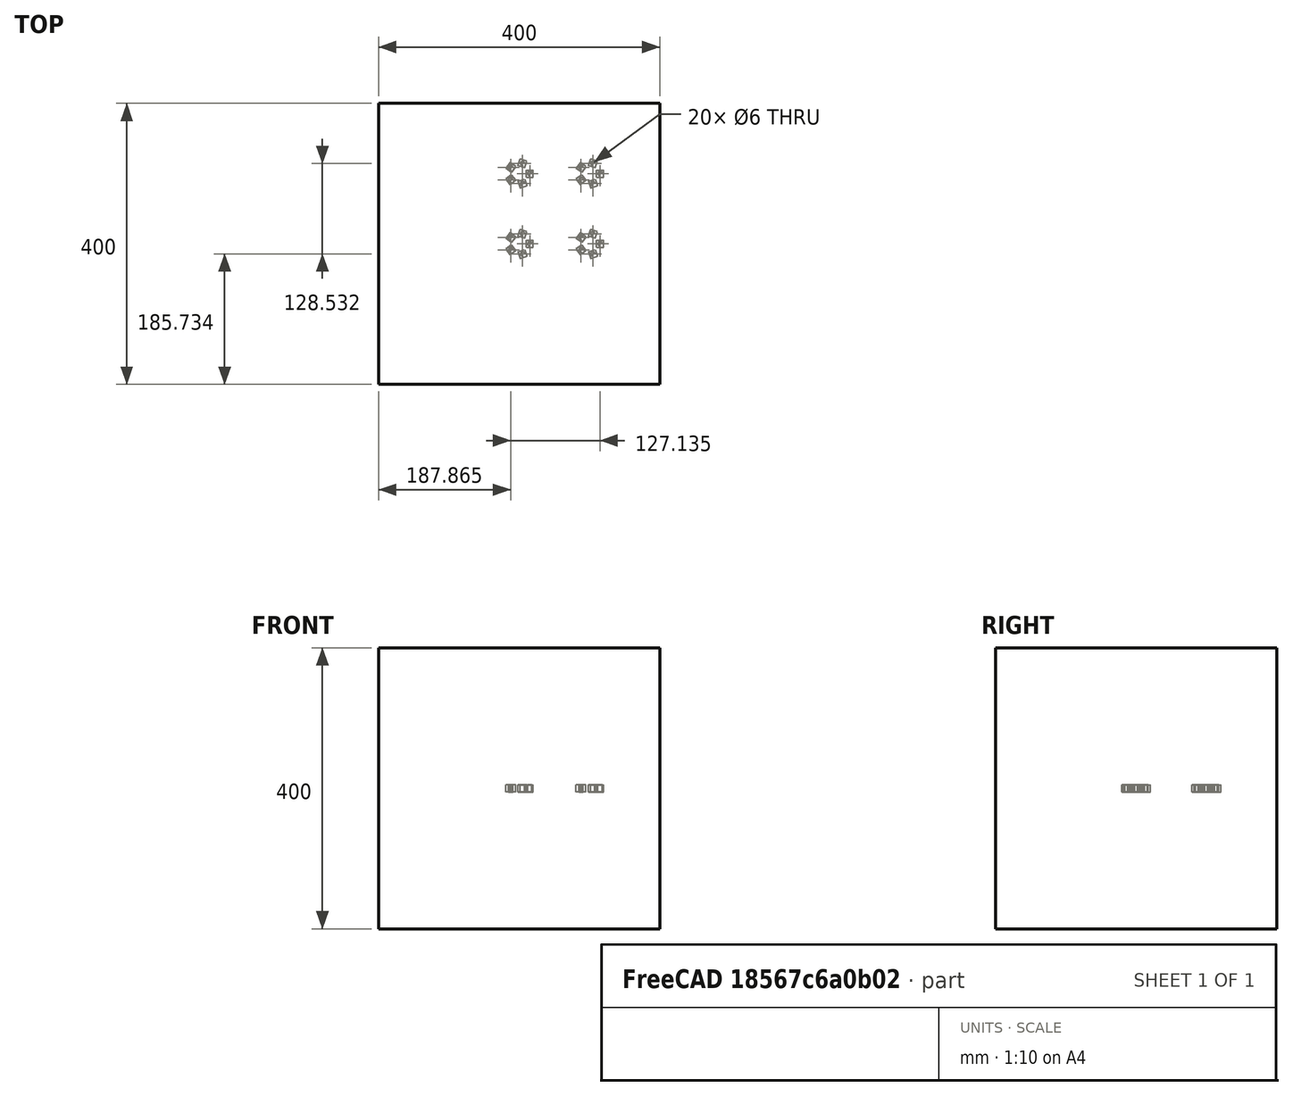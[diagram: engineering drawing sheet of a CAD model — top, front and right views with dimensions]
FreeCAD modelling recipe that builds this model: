
FCSTD DOCUMENT  (FreeCAD 0.19RUnknown)
Label: arrayTest-2
License: All rights reserved
LicenseURL: http://en.wikipedia.org/wiki/All_rights_reserved
objects: App::DocumentObjectGroupPython×1248, Part::FeaturePython×5, App::Part×2, Part::Cut×1
note: 6 computed .brp shape members not serialized (recipe doc carries the construction recipe); baked Part::Feature solids carry a one-line shape summary decoded from their .brp

FEATURE [App::DocumentObjectGroupPython] HALFPI  # scripted group (container) (typed FeaturePython)
  name = HALFPI
  value = pi/2.
FEATURE [App::DocumentObjectGroupPython] PI  # scripted group (container) (typed FeaturePython)
  name = PI
  value = 1.*pi
FEATURE [App::DocumentObjectGroupPython] TWOPI  # scripted group (container) (typed FeaturePython)
  name = TWOPI
  value = 2.*pi
FEATURE [App::DocumentObjectGroupPython] Constants  # scripted group (container) (typed FeaturePython)
  Group = -> [HALFPI,PI,TWOPI]
FEATURE [App::DocumentObjectGroupPython] Variables  # scripted group (container) (typed FeaturePython)
FEATURE [App::DocumentObjectGroupPython] Quantities  # scripted group (container) (typed FeaturePython)
FEATURE [App::DocumentObjectGroupPython] Isotopes  # scripted group (container) (typed FeaturePython)
FEATURE [App::DocumentObjectGroupPython] Elements  # scripted group (container) (typed FeaturePython)
FEATURE [App::DocumentObjectGroupPython] G4Isotopes  # scripted group (container) (typed FeaturePython)
FEATURE [App::DocumentObjectGroupPython] H_element  # scripted group (container) (typed FeaturePython)
  Z = 1
  atom_value = 1.008
  formula = H
  name = H_element
FEATURE [App::DocumentObjectGroupPython] He_element  # scripted group (container) (typed FeaturePython)
  Z = 2
  atom_value = 4.0026
  formula = He
  name = He_element
FEATURE [App::DocumentObjectGroupPython] Li_element  # scripted group (container) (typed FeaturePython)
  Z = 3
  atom_value = 6.94
  formula = Li
  name = Li_element
FEATURE [App::DocumentObjectGroupPython] Be_element  # scripted group (container) (typed FeaturePython)
  Z = 4
  atom_value = 9.01218
  formula = Be
  name = Be_element
FEATURE [App::DocumentObjectGroupPython] B_element  # scripted group (container) (typed FeaturePython)
  Z = 5
  atom_value = 10.81
  formula = B
  name = B_element
FEATURE [App::DocumentObjectGroupPython] C_element  # scripted group (container) (typed FeaturePython)
  Z = 6
  atom_value = 12.011
  formula = C
  name = C_element
FEATURE [App::DocumentObjectGroupPython] N_element  # scripted group (container) (typed FeaturePython)
  Z = 7
  atom_value = 14.007
  formula = N
  name = N_element
FEATURE [App::DocumentObjectGroupPython] O_element  # scripted group (container) (typed FeaturePython)
  Z = 8
  atom_value = 15.999
  formula = O
  name = O_element
FEATURE [App::DocumentObjectGroupPython] F_element  # scripted group (container) (typed FeaturePython)
  Z = 9
  atom_value = 18.9984
  formula = F
  name = F_element
FEATURE [App::DocumentObjectGroupPython] Ne_element  # scripted group (container) (typed FeaturePython)
  Z = 10
  atom_value = 20.1797
  formula = Ne
  name = Ne_element
FEATURE [App::DocumentObjectGroupPython] Na_element  # scripted group (container) (typed FeaturePython)
  Z = 11
  atom_value = 22.9898
  formula = Na
  name = Na_element
FEATURE [App::DocumentObjectGroupPython] Mg_element  # scripted group (container) (typed FeaturePython)
  Z = 12
  atom_value = 24.305
  formula = Mg
  name = Mg_element
FEATURE [App::DocumentObjectGroupPython] Al_element  # scripted group (container) (typed FeaturePython)
  Z = 13
  atom_value = 26.9815
  formula = Al
  name = Al_element
FEATURE [App::DocumentObjectGroupPython] Si_element  # scripted group (container) (typed FeaturePython)
  Z = 14
  atom_value = 28.085
  formula = Si
  name = Si_element
FEATURE [App::DocumentObjectGroupPython] P_element  # scripted group (container) (typed FeaturePython)
  Z = 15
  atom_value = 30.9738
  formula = P
  name = P_element
FEATURE [App::DocumentObjectGroupPython] S_element  # scripted group (container) (typed FeaturePython)
  Z = 16
  atom_value = 32.06
  formula = S
  name = S_element
FEATURE [App::DocumentObjectGroupPython] Cl_element  # scripted group (container) (typed FeaturePython)
  Z = 17
  atom_value = 35.45
  formula = Cl
  name = Cl_element
FEATURE [App::DocumentObjectGroupPython] Ar_element  # scripted group (container) (typed FeaturePython)
  Z = 18
  atom_value = 39.95
  formula = Ar
  name = Ar_element
FEATURE [App::DocumentObjectGroupPython] K_element  # scripted group (container) (typed FeaturePython)
  Z = 19
  atom_value = 39.0983
  formula = K
  name = K_element
FEATURE [App::DocumentObjectGroupPython] Ca_element  # scripted group (container) (typed FeaturePython)
  Z = 20
  atom_value = 40.078
  formula = Ca
  name = Ca_element
FEATURE [App::DocumentObjectGroupPython] Sc_element  # scripted group (container) (typed FeaturePython)
  Z = 21
  atom_value = 44.9559
  formula = Sc
  name = Sc_element
FEATURE [App::DocumentObjectGroupPython] Ti_element  # scripted group (container) (typed FeaturePython)
  Z = 22
  atom_value = 47.867
  formula = Ti
  name = Ti_element
FEATURE [App::DocumentObjectGroupPython] V_element  # scripted group (container) (typed FeaturePython)
  Z = 23
  atom_value = 50.9415
  formula = V
  name = V_element
FEATURE [App::DocumentObjectGroupPython] Cr_element  # scripted group (container) (typed FeaturePython)
  Z = 24
  atom_value = 51.9961
  formula = Cr
  name = Cr_element
FEATURE [App::DocumentObjectGroupPython] Mn_element  # scripted group (container) (typed FeaturePython)
  Z = 25
  atom_value = 54.938
  formula = Mn
  name = Mn_element
FEATURE [App::DocumentObjectGroupPython] Fe_element  # scripted group (container) (typed FeaturePython)
  Z = 26
  atom_value = 55.845
  formula = Fe
  name = Fe_element
FEATURE [App::DocumentObjectGroupPython] Co_element  # scripted group (container) (typed FeaturePython)
  Z = 27
  atom_value = 58.9332
  formula = Co
  name = Co_element
FEATURE [App::DocumentObjectGroupPython] Ni_element  # scripted group (container) (typed FeaturePython)
  Z = 28
  atom_value = 58.6934
  formula = Ni
  name = Ni_element
FEATURE [App::DocumentObjectGroupPython] Cu_element  # scripted group (container) (typed FeaturePython)
  Z = 29
  atom_value = 63.546
  formula = Cu
  name = Cu_element
FEATURE [App::DocumentObjectGroupPython] Zn_element  # scripted group (container) (typed FeaturePython)
  Z = 30
  atom_value = 65.38
  formula = Zn
  name = Zn_element
FEATURE [App::DocumentObjectGroupPython] Ga_element  # scripted group (container) (typed FeaturePython)
  Z = 31
  atom_value = 69.723
  formula = Ga
  name = Ga_element
FEATURE [App::DocumentObjectGroupPython] Ge_element  # scripted group (container) (typed FeaturePython)
  Z = 32
  atom_value = 72.63
  formula = Ge
  name = Ge_element
FEATURE [App::DocumentObjectGroupPython] As_element  # scripted group (container) (typed FeaturePython)
  Z = 33
  atom_value = 74.9216
  formula = As
  name = As_element
FEATURE [App::DocumentObjectGroupPython] Se_element  # scripted group (container) (typed FeaturePython)
  Z = 34
  atom_value = 78.971
  formula = Se
  name = Se_element
FEATURE [App::DocumentObjectGroupPython] Br_element  # scripted group (container) (typed FeaturePython)
  Z = 35
  atom_value = 79.904
  formula = Br
  name = Br_element
FEATURE [App::DocumentObjectGroupPython] Kr_element  # scripted group (container) (typed FeaturePython)
  Z = 36
  atom_value = 83.798
  formula = Kr
  name = Kr_element
FEATURE [App::DocumentObjectGroupPython] Rb_element  # scripted group (container) (typed FeaturePython)
  Z = 37
  atom_value = 85.4678
  formula = Rb
  name = Rb_element
FEATURE [App::DocumentObjectGroupPython] Sr_element  # scripted group (container) (typed FeaturePython)
  Z = 38
  atom_value = 87.62
  formula = Sr
  name = Sr_element
FEATURE [App::DocumentObjectGroupPython] Y_element  # scripted group (container) (typed FeaturePython)
  Z = 39
  atom_value = 88.9058
  formula = Y
  name = Y_element
FEATURE [App::DocumentObjectGroupPython] Zr_element  # scripted group (container) (typed FeaturePython)
  Z = 40
  atom_value = 91.224
  formula = Zr
  name = Zr_element
FEATURE [App::DocumentObjectGroupPython] Nb_element  # scripted group (container) (typed FeaturePython)
  Z = 41
  atom_value = 92.9064
  formula = Nb
  name = Nb_element
FEATURE [App::DocumentObjectGroupPython] Mo_element  # scripted group (container) (typed FeaturePython)
  Z = 42
  atom_value = 95.95
  formula = Mo
  name = Mo_element
FEATURE [App::DocumentObjectGroupPython] Tc_element  # scripted group (container) (typed FeaturePython)
  Z = 43
  atom_value = 97
  formula = Tc
  name = Tc_element
FEATURE [App::DocumentObjectGroupPython] Ru_element  # scripted group (container) (typed FeaturePython)
  Z = 44
  atom_value = 101.07
  formula = Ru
  name = Ru_element
FEATURE [App::DocumentObjectGroupPython] Rh_element  # scripted group (container) (typed FeaturePython)
  Z = 45
  atom_value = 102.905
  formula = Rh
  name = Rh_element
FEATURE [App::DocumentObjectGroupPython] Pd_element  # scripted group (container) (typed FeaturePython)
  Z = 46
  atom_value = 106.42
  formula = Pd
  name = Pd_element
FEATURE [App::DocumentObjectGroupPython] Ag_element  # scripted group (container) (typed FeaturePython)
  Z = 47
  atom_value = 107.868
  formula = Ag
  name = Ag_element
FEATURE [App::DocumentObjectGroupPython] Cd_element  # scripted group (container) (typed FeaturePython)
  Z = 48
  atom_value = 112.414
  formula = Cd
  name = Cd_element
FEATURE [App::DocumentObjectGroupPython] In_element  # scripted group (container) (typed FeaturePython)
  Z = 49
  atom_value = 114.818
  formula = In
  name = In_element
FEATURE [App::DocumentObjectGroupPython] Sn_element  # scripted group (container) (typed FeaturePython)
  Z = 50
  atom_value = 118.71
  formula = Sn
  name = Sn_element
FEATURE [App::DocumentObjectGroupPython] Sb_element  # scripted group (container) (typed FeaturePython)
  Z = 51
  atom_value = 121.76
  formula = Sb
  name = Sb_element
FEATURE [App::DocumentObjectGroupPython] Te_element  # scripted group (container) (typed FeaturePython)
  Z = 52
  atom_value = 127.6
  formula = Te
  name = Te_element
FEATURE [App::DocumentObjectGroupPython] I_element  # scripted group (container) (typed FeaturePython)
  Z = 53
  atom_value = 126.904
  formula = I
  name = I_element
FEATURE [App::DocumentObjectGroupPython] Xe_element  # scripted group (container) (typed FeaturePython)
  Z = 54
  atom_value = 131.293
  formula = Xe
  name = Xe_element
FEATURE [App::DocumentObjectGroupPython] Cs_element  # scripted group (container) (typed FeaturePython)
  Z = 55
  atom_value = 132.905
  formula = Cs
  name = Cs_element
FEATURE [App::DocumentObjectGroupPython] Ba_element  # scripted group (container) (typed FeaturePython)
  Z = 56
  atom_value = 137.327
  formula = Ba
  name = Ba_element
FEATURE [App::DocumentObjectGroupPython] La_element  # scripted group (container) (typed FeaturePython)
  Z = 57
  atom_value = 138.905
  formula = La
  name = La_element
FEATURE [App::DocumentObjectGroupPython] Ce_element  # scripted group (container) (typed FeaturePython)
  Z = 58
  atom_value = 140.116
  formula = Ce
  name = Ce_element
FEATURE [App::DocumentObjectGroupPython] Pr_element  # scripted group (container) (typed FeaturePython)
  Z = 59
  atom_value = 140.908
  formula = Pr
  name = Pr_element
FEATURE [App::DocumentObjectGroupPython] Nd_element  # scripted group (container) (typed FeaturePython)
  Z = 60
  atom_value = 144.242
  formula = Nd
  name = Nd_element
FEATURE [App::DocumentObjectGroupPython] Pm_element  # scripted group (container) (typed FeaturePython)
  Z = 61
  atom_value = 145
  formula = Pm
  name = Pm_element
FEATURE [App::DocumentObjectGroupPython] Sm_element  # scripted group (container) (typed FeaturePython)
  Z = 62
  atom_value = 150.36
  formula = Sm
  name = Sm_element
FEATURE [App::DocumentObjectGroupPython] Eu_element  # scripted group (container) (typed FeaturePython)
  Z = 63
  atom_value = 151.964
  formula = Eu
  name = Eu_element
FEATURE [App::DocumentObjectGroupPython] Gd_element  # scripted group (container) (typed FeaturePython)
  Z = 64
  atom_value = 157.25
  formula = Gd
  name = Gd_element
FEATURE [App::DocumentObjectGroupPython] Tb_element  # scripted group (container) (typed FeaturePython)
  Z = 65
  atom_value = 158.925
  formula = Tb
  name = Tb_element
FEATURE [App::DocumentObjectGroupPython] Dy_element  # scripted group (container) (typed FeaturePython)
  Z = 66
  atom_value = 162.5
  formula = Dy
  name = Dy_element
FEATURE [App::DocumentObjectGroupPython] Ho_element  # scripted group (container) (typed FeaturePython)
  Z = 67
  atom_value = 164.93
  formula = Ho
  name = Ho_element
FEATURE [App::DocumentObjectGroupPython] Er_element  # scripted group (container) (typed FeaturePython)
  Z = 68
  atom_value = 167.259
  formula = Er
  name = Er_element
FEATURE [App::DocumentObjectGroupPython] Tm_element  # scripted group (container) (typed FeaturePython)
  Z = 69
  atom_value = 168.934
  formula = Tm
  name = Tm_element
FEATURE [App::DocumentObjectGroupPython] Yb_element  # scripted group (container) (typed FeaturePython)
  Z = 70
  atom_value = 173.045
  formula = Yb
  name = Yb_element
FEATURE [App::DocumentObjectGroupPython] Lu_element  # scripted group (container) (typed FeaturePython)
  Z = 71
  atom_value = 174.967
  formula = Lu
  name = Lu_element
FEATURE [App::DocumentObjectGroupPython] Hf_element  # scripted group (container) (typed FeaturePython)
  Z = 72
  atom_value = 178.49
  formula = Hf
  name = Hf_element
FEATURE [App::DocumentObjectGroupPython] Ta_element  # scripted group (container) (typed FeaturePython)
  Z = 73
  atom_value = 180.948
  formula = Ta
  name = Ta_element
FEATURE [App::DocumentObjectGroupPython] W_element  # scripted group (container) (typed FeaturePython)
  Z = 74
  atom_value = 183.84
  formula = W
  name = W_element
FEATURE [App::DocumentObjectGroupPython] Re_element  # scripted group (container) (typed FeaturePython)
  Z = 75
  atom_value = 186.207
  formula = Re
  name = Re_element
FEATURE [App::DocumentObjectGroupPython] Os_element  # scripted group (container) (typed FeaturePython)
  Z = 76
  atom_value = 190.23
  formula = Os
  name = Os_element
FEATURE [App::DocumentObjectGroupPython] Ir_element  # scripted group (container) (typed FeaturePython)
  Z = 77
  atom_value = 192.217
  formula = Ir
  name = Ir_element
FEATURE [App::DocumentObjectGroupPython] Pt_element  # scripted group (container) (typed FeaturePython)
  Z = 78
  atom_value = 195.084
  formula = Pt
  name = Pt_element
FEATURE [App::DocumentObjectGroupPython] Au_element  # scripted group (container) (typed FeaturePython)
  Z = 79
  atom_value = 196.967
  formula = Au
  name = Au_element
FEATURE [App::DocumentObjectGroupPython] Hg_element  # scripted group (container) (typed FeaturePython)
  Z = 80
  atom_value = 200.592
  formula = Hg
  name = Hg_element
FEATURE [App::DocumentObjectGroupPython] Tl_element  # scripted group (container) (typed FeaturePython)
  Z = 81
  atom_value = 204.38
  formula = Tl
  name = Tl_element
FEATURE [App::DocumentObjectGroupPython] Pb_element  # scripted group (container) (typed FeaturePython)
  Z = 82
  atom_value = 207.2
  formula = Pb
  name = Pb_element
FEATURE [App::DocumentObjectGroupPython] Bi_element  # scripted group (container) (typed FeaturePython)
  Z = 83
  atom_value = 208.98
  formula = Bi
  name = Bi_element
FEATURE [App::DocumentObjectGroupPython] Po_element  # scripted group (container) (typed FeaturePython)
  Z = 84
  atom_value = 209
  formula = Po
  name = Po_element
FEATURE [App::DocumentObjectGroupPython] At_element  # scripted group (container) (typed FeaturePython)
  Z = 85
  atom_value = 210
  formula = At
  name = At_element
FEATURE [App::DocumentObjectGroupPython] Rn_element  # scripted group (container) (typed FeaturePython)
  Z = 86
  atom_value = 222
  formula = Rn
  name = Rn_element
FEATURE [App::DocumentObjectGroupPython] Fr_element  # scripted group (container) (typed FeaturePython)
  Z = 87
  atom_value = 223
  formula = Fr
  name = Fr_element
FEATURE [App::DocumentObjectGroupPython] Ra_element  # scripted group (container) (typed FeaturePython)
  Z = 88
  atom_value = 226
  formula = Ra
  name = Ra_element
FEATURE [App::DocumentObjectGroupPython] Ac_element  # scripted group (container) (typed FeaturePython)
  Z = 89
  atom_value = 227
  formula = Ac
  name = Ac_element
FEATURE [App::DocumentObjectGroupPython] Th_element  # scripted group (container) (typed FeaturePython)
  Z = 90
  atom_value = 232.038
  formula = Th
  name = Th_element
FEATURE [App::DocumentObjectGroupPython] Pa_element  # scripted group (container) (typed FeaturePython)
  Z = 91
  atom_value = 231.036
  formula = Pa
  name = Pa_element
FEATURE [App::DocumentObjectGroupPython] U_element  # scripted group (container) (typed FeaturePython)
  Z = 92
  atom_value = 238.029
  formula = U
  name = U_element
FEATURE [App::DocumentObjectGroupPython] Np_element  # scripted group (container) (typed FeaturePython)
  Z = 93
  atom_value = 237
  formula = Np
  name = Np_element
FEATURE [App::DocumentObjectGroupPython] Pu_element  # scripted group (container) (typed FeaturePython)
  Z = 94
  atom_value = 244
  formula = Pu
  name = Pu_element
FEATURE [App::DocumentObjectGroupPython] Am_element  # scripted group (container) (typed FeaturePython)
  Z = 95
  atom_value = 243
  formula = Am
  name = Am_element
FEATURE [App::DocumentObjectGroupPython] Cm_element  # scripted group (container) (typed FeaturePython)
  Z = 96
  atom_value = 247
  formula = Cm
  name = Cm_element
FEATURE [App::DocumentObjectGroupPython] Bk_element  # scripted group (container) (typed FeaturePython)
  Z = 97
  atom_value = 247
  formula = Bk
  name = Bk_element
FEATURE [App::DocumentObjectGroupPython] Cf_element  # scripted group (container) (typed FeaturePython)
  Z = 98
  atom_value = 251
  formula = Cf
  name = Cf_element
FEATURE [App::DocumentObjectGroupPython] G4Elements  # scripted group (container) (typed FeaturePython)
  Group = -> [H_element,He_element,Li_element,Be_element,B_element,C_element,N_element,O_element,F_element,Ne_element,Na_element,Mg_element,Al_element,Si_element,P_element,S_element,Cl_element,Ar_element,K_element,Ca_element,Sc_element,Ti_element,V_element,Cr_element,Mn_element,Fe_element,Co_element,Ni_element,Cu_element,Zn_element,Ga_element,Ge_element,As_element,Se_element,Br_element,Kr_element,Rb_element,+61 more]
FEATURE [App::DocumentObjectGroupPython] H_element001  label="H_element : 0.101"  # scripted group (container) (typed FeaturePython)
  n = 0.101327
FEATURE [App::DocumentObjectGroupPython] C_element001  label="C_element : 0.775"  # scripted group (container) (typed FeaturePython)
  n = 0.7755
FEATURE [App::DocumentObjectGroupPython] N_element001  label="N_element : 0.035"  # scripted group (container) (typed FeaturePython)
  n = 0.035057
FEATURE [App::DocumentObjectGroupPython] O_element001  label="O_element : 0.052"  # scripted group (container) (typed FeaturePython)
  n = 0.0523159
FEATURE [App::DocumentObjectGroupPython] F_element001  label="F_element : 0.017"  # scripted group (container) (typed FeaturePython)
  n = 0.017422
FEATURE [App::DocumentObjectGroupPython] Ca_element001  label="Ca_element : 0.018"  # scripted group (container) (typed FeaturePython)
  n = 0.018378
FEATURE [App::DocumentObjectGroupPython] G4_A_150_TISSUE  label="G4_A-150_TISSUE"  # scripted group (container) (typed FeaturePython)
  Dunit = g/cm3
  Dvalue = 1.127
  Group = -> [H_element001,C_element001,N_element001,O_element001,F_element001,Ca_element001]
  conduct = 2
  density = 1
  expand = 3
  formula = G4_A-150_TISSUE
  name = G4_A-150_TISSUE
  specific = 4
FEATURE [App::DocumentObjectGroupPython] C_element002  label="C_element : 3"  # scripted group (container) (typed FeaturePython)
  n = 3
  ref = C_element
FEATURE [App::DocumentObjectGroupPython] H_element002  label="H_element : 6"  # scripted group (container) (typed FeaturePython)
  n = 6
  ref = H_element
FEATURE [App::DocumentObjectGroupPython] O_element002  label="O_element : 1"  # scripted group (container) (typed FeaturePython)
  n = 1
  ref = O_element
FEATURE [App::DocumentObjectGroupPython] G4_ACETONE  # scripted group (container) (typed FeaturePython)
  Dunit = g/cm3
  Dvalue = 0.7899
  Group = -> [C_element002,H_element002,O_element002]
  conduct = 2
  density = 1
  expand = 3
  formula = G4_ACETONE
  name = G4_ACETONE
  specific = 4
FEATURE [App::DocumentObjectGroupPython] C_element003  label="C_element : 2"  # scripted group (container) (typed FeaturePython)
  n = 2
  ref = C_element
FEATURE [App::DocumentObjectGroupPython] H_element003  label="H_element : 2"  # scripted group (container) (typed FeaturePython)
  n = 2
  ref = H_element
FEATURE [App::DocumentObjectGroupPython] G4_ACETYLENE  # scripted group (container) (typed FeaturePython)
  Dunit = g/cm3
  Dvalue = 0.0010967
  Group = -> [C_element003,H_element003]
  conduct = 2
  density = 1
  expand = 3
  formula = G4_ACETYLENE
  name = G4_ACETYLENE
  specific = 4
FEATURE [App::DocumentObjectGroupPython] C_element004  label="C_element : 5"  # scripted group (container) (typed FeaturePython)
  n = 5
  ref = C_element
FEATURE [App::DocumentObjectGroupPython] H_element004  label="H_element : 5"  # scripted group (container) (typed FeaturePython)
  n = 5
  ref = H_element
FEATURE [App::DocumentObjectGroupPython] N_element002  label="N_element : 5"  # scripted group (container) (typed FeaturePython)
  n = 5
  ref = N_element
FEATURE [App::DocumentObjectGroupPython] G4_ADENINE  # scripted group (container) (typed FeaturePython)
  Dunit = g/cm3
  Dvalue = 1.6
  Group = -> [C_element004,H_element004,N_element002]
  conduct = 2
  density = 1
  expand = 3
  formula = G4_ADENINE
  name = G4_ADENINE
  specific = 4
FEATURE [App::DocumentObjectGroupPython] H_element005  label="H_element : 0.114"  # scripted group (container) (typed FeaturePython)
  n = 0.114
FEATURE [App::DocumentObjectGroupPython] C_element005  label="C_element : 0.598"  # scripted group (container) (typed FeaturePython)
  n = 0.598
FEATURE [App::DocumentObjectGroupPython] N_element003  label="N_element : 0.007"  # scripted group (container) (typed FeaturePython)
  n = 0.007
FEATURE [App::DocumentObjectGroupPython] O_element003  label="O_element : 0.278"  # scripted group (container) (typed FeaturePython)
  n = 0.278
FEATURE [App::DocumentObjectGroupPython] Na_element001  label="Na_element : 0.001"  # scripted group (container) (typed FeaturePython)
  n = 0.001
FEATURE [App::DocumentObjectGroupPython] S_element001  label="S_element : 0.001"  # scripted group (container) (typed FeaturePython)
  n = 0.001
FEATURE [App::DocumentObjectGroupPython] Cl_element001  label="Cl_element : 0.001"  # scripted group (container) (typed FeaturePython)
  n = 0.001
FEATURE [App::DocumentObjectGroupPython] G4_ADIPOSE_TISSUE_ICRP  # scripted group (container) (typed FeaturePython)
  Dunit = g/cm3
  Dvalue = 0.95
  Group = -> [H_element005,C_element005,N_element003,O_element003,Na_element001,S_element001,Cl_element001]
  conduct = 2
  density = 1
  expand = 3
  formula = G4_ADIPOSE_TISSUE_ICRP
  name = G4_ADIPOSE_TISSUE_ICRP
  specific = 4
FEATURE [App::DocumentObjectGroupPython] C_element006  label="C_element : 0.000"  # scripted group (container) (typed FeaturePython)
  n = 0.000124
FEATURE [App::DocumentObjectGroupPython] N_element004  label="N_element : 0.755"  # scripted group (container) (typed FeaturePython)
  n = 0.755268
FEATURE [App::DocumentObjectGroupPython] O_element004  label="O_element : 0.232"  # scripted group (container) (typed FeaturePython)
  n = 0.231781
FEATURE [App::DocumentObjectGroupPython] Ar_element001  label="Ar_element : 0.013"  # scripted group (container) (typed FeaturePython)
  n = 0.012827
FEATURE [App::DocumentObjectGroupPython] G4_AIR  # scripted group (container) (typed FeaturePython)
  Dunit = g/cm3
  Dvalue = 0.00120479
  Group = -> [C_element006,N_element004,O_element004,Ar_element001]
  conduct = 2
  density = 1
  expand = 3
  formula = G4_AIR
  name = G4_AIR
  specific = 4
FEATURE [App::DocumentObjectGroupPython] C_element007  label="C_element : 006"  # scripted group (container) (typed FeaturePython)
  n = 3
  ref = C_element
FEATURE [App::DocumentObjectGroupPython] H_element006  label="H_element : 7"  # scripted group (container) (typed FeaturePython)
  n = 7
  ref = H_element
FEATURE [App::DocumentObjectGroupPython] N_element005  label="N_element : 1"  # scripted group (container) (typed FeaturePython)
  n = 1
  ref = N_element
FEATURE [App::DocumentObjectGroupPython] O_element005  label="O_element : 2"  # scripted group (container) (typed FeaturePython)
  n = 2
  ref = O_element
FEATURE [App::DocumentObjectGroupPython] G4_ALANINE  # scripted group (container) (typed FeaturePython)
  Dunit = g/cm3
  Dvalue = 1.42
  Group = -> [C_element007,H_element006,N_element005,O_element005]
  conduct = 2
  density = 1
  expand = 3
  formula = G4_ALANINE
  name = G4_ALANINE
  specific = 4
FEATURE [App::DocumentObjectGroupPython] Al_element001  label="Al_element : 2"  # scripted group (container) (typed FeaturePython)
  n = 2
  ref = Al_element
FEATURE [App::DocumentObjectGroupPython] O_element006  label="O_element : 3"  # scripted group (container) (typed FeaturePython)
  n = 3
  ref = O_element
FEATURE [App::DocumentObjectGroupPython] G4_ALUMINUM_OXIDE  # scripted group (container) (typed FeaturePython)
  Dunit = g/cm3
  Dvalue = 3.97
  Group = -> [Al_element001,O_element006]
  conduct = 2
  density = 1
  expand = 3
  formula = G4_ALUMINUM_OXIDE
  name = G4_ALUMINUM_OXIDE
  specific = 4
FEATURE [App::DocumentObjectGroupPython] H_element007  label="H_element : 0.106"  # scripted group (container) (typed FeaturePython)
  n = 0.10593
FEATURE [App::DocumentObjectGroupPython] C_element008  label="C_element : 0.789"  # scripted group (container) (typed FeaturePython)
  n = 0.788974
FEATURE [App::DocumentObjectGroupPython] O_element007  label="O_element : 0.105"  # scripted group (container) (typed FeaturePython)
  n = 0.105096
FEATURE [App::DocumentObjectGroupPython] G4_AMBER  # scripted group (container) (typed FeaturePython)
  Dunit = g/cm3
  Dvalue = 1.1
  Group = -> [H_element007,C_element008,O_element007]
  conduct = 2
  density = 1
  expand = 3
  formula = G4_AMBER
  name = G4_AMBER
  specific = 4
FEATURE [App::DocumentObjectGroupPython] N_element006  label="N_element : 006"  # scripted group (container) (typed FeaturePython)
  n = 1
  ref = N_element
FEATURE [App::DocumentObjectGroupPython] H_element008  label="H_element : 3"  # scripted group (container) (typed FeaturePython)
  n = 3
  ref = H_element
FEATURE [App::DocumentObjectGroupPython] G4_AMMONIA  # scripted group (container) (typed FeaturePython)
  Dunit = g/cm3
  Dvalue = 0.000826019
  Group = -> [N_element006,H_element008]
  conduct = 2
  density = 1
  expand = 3
  formula = G4_AMMONIA
  name = G4_AMMONIA
  specific = 4
FEATURE [App::DocumentObjectGroupPython] C_element009  label="C_element : 6"  # scripted group (container) (typed FeaturePython)
  n = 6
  ref = C_element
FEATURE [App::DocumentObjectGroupPython] H_element009  label="H_element : 008"  # scripted group (container) (typed FeaturePython)
  n = 7
  ref = H_element
FEATURE [App::DocumentObjectGroupPython] N_element007  label="N_element : 007"  # scripted group (container) (typed FeaturePython)
  n = 1
  ref = N_element
FEATURE [App::DocumentObjectGroupPython] G4_ANILINE  # scripted group (container) (typed FeaturePython)
  Dunit = g/cm3
  Dvalue = 1.0235
  Group = -> [C_element009,H_element009,N_element007]
  conduct = 2
  density = 1
  expand = 3
  formula = G4_ANILINE
  name = G4_ANILINE
  specific = 4
FEATURE [App::DocumentObjectGroupPython] C_element010  label="C_element : 14"  # scripted group (container) (typed FeaturePython)
  n = 14
  ref = C_element
FEATURE [App::DocumentObjectGroupPython] H_element010  label="H_element : 10"  # scripted group (container) (typed FeaturePython)
  n = 10
  ref = H_element
FEATURE [App::DocumentObjectGroupPython] G4_ANTHRACENE  # scripted group (container) (typed FeaturePython)
  Dunit = g/cm3
  Dvalue = 1.283
  Group = -> [C_element010,H_element010]
  conduct = 2
  density = 1
  expand = 3
  formula = G4_ANTHRACENE
  name = G4_ANTHRACENE
  specific = 4
FEATURE [App::DocumentObjectGroupPython] H_element011  label="H_element : 0.065"  # scripted group (container) (typed FeaturePython)
  n = 0.0654709
FEATURE [App::DocumentObjectGroupPython] C_element011  label="C_element : 0.537"  # scripted group (container) (typed FeaturePython)
  n = 0.536944
FEATURE [App::DocumentObjectGroupPython] N_element008  label="N_element : 0.021"  # scripted group (container) (typed FeaturePython)
  n = 0.0215
FEATURE [App::DocumentObjectGroupPython] O_element008  label="O_element : 0.032"  # scripted group (container) (typed FeaturePython)
  n = 0.032085
FEATURE [App::DocumentObjectGroupPython] F_element002  label="F_element : 0.167"  # scripted group (container) (typed FeaturePython)
  n = 0.167411
FEATURE [App::DocumentObjectGroupPython] Ca_element002  label="Ca_element : 0.177"  # scripted group (container) (typed FeaturePython)
  n = 0.176589
FEATURE [App::DocumentObjectGroupPython] G4_B_100_BONE  label="G4_B-100_BONE"  # scripted group (container) (typed FeaturePython)
  Dunit = g/cm3
  Dvalue = 1.45
  Group = -> [H_element011,C_element011,N_element008,O_element008,F_element002,Ca_element002]
  conduct = 2
  density = 1
  expand = 3
  formula = G4_B-100_BONE
  name = G4_B-100_BONE
  specific = 4
FEATURE [App::DocumentObjectGroupPython] H_element012  label="H_element : 0.057"  # scripted group (container) (typed FeaturePython)
  n = 0.057441
FEATURE [App::DocumentObjectGroupPython] C_element012  label="C_element : 0.790"  # scripted group (container) (typed FeaturePython)
  n = 0.774591
FEATURE [App::DocumentObjectGroupPython] O_element009  label="O_element : 0.168"  # scripted group (container) (typed FeaturePython)
  n = 0.167968
FEATURE [App::DocumentObjectGroupPython] G4_BAKELITE  # scripted group (container) (typed FeaturePython)
  Dunit = g/cm3
  Dvalue = 1.25
  Group = -> [H_element012,C_element012,O_element009]
  conduct = 2
  density = 1
  expand = 3
  formula = G4_BAKELITE
  name = G4_BAKELITE
  specific = 4
FEATURE [App::DocumentObjectGroupPython] Ba_element001  label="Ba_element : 1"  # scripted group (container) (typed FeaturePython)
  n = 1
  ref = Ba_element
FEATURE [App::DocumentObjectGroupPython] F_element003  label="F_element : 2"  # scripted group (container) (typed FeaturePython)
  n = 2
  ref = F_element
FEATURE [App::DocumentObjectGroupPython] G4_BARIUM_FLUORIDE  # scripted group (container) (typed FeaturePython)
  Dunit = g/cm3
  Dvalue = 4.89
  Group = -> [Ba_element001,F_element003]
  conduct = 2
  density = 1
  expand = 3
  formula = G4_BARIUM_FLUORIDE
  name = G4_BARIUM_FLUORIDE
  specific = 4
FEATURE [App::DocumentObjectGroupPython] Ba_element002  label="Ba_element : 002"  # scripted group (container) (typed FeaturePython)
  n = 1
  ref = Ba_element
FEATURE [App::DocumentObjectGroupPython] S_element002  label="S_element : 1"  # scripted group (container) (typed FeaturePython)
  n = 1
  ref = S_element
FEATURE [App::DocumentObjectGroupPython] O_element010  label="O_element : 4"  # scripted group (container) (typed FeaturePython)
  n = 4
  ref = O_element
FEATURE [App::DocumentObjectGroupPython] G4_BARIUM_SULFATE  # scripted group (container) (typed FeaturePython)
  Dunit = g/cm3
  Dvalue = 4.5
  Group = -> [Ba_element002,S_element002,O_element010]
  conduct = 2
  density = 1
  expand = 3
  formula = G4_BARIUM_SULFATE
  name = G4_BARIUM_SULFATE
  specific = 4
FEATURE [App::DocumentObjectGroupPython] C_element013  label="C_element : 007"  # scripted group (container) (typed FeaturePython)
  n = 6
  ref = C_element
FEATURE [App::DocumentObjectGroupPython] H_element013  label="H_element : 009"  # scripted group (container) (typed FeaturePython)
  n = 6
  ref = H_element
FEATURE [App::DocumentObjectGroupPython] G4_BENZENE  # scripted group (container) (typed FeaturePython)
  Dunit = g/cm3
  Dvalue = 0.87865
  Group = -> [C_element013,H_element013]
  conduct = 2
  density = 1
  expand = 3
  formula = G4_BENZENE
  name = G4_BENZENE
  specific = 4
FEATURE [App::DocumentObjectGroupPython] Be_element001  label="Be_element : 1"  # scripted group (container) (typed FeaturePython)
  n = 1
  ref = Be_element
FEATURE [App::DocumentObjectGroupPython] O_element011  label="O_element : 005"  # scripted group (container) (typed FeaturePython)
  n = 1
  ref = O_element
FEATURE [App::DocumentObjectGroupPython] G4_BERYLLIUM_OXIDE  # scripted group (container) (typed FeaturePython)
  Dunit = g/cm3
  Dvalue = 3.01
  Group = -> [Be_element001,O_element011]
  conduct = 2
  density = 1
  expand = 3
  formula = G4_BERYLLIUM_OXIDE
  name = G4_BERYLLIUM_OXIDE
  specific = 4
FEATURE [App::DocumentObjectGroupPython] Bi_element001  label="Bi_element : 4"  # scripted group (container) (typed FeaturePython)
  n = 4
  ref = Bi_element
FEATURE [App::DocumentObjectGroupPython] Ge_element001  label="Ge_element : 3"  # scripted group (container) (typed FeaturePython)
  n = 3
  ref = Ge_element
FEATURE [App::DocumentObjectGroupPython] O_element012  label="O_element : 12"  # scripted group (container) (typed FeaturePython)
  n = 12
  ref = O_element
FEATURE [App::DocumentObjectGroupPython] G4_BGO  # scripted group (container) (typed FeaturePython)
  Dunit = g/cm3
  Dvalue = 7.13
  Group = -> [Bi_element001,Ge_element001,O_element012]
  conduct = 2
  density = 1
  expand = 3
  formula = G4_BGO
  name = G4_BGO
  specific = 4
FEATURE [App::DocumentObjectGroupPython] H_element014  label="H_element : 0.102"  # scripted group (container) (typed FeaturePython)
  n = 0.102
FEATURE [App::DocumentObjectGroupPython] C_element014  label="C_element : 0.110"  # scripted group (container) (typed FeaturePython)
  n = 0.11
FEATURE [App::DocumentObjectGroupPython] N_element009  label="N_element : 0.033"  # scripted group (container) (typed FeaturePython)
  n = 0.033
FEATURE [App::DocumentObjectGroupPython] O_element013  label="O_element : 0.745"  # scripted group (container) (typed FeaturePython)
  n = 0.745
FEATURE [App::DocumentObjectGroupPython] Na_element002  label="Na_element : 0.002"  # scripted group (container) (typed FeaturePython)
  n = 0.001
FEATURE [App::DocumentObjectGroupPython] P_element001  label="P_element : 0.001"  # scripted group (container) (typed FeaturePython)
  n = 0.001
FEATURE [App::DocumentObjectGroupPython] S_element003  label="S_element : 0.002"  # scripted group (container) (typed FeaturePython)
  n = 0.002
FEATURE [App::DocumentObjectGroupPython] Cl_element002  label="Cl_element : 0.003"  # scripted group (container) (typed FeaturePython)
  n = 0.003
FEATURE [App::DocumentObjectGroupPython] K_element001  label="K_element : 0.002"  # scripted group (container) (typed FeaturePython)
  n = 0.002
FEATURE [App::DocumentObjectGroupPython] Fe_element001  label="Fe_element : 0.001"  # scripted group (container) (typed FeaturePython)
  n = 0.001
FEATURE [App::DocumentObjectGroupPython] G4_BLOOD_ICRP  # scripted group (container) (typed FeaturePython)
  Dunit = g/cm3
  Dvalue = 1.06
  Group = -> [H_element014,C_element014,N_element009,O_element013,Na_element002,P_element001,S_element003,Cl_element002,K_element001,Fe_element001]
  conduct = 2
  density = 1
  expand = 3
  formula = G4_BLOOD_ICRP
  name = G4_BLOOD_ICRP
  specific = 4
FEATURE [App::DocumentObjectGroupPython] H_element015  label="H_element : 0.064"  # scripted group (container) (typed FeaturePython)
  n = 0.064
FEATURE [App::DocumentObjectGroupPython] C_element015  label="C_element : 0.278"  # scripted group (container) (typed FeaturePython)
  n = 0.278
FEATURE [App::DocumentObjectGroupPython] N_element010  label="N_element : 0.027"  # scripted group (container) (typed FeaturePython)
  n = 0.027
FEATURE [App::DocumentObjectGroupPython] O_element014  label="O_element : 0.410"  # scripted group (container) (typed FeaturePython)
  n = 0.41
FEATURE [App::DocumentObjectGroupPython] Mg_element001  label="Mg_element : 0.002"  # scripted group (container) (typed FeaturePython)
  n = 0.002
FEATURE [App::DocumentObjectGroupPython] P_element002  label="P_element : 0.070"  # scripted group (container) (typed FeaturePython)
  n = 0.07
FEATURE [App::DocumentObjectGroupPython] S_element004  label="S_element : 0.003"  # scripted group (container) (typed FeaturePython)
  n = 0.002
FEATURE [App::DocumentObjectGroupPython] Ca_element003  label="Ca_element : 0.147"  # scripted group (container) (typed FeaturePython)
  n = 0.147
FEATURE [App::DocumentObjectGroupPython] G4_BONE_COMPACT_ICRU  # scripted group (container) (typed FeaturePython)
  Dunit = g/cm3
  Dvalue = 1.85
  Group = -> [H_element015,C_element015,N_element010,O_element014,Mg_element001,P_element002,S_element004,Ca_element003]
  conduct = 2
  density = 1
  expand = 3
  formula = G4_BONE_COMPACT_ICRU
  name = G4_BONE_COMPACT_ICRU
  specific = 4
FEATURE [App::DocumentObjectGroupPython] H_element016  label="H_element : 0.034"  # scripted group (container) (typed FeaturePython)
  n = 0.034
FEATURE [App::DocumentObjectGroupPython] C_element016  label="C_element : 0.155"  # scripted group (container) (typed FeaturePython)
  n = 0.155
FEATURE [App::DocumentObjectGroupPython] N_element011  label="N_element : 0.042"  # scripted group (container) (typed FeaturePython)
  n = 0.042
FEATURE [App::DocumentObjectGroupPython] O_element015  label="O_element : 0.435"  # scripted group (container) (typed FeaturePython)
  n = 0.435
FEATURE [App::DocumentObjectGroupPython] Na_element003  label="Na_element : 0.003"  # scripted group (container) (typed FeaturePython)
  n = 0.001
FEATURE [App::DocumentObjectGroupPython] Mg_element002  label="Mg_element : 0.003"  # scripted group (container) (typed FeaturePython)
  n = 0.002
FEATURE [App::DocumentObjectGroupPython] P_element003  label="P_element : 0.103"  # scripted group (container) (typed FeaturePython)
  n = 0.103
FEATURE [App::DocumentObjectGroupPython] S_element005  label="S_element : 0.004"  # scripted group (container) (typed FeaturePython)
  n = 0.003
FEATURE [App::DocumentObjectGroupPython] Ca_element004  label="Ca_element : 0.225"  # scripted group (container) (typed FeaturePython)
  n = 0.225
FEATURE [App::DocumentObjectGroupPython] G4_BONE_CORTICAL_ICRP  # scripted group (container) (typed FeaturePython)
  Dunit = g/cm3
  Dvalue = 1.92
  Group = -> [H_element016,C_element016,N_element011,O_element015,Na_element003,Mg_element002,P_element003,S_element005,Ca_element004]
  conduct = 2
  density = 1
  expand = 3
  formula = G4_BONE_CORTICAL_ICRP
  name = G4_BONE_CORTICAL_ICRP
  specific = 4
FEATURE [App::DocumentObjectGroupPython] B_element001  label="B_element : 4"  # scripted group (container) (typed FeaturePython)
  n = 4
  ref = B_element
FEATURE [App::DocumentObjectGroupPython] C_element017  label="C_element : 1"  # scripted group (container) (typed FeaturePython)
  n = 1
  ref = C_element
FEATURE [App::DocumentObjectGroupPython] G4_BORON_CARBIDE  # scripted group (container) (typed FeaturePython)
  Dunit = g/cm3
  Dvalue = 2.52
  Group = -> [B_element001,C_element017]
  conduct = 2
  density = 1
  expand = 3
  formula = G4_BORON_CARBIDE
  name = G4_BORON_CARBIDE
  specific = 4
FEATURE [App::DocumentObjectGroupPython] B_element002  label="B_element : 2"  # scripted group (container) (typed FeaturePython)
  n = 2
  ref = B_element
FEATURE [App::DocumentObjectGroupPython] O_element016  label="O_element : 006"  # scripted group (container) (typed FeaturePython)
  n = 3
  ref = O_element
FEATURE [App::DocumentObjectGroupPython] G4_BORON_OXIDE  # scripted group (container) (typed FeaturePython)
  Dunit = g/cm3
  Dvalue = 1.812
  Group = -> [B_element002,O_element016]
  conduct = 2
  density = 1
  expand = 3
  formula = G4_BORON_OXIDE
  name = G4_BORON_OXIDE
  specific = 4
FEATURE [App::DocumentObjectGroupPython] H_element017  label="H_element : 0.107"  # scripted group (container) (typed FeaturePython)
  n = 0.107
FEATURE [App::DocumentObjectGroupPython] C_element018  label="C_element : 0.145"  # scripted group (container) (typed FeaturePython)
  n = 0.145
FEATURE [App::DocumentObjectGroupPython] N_element012  label="N_element : 0.022"  # scripted group (container) (typed FeaturePython)
  n = 0.022
FEATURE [App::DocumentObjectGroupPython] O_element017  label="O_element : 0.712"  # scripted group (container) (typed FeaturePython)
  n = 0.712
FEATURE [App::DocumentObjectGroupPython] Na_element004  label="Na_element : 0.004"  # scripted group (container) (typed FeaturePython)
  n = 0.002
FEATURE [App::DocumentObjectGroupPython] P_element004  label="P_element : 0.004"  # scripted group (container) (typed FeaturePython)
  n = 0.004
FEATURE [App::DocumentObjectGroupPython] S_element006  label="S_element : 0.005"  # scripted group (container) (typed FeaturePython)
  n = 0.002
FEATURE [App::DocumentObjectGroupPython] Cl_element003  label="Cl_element : 0.004"  # scripted group (container) (typed FeaturePython)
  n = 0.003
FEATURE [App::DocumentObjectGroupPython] K_element002  label="K_element : 0.003"  # scripted group (container) (typed FeaturePython)
  n = 0.003
FEATURE [App::DocumentObjectGroupPython] G4_BRAIN_ICRP  # scripted group (container) (typed FeaturePython)
  Dunit = g/cm3
  Dvalue = 1.04
  Group = -> [H_element017,C_element018,N_element012,O_element017,Na_element004,P_element004,S_element006,Cl_element003,K_element002]
  conduct = 2
  density = 1
  expand = 3
  formula = G4_BRAIN_ICRP
  name = G4_BRAIN_ICRP
  specific = 4
FEATURE [App::DocumentObjectGroupPython] C_element019  label="C_element : 4"  # scripted group (container) (typed FeaturePython)
  n = 4
  ref = C_element
FEATURE [App::DocumentObjectGroupPython] H_element018  label="H_element : 010"  # scripted group (container) (typed FeaturePython)
  n = 10
  ref = H_element
FEATURE [App::DocumentObjectGroupPython] G4_BUTANE  # scripted group (container) (typed FeaturePython)
  Dunit = g/cm3
  Dvalue = 0.00249343
  Group = -> [C_element019,H_element018]
  conduct = 2
  density = 1
  expand = 3
  formula = G4_BUTANE
  name = G4_BUTANE
  specific = 4
FEATURE [App::DocumentObjectGroupPython] C_element020  label="C_element : 008"  # scripted group (container) (typed FeaturePython)
  n = 4
  ref = C_element
FEATURE [App::DocumentObjectGroupPython] H_element019  label="H_element : 011"  # scripted group (container) (typed FeaturePython)
  n = 10
  ref = H_element
FEATURE [App::DocumentObjectGroupPython] O_element018  label="O_element : 007"  # scripted group (container) (typed FeaturePython)
  n = 1
  ref = O_element
FEATURE [App::DocumentObjectGroupPython] G4_N_BUTYL_ALCOHOL  label="G4_N-BUTYL_ALCOHOL"  # scripted group (container) (typed FeaturePython)
  Dunit = g/cm3
  Dvalue = 0.8098
  Group = -> [C_element020,H_element019,O_element018]
  conduct = 2
  density = 1
  expand = 3
  formula = G4_N-BUTYL_ALCOHOL
  name = G4_N-BUTYL_ALCOHOL
  specific = 4
FEATURE [App::DocumentObjectGroupPython] H_element020  label="H_element : 0.025"  # scripted group (container) (typed FeaturePython)
  n = 0.02468
FEATURE [App::DocumentObjectGroupPython] C_element021  label="C_element : 0.502"  # scripted group (container) (typed FeaturePython)
  n = 0.501611
FEATURE [App::DocumentObjectGroupPython] O_element019  label="O_element : 0.005"  # scripted group (container) (typed FeaturePython)
  n = 0.004527
FEATURE [App::DocumentObjectGroupPython] F_element004  label="F_element : 0.465"  # scripted group (container) (typed FeaturePython)
  n = 0.465209
FEATURE [App::DocumentObjectGroupPython] Si_element001  label="Si_element : 0.004"  # scripted group (container) (typed FeaturePython)
  n = 0.003973
FEATURE [App::DocumentObjectGroupPython] G4_C_552  label="G4_C-552"  # scripted group (container) (typed FeaturePython)
  Dunit = g/cm3
  Dvalue = 1.76
  Group = -> [H_element020,C_element021,O_element019,F_element004,Si_element001]
  conduct = 2
  density = 1
  expand = 3
  formula = G4_C-552
  name = G4_C-552
  specific = 4
FEATURE [App::DocumentObjectGroupPython] Cd_element001  label="Cd_element : 1"  # scripted group (container) (typed FeaturePython)
  n = 1
  ref = Cd_element
FEATURE [App::DocumentObjectGroupPython] Te_element001  label="Te_element : 1"  # scripted group (container) (typed FeaturePython)
  n = 1
  ref = Te_element
FEATURE [App::DocumentObjectGroupPython] G4_CADMIUM_TELLURIDE  # scripted group (container) (typed FeaturePython)
  Dunit = g/cm3
  Dvalue = 6.2
  Group = -> [Cd_element001,Te_element001]
  conduct = 2
  density = 1
  expand = 3
  formula = G4_CADMIUM_TELLURIDE
  name = G4_CADMIUM_TELLURIDE
  specific = 4
FEATURE [App::DocumentObjectGroupPython] Cd_element002  label="Cd_element : 002"  # scripted group (container) (typed FeaturePython)
  n = 1
  ref = Cd_element
FEATURE [App::DocumentObjectGroupPython] W_element001  label="W_element : 1"  # scripted group (container) (typed FeaturePython)
  n = 1
  ref = W_element
FEATURE [App::DocumentObjectGroupPython] O_element020  label="O_element : 008"  # scripted group (container) (typed FeaturePython)
  n = 4
  ref = O_element
FEATURE [App::DocumentObjectGroupPython] G4_CADMIUM_TUNGSTATE  # scripted group (container) (typed FeaturePython)
  Dunit = g/cm3
  Dvalue = 7.9
  Group = -> [Cd_element002,W_element001,O_element020]
  conduct = 2
  density = 1
  expand = 3
  formula = G4_CADMIUM_TUNGSTATE
  name = G4_CADMIUM_TUNGSTATE
  specific = 4
FEATURE [App::DocumentObjectGroupPython] Ca_element005  label="Ca_element : 1"  # scripted group (container) (typed FeaturePython)
  n = 1
  ref = Ca_element
FEATURE [App::DocumentObjectGroupPython] C_element022  label="C_element : 009"  # scripted group (container) (typed FeaturePython)
  n = 1
  ref = C_element
FEATURE [App::DocumentObjectGroupPython] O_element021  label="O_element : 009"  # scripted group (container) (typed FeaturePython)
  n = 3
  ref = O_element
FEATURE [App::DocumentObjectGroupPython] G4_CALCIUM_CARBONATE  # scripted group (container) (typed FeaturePython)
  Dunit = g/cm3
  Dvalue = 2.8
  Group = -> [Ca_element005,C_element022,O_element021]
  conduct = 2
  density = 1
  expand = 3
  formula = G4_CALCIUM_CARBONATE
  name = G4_CALCIUM_CARBONATE
  specific = 4
FEATURE [App::DocumentObjectGroupPython] Ca_element006  label="Ca_element : 002"  # scripted group (container) (typed FeaturePython)
  n = 1
  ref = Ca_element
FEATURE [App::DocumentObjectGroupPython] F_element005  label="F_element : 003"  # scripted group (container) (typed FeaturePython)
  n = 2
  ref = F_element
FEATURE [App::DocumentObjectGroupPython] G4_CALCIUM_FLUORIDE  # scripted group (container) (typed FeaturePython)
  Dunit = g/cm3
  Dvalue = 3.18
  Group = -> [Ca_element006,F_element005]
  conduct = 2
  density = 1
  expand = 3
  formula = G4_CALCIUM_FLUORIDE
  name = G4_CALCIUM_FLUORIDE
  specific = 4
FEATURE [App::DocumentObjectGroupPython] Ca_element007  label="Ca_element : 003"  # scripted group (container) (typed FeaturePython)
  n = 1
  ref = Ca_element
FEATURE [App::DocumentObjectGroupPython] O_element022  label="O_element : 010"  # scripted group (container) (typed FeaturePython)
  n = 1
  ref = O_element
FEATURE [App::DocumentObjectGroupPython] G4_CALCIUM_OXIDE  # scripted group (container) (typed FeaturePython)
  Dunit = g/cm3
  Dvalue = 3.3
  Group = -> [Ca_element007,O_element022]
  conduct = 2
  density = 1
  expand = 3
  formula = G4_CALCIUM_OXIDE
  name = G4_CALCIUM_OXIDE
  specific = 4
FEATURE [App::DocumentObjectGroupPython] Ca_element008  label="Ca_element : 004"  # scripted group (container) (typed FeaturePython)
  n = 1
  ref = Ca_element
FEATURE [App::DocumentObjectGroupPython] S_element007  label="S_element : 002"  # scripted group (container) (typed FeaturePython)
  n = 1
  ref = S_element
FEATURE [App::DocumentObjectGroupPython] O_element023  label="O_element : 011"  # scripted group (container) (typed FeaturePython)
  n = 4
  ref = O_element
FEATURE [App::DocumentObjectGroupPython] G4_CALCIUM_SULFATE  # scripted group (container) (typed FeaturePython)
  Dunit = g/cm3
  Dvalue = 2.96
  Group = -> [Ca_element008,S_element007,O_element023]
  conduct = 2
  density = 1
  expand = 3
  formula = G4_CALCIUM_SULFATE
  name = G4_CALCIUM_SULFATE
  specific = 4
FEATURE [App::DocumentObjectGroupPython] Ca_element009  label="Ca_element : 005"  # scripted group (container) (typed FeaturePython)
  n = 1
  ref = Ca_element
FEATURE [App::DocumentObjectGroupPython] W_element002  label="W_element : 002"  # scripted group (container) (typed FeaturePython)
  n = 1
  ref = W_element
FEATURE [App::DocumentObjectGroupPython] O_element024  label="O_element : 012"  # scripted group (container) (typed FeaturePython)
  n = 4
  ref = O_element
FEATURE [App::DocumentObjectGroupPython] G4_CALCIUM_TUNGSTATE  # scripted group (container) (typed FeaturePython)
  Dunit = g/cm3
  Dvalue = 6.062
  Group = -> [Ca_element009,W_element002,O_element024]
  conduct = 2
  density = 1
  expand = 3
  formula = G4_CALCIUM_TUNGSTATE
  name = G4_CALCIUM_TUNGSTATE
  specific = 4
FEATURE [App::DocumentObjectGroupPython] C_element023  label="C_element : 010"  # scripted group (container) (typed FeaturePython)
  n = 1
  ref = C_element
FEATURE [App::DocumentObjectGroupPython] O_element025  label="O_element : 013"  # scripted group (container) (typed FeaturePython)
  n = 2
  ref = O_element
FEATURE [App::DocumentObjectGroupPython] G4_CARBON_DIOXIDE  # scripted group (container) (typed FeaturePython)
  Dunit = g/cm3
  Dvalue = 0.00184212
  Group = -> [C_element023,O_element025]
  conduct = 2
  density = 1
  expand = 3
  formula = G4_CARBON_DIOXIDE
  name = G4_CARBON_DIOXIDE
  specific = 4
FEATURE [App::DocumentObjectGroupPython] C_element024  label="C_element : 011"  # scripted group (container) (typed FeaturePython)
  n = 1
  ref = C_element
FEATURE [App::DocumentObjectGroupPython] Cl_element004  label="Cl_element : 4"  # scripted group (container) (typed FeaturePython)
  n = 4
  ref = Cl_element
FEATURE [App::DocumentObjectGroupPython] G4_CARBON_TETRACHLORIDE  # scripted group (container) (typed FeaturePython)
  Dunit = g/cm3
  Dvalue = 1.594
  Group = -> [C_element024,Cl_element004]
  conduct = 2
  density = 1
  expand = 3
  formula = G4_CARBON_TETRACHLORIDE
  name = G4_CARBON_TETRACHLORIDE
  specific = 4
FEATURE [App::DocumentObjectGroupPython] C_element025  label="C_element : 012"  # scripted group (container) (typed FeaturePython)
  n = 6
  ref = C_element
FEATURE [App::DocumentObjectGroupPython] H_element021  label="H_element : 012"  # scripted group (container) (typed FeaturePython)
  n = 10
  ref = H_element
FEATURE [App::DocumentObjectGroupPython] O_element026  label="O_element : 5"  # scripted group (container) (typed FeaturePython)
  n = 5
  ref = O_element
FEATURE [App::DocumentObjectGroupPython] G4_CELLULOSE_CELLOPHANE  # scripted group (container) (typed FeaturePython)
  Dunit = g/cm3
  Dvalue = 1.42
  Group = -> [C_element025,H_element021,O_element026]
  conduct = 2
  density = 1
  expand = 3
  formula = G4_CELLULOSE_CELLOPHANE
  name = G4_CELLULOSE_CELLOPHANE
  specific = 4
FEATURE [App::DocumentObjectGroupPython] H_element022  label="H_element : 0.067"  # scripted group (container) (typed FeaturePython)
  n = 0.067125
FEATURE [App::DocumentObjectGroupPython] C_element026  label="C_element : 0.545"  # scripted group (container) (typed FeaturePython)
  n = 0.545403
FEATURE [App::DocumentObjectGroupPython] O_element027  label="O_element : 0.387"  # scripted group (container) (typed FeaturePython)
  n = 0.387472
FEATURE [App::DocumentObjectGroupPython] G4_CELLULOSE_BUTYRATE  # scripted group (container) (typed FeaturePython)
  Dunit = g/cm3
  Dvalue = 1.2
  Group = -> [H_element022,C_element026,O_element027]
  conduct = 2
  density = 1
  expand = 3
  formula = G4_CELLULOSE_BUTYRATE
  name = G4_CELLULOSE_BUTYRATE
  specific = 4
FEATURE [App::DocumentObjectGroupPython] H_element023  label="H_element : 0.029"  # scripted group (container) (typed FeaturePython)
  n = 0.029216
FEATURE [App::DocumentObjectGroupPython] C_element027  label="C_element : 0.271"  # scripted group (container) (typed FeaturePython)
  n = 0.271296
FEATURE [App::DocumentObjectGroupPython] N_element013  label="N_element : 0.121"  # scripted group (container) (typed FeaturePython)
  n = 0.121276
FEATURE [App::DocumentObjectGroupPython] O_element028  label="O_element : 0.578"  # scripted group (container) (typed FeaturePython)
  n = 0.578212
FEATURE [App::DocumentObjectGroupPython] G4_CELLULOSE_NITRATE  # scripted group (container) (typed FeaturePython)
  Dunit = g/cm3
  Dvalue = 1.49
  Group = -> [H_element023,C_element027,N_element013,O_element028]
  conduct = 2
  density = 1
  expand = 3
  formula = G4_CELLULOSE_NITRATE
  name = G4_CELLULOSE_NITRATE
  specific = 4
FEATURE [App::DocumentObjectGroupPython] H_element024  label="H_element : 0.108"  # scripted group (container) (typed FeaturePython)
  n = 0.107596
FEATURE [App::DocumentObjectGroupPython] N_element014  label="N_element : 0.001"  # scripted group (container) (typed FeaturePython)
  n = 0.0008
FEATURE [App::DocumentObjectGroupPython] O_element029  label="O_element : 0.875"  # scripted group (container) (typed FeaturePython)
  n = 0.874976
FEATURE [App::DocumentObjectGroupPython] S_element008  label="S_element : 0.015"  # scripted group (container) (typed FeaturePython)
  n = 0.014627
FEATURE [App::DocumentObjectGroupPython] Ce_element001  label="Ce_element : 0.002"  # scripted group (container) (typed FeaturePython)
  n = 0.002001
FEATURE [App::DocumentObjectGroupPython] G4_CERIC_SULFATE  # scripted group (container) (typed FeaturePython)
  Dunit = g/cm3
  Dvalue = 1.03
  Group = -> [H_element024,N_element014,O_element029,S_element008,Ce_element001]
  conduct = 2
  density = 1
  expand = 3
  formula = G4_CERIC_SULFATE
  name = G4_CERIC_SULFATE
  specific = 4
FEATURE [App::DocumentObjectGroupPython] Cs_element001  label="Cs_element : 1"  # scripted group (container) (typed FeaturePython)
  n = 1
  ref = Cs_element
FEATURE [App::DocumentObjectGroupPython] F_element006  label="F_element : 1"  # scripted group (container) (typed FeaturePython)
  n = 1
  ref = F_element
FEATURE [App::DocumentObjectGroupPython] G4_CESIUM_FLUORIDE  # scripted group (container) (typed FeaturePython)
  Dunit = g/cm3
  Dvalue = 4.115
  Group = -> [Cs_element001,F_element006]
  conduct = 2
  density = 1
  expand = 3
  formula = G4_CESIUM_FLUORIDE
  name = G4_CESIUM_FLUORIDE
  specific = 4
FEATURE [App::DocumentObjectGroupPython] Cs_element002  label="Cs_element : 002"  # scripted group (container) (typed FeaturePython)
  n = 1
  ref = Cs_element
FEATURE [App::DocumentObjectGroupPython] I_element001  label="I_element : 1"  # scripted group (container) (typed FeaturePython)
  n = 1
  ref = I_element
FEATURE [App::DocumentObjectGroupPython] G4_CESIUM_IODIDE  # scripted group (container) (typed FeaturePython)
  Dunit = g/cm3
  Dvalue = 4.51
  Group = -> [Cs_element002,I_element001]
  conduct = 2
  density = 1
  expand = 3
  formula = G4_CESIUM_IODIDE
  name = G4_CESIUM_IODIDE
  specific = 4
FEATURE [App::DocumentObjectGroupPython] C_element028  label="C_element : 013"  # scripted group (container) (typed FeaturePython)
  n = 6
  ref = C_element
FEATURE [App::DocumentObjectGroupPython] H_element025  label="H_element : 013"  # scripted group (container) (typed FeaturePython)
  n = 5
  ref = H_element
FEATURE [App::DocumentObjectGroupPython] Cl_element005  label="Cl_element : 1"  # scripted group (container) (typed FeaturePython)
  n = 1
  ref = Cl_element
FEATURE [App::DocumentObjectGroupPython] G4_CHLOROBENZENE  # scripted group (container) (typed FeaturePython)
  Dunit = g/cm3
  Dvalue = 1.1058
  Group = -> [C_element028,H_element025,Cl_element005]
  conduct = 2
  density = 1
  expand = 3
  formula = G4_CHLOROBENZENE
  name = G4_CHLOROBENZENE
  specific = 4
FEATURE [App::DocumentObjectGroupPython] C_element029  label="C_element : 014"  # scripted group (container) (typed FeaturePython)
  n = 1
  ref = C_element
FEATURE [App::DocumentObjectGroupPython] H_element026  label="H_element : 1"  # scripted group (container) (typed FeaturePython)
  n = 1
  ref = H_element
FEATURE [App::DocumentObjectGroupPython] Cl_element006  label="Cl_element : 3"  # scripted group (container) (typed FeaturePython)
  n = 3
  ref = Cl_element
FEATURE [App::DocumentObjectGroupPython] G4_CHLOROFORM  # scripted group (container) (typed FeaturePython)
  Dunit = g/cm3
  Dvalue = 1.4832
  Group = -> [C_element029,H_element026,Cl_element006]
  conduct = 2
  density = 1
  expand = 3
  formula = G4_CHLOROFORM
  name = G4_CHLOROFORM
  specific = 4
FEATURE [App::DocumentObjectGroupPython] H_element027  label="H_element : 0.010"  # scripted group (container) (typed FeaturePython)
  n = 0.01
FEATURE [App::DocumentObjectGroupPython] C_element030  label="C_element : 0.001"  # scripted group (container) (typed FeaturePython)
  n = 0.001
FEATURE [App::DocumentObjectGroupPython] O_element030  label="O_element : 0.529"  # scripted group (container) (typed FeaturePython)
  n = 0.529107
FEATURE [App::DocumentObjectGroupPython] Na_element005  label="Na_element : 0.016"  # scripted group (container) (typed FeaturePython)
  n = 0.016
FEATURE [App::DocumentObjectGroupPython] Mg_element003  label="Mg_element : 0.004"  # scripted group (container) (typed FeaturePython)
  n = 0.002
FEATURE [App::DocumentObjectGroupPython] Al_element002  label="Al_element : 0.034"  # scripted group (container) (typed FeaturePython)
  n = 0.033872
FEATURE [App::DocumentObjectGroupPython] Si_element002  label="Si_element : 0.337"  # scripted group (container) (typed FeaturePython)
  n = 0.337021
FEATURE [App::DocumentObjectGroupPython] K_element003  label="K_element : 0.013"  # scripted group (container) (typed FeaturePython)
  n = 0.013
FEATURE [App::DocumentObjectGroupPython] Ca_element010  label="Ca_element : 0.044"  # scripted group (container) (typed FeaturePython)
  n = 0.044
FEATURE [App::DocumentObjectGroupPython] Fe_element002  label="Fe_element : 0.014"  # scripted group (container) (typed FeaturePython)
  n = 0.014
FEATURE [App::DocumentObjectGroupPython] G4_CONCRETE  # scripted group (container) (typed FeaturePython)
  Dunit = g/cm3
  Dvalue = 2.3
  Group = -> [H_element027,C_element030,O_element030,Na_element005,Mg_element003,Al_element002,Si_element002,K_element003,Ca_element010,Fe_element002]
  conduct = 2
  density = 1
  expand = 3
  formula = G4_CONCRETE
  name = G4_CONCRETE
  specific = 4
FEATURE [App::DocumentObjectGroupPython] C_element031  label="C_element : 015"  # scripted group (container) (typed FeaturePython)
  n = 6
  ref = C_element
FEATURE [App::DocumentObjectGroupPython] H_element028  label="H_element : 12"  # scripted group (container) (typed FeaturePython)
  n = 12
  ref = H_element
FEATURE [App::DocumentObjectGroupPython] G4_CYCLOHEXANE  # scripted group (container) (typed FeaturePython)
  Dunit = g/cm3
  Dvalue = 0.779
  Group = -> [C_element031,H_element028]
  conduct = 2
  density = 1
  expand = 3
  formula = G4_CYCLOHEXANE
  name = G4_CYCLOHEXANE
  specific = 4
FEATURE [App::DocumentObjectGroupPython] C_element032  label="C_element : 016"  # scripted group (container) (typed FeaturePython)
  n = 6
  ref = C_element
FEATURE [App::DocumentObjectGroupPython] H_element029  label="H_element : 4"  # scripted group (container) (typed FeaturePython)
  n = 4
  ref = H_element
FEATURE [App::DocumentObjectGroupPython] Cl_element007  label="Cl_element : 2"  # scripted group (container) (typed FeaturePython)
  n = 2
  ref = Cl_element
FEATURE [App::DocumentObjectGroupPython] G4_1_2_DICHLOROBENZENE  label="G4_1.2-DICHLOROBENZENE"  # scripted group (container) (typed FeaturePython)
  Dunit = g/cm3
  Dvalue = 1.3048
  Group = -> [C_element032,H_element029,Cl_element007]
  conduct = 2
  density = 1
  expand = 3
  formula = G4_1.2-DICHLOROBENZENE
  name = G4_1.2-DICHLOROBENZENE
  specific = 4
FEATURE [App::DocumentObjectGroupPython] C_element033  label="C_element : 017"  # scripted group (container) (typed FeaturePython)
  n = 4
  ref = C_element
FEATURE [App::DocumentObjectGroupPython] H_element030  label="H_element : 8"  # scripted group (container) (typed FeaturePython)
  n = 8
  ref = H_element
FEATURE [App::DocumentObjectGroupPython] O_element031  label="O_element : 014"  # scripted group (container) (typed FeaturePython)
  n = 1
  ref = O_element
FEATURE [App::DocumentObjectGroupPython] Cl_element008  label="Cl_element : 005"  # scripted group (container) (typed FeaturePython)
  n = 2
  ref = Cl_element
FEATURE [App::DocumentObjectGroupPython] G4_DICHLORODIETHYL_ETHER  # scripted group (container) (typed FeaturePython)
  Dunit = g/cm3
  Dvalue = 1.2199
  Group = -> [C_element033,H_element030,O_element031,Cl_element008]
  conduct = 2
  density = 1
  expand = 3
  formula = G4_DICHLORODIETHYL_ETHER
  name = G4_DICHLORODIETHYL_ETHER
  specific = 4
FEATURE [App::DocumentObjectGroupPython] C_element034  label="C_element : 018"  # scripted group (container) (typed FeaturePython)
  n = 2
  ref = C_element
FEATURE [App::DocumentObjectGroupPython] H_element031  label="H_element : 014"  # scripted group (container) (typed FeaturePython)
  n = 4
  ref = H_element
FEATURE [App::DocumentObjectGroupPython] Cl_element009  label="Cl_element : 006"  # scripted group (container) (typed FeaturePython)
  n = 2
  ref = Cl_element
FEATURE [App::DocumentObjectGroupPython] G4_1_2_DICHLOROETHANE  label="G4_1.2-DICHLOROETHANE"  # scripted group (container) (typed FeaturePython)
  Dunit = g/cm3
  Dvalue = 1.2351
  Group = -> [C_element034,H_element031,Cl_element009]
  conduct = 2
  density = 1
  expand = 3
  formula = G4_1.2-DICHLOROETHANE
  name = G4_1.2-DICHLOROETHANE
  specific = 4
FEATURE [App::DocumentObjectGroupPython] C_element035  label="C_element : 019"  # scripted group (container) (typed FeaturePython)
  n = 4
  ref = C_element
FEATURE [App::DocumentObjectGroupPython] H_element032  label="H_element : 015"  # scripted group (container) (typed FeaturePython)
  n = 10
  ref = H_element
FEATURE [App::DocumentObjectGroupPython] O_element032  label="O_element : 015"  # scripted group (container) (typed FeaturePython)
  n = 1
  ref = O_element
FEATURE [App::DocumentObjectGroupPython] G4_DIETHYL_ETHER  # scripted group (container) (typed FeaturePython)
  Dunit = g/cm3
  Dvalue = 0.71378
  Group = -> [C_element035,H_element032,O_element032]
  conduct = 2
  density = 1
  expand = 3
  formula = G4_DIETHYL_ETHER
  name = G4_DIETHYL_ETHER
  specific = 4
FEATURE [App::DocumentObjectGroupPython] C_element036  label="C_element : 020"  # scripted group (container) (typed FeaturePython)
  n = 3
  ref = C_element
FEATURE [App::DocumentObjectGroupPython] H_element033  label="H_element : 016"  # scripted group (container) (typed FeaturePython)
  n = 7
  ref = H_element
FEATURE [App::DocumentObjectGroupPython] N_element015  label="N_element : 008"  # scripted group (container) (typed FeaturePython)
  n = 1
  ref = N_element
FEATURE [App::DocumentObjectGroupPython] O_element033  label="O_element : 016"  # scripted group (container) (typed FeaturePython)
  n = 1
  ref = O_element
FEATURE [App::DocumentObjectGroupPython] G4_N_N_DIMETHYL_FORMAMIDE  label="G4_N.N-DIMETHYL_FORMAMIDE"  # scripted group (container) (typed FeaturePython)
  Dunit = g/cm3
  Dvalue = 0.9487
  Group = -> [C_element036,H_element033,N_element015,O_element033]
  conduct = 2
  density = 1
  expand = 3
  formula = G4_N.N-DIMETHYL_FORMAMIDE
  name = G4_N.N-DIMETHYL_FORMAMIDE
  specific = 4
FEATURE [App::DocumentObjectGroupPython] C_element037  label="C_element : 021"  # scripted group (container) (typed FeaturePython)
  n = 2
  ref = C_element
FEATURE [App::DocumentObjectGroupPython] H_element034  label="H_element : 017"  # scripted group (container) (typed FeaturePython)
  n = 6
  ref = H_element
FEATURE [App::DocumentObjectGroupPython] O_element034  label="O_element : 017"  # scripted group (container) (typed FeaturePython)
  n = 1
  ref = O_element
FEATURE [App::DocumentObjectGroupPython] S_element009  label="S_element : 003"  # scripted group (container) (typed FeaturePython)
  n = 1
  ref = S_element
FEATURE [App::DocumentObjectGroupPython] G4_DIMETHYL_SULFOXIDE  # scripted group (container) (typed FeaturePython)
  Dunit = g/cm3
  Dvalue = 1.1014
  Group = -> [C_element037,H_element034,O_element034,S_element009]
  conduct = 2
  density = 1
  expand = 3
  formula = G4_DIMETHYL_SULFOXIDE
  name = G4_DIMETHYL_SULFOXIDE
  specific = 4
FEATURE [App::DocumentObjectGroupPython] C_element038  label="C_element : 022"  # scripted group (container) (typed FeaturePython)
  n = 2
  ref = C_element
FEATURE [App::DocumentObjectGroupPython] H_element035  label="H_element : 018"  # scripted group (container) (typed FeaturePython)
  n = 6
  ref = H_element
FEATURE [App::DocumentObjectGroupPython] G4_ETHANE  # scripted group (container) (typed FeaturePython)
  Dunit = g/cm3
  Dvalue = 0.00125324
  Group = -> [C_element038,H_element035]
  conduct = 2
  density = 1
  expand = 3
  formula = G4_ETHANE
  name = G4_ETHANE
  specific = 4
FEATURE [App::DocumentObjectGroupPython] C_element039  label="C_element : 023"  # scripted group (container) (typed FeaturePython)
  n = 2
  ref = C_element
FEATURE [App::DocumentObjectGroupPython] H_element036  label="H_element : 019"  # scripted group (container) (typed FeaturePython)
  n = 6
  ref = H_element
FEATURE [App::DocumentObjectGroupPython] O_element035  label="O_element : 018"  # scripted group (container) (typed FeaturePython)
  n = 1
  ref = O_element
FEATURE [App::DocumentObjectGroupPython] G4_ETHYL_ALCOHOL  # scripted group (container) (typed FeaturePython)
  Dunit = g/cm3
  Dvalue = 0.7893
  Group = -> [C_element039,H_element036,O_element035]
  conduct = 2
  density = 1
  expand = 3
  formula = G4_ETHYL_ALCOHOL
  name = G4_ETHYL_ALCOHOL
  specific = 4
FEATURE [App::DocumentObjectGroupPython] H_element037  label="H_element : 0.090"  # scripted group (container) (typed FeaturePython)
  n = 0.090027
FEATURE [App::DocumentObjectGroupPython] C_element040  label="C_element : 0.585"  # scripted group (container) (typed FeaturePython)
  n = 0.585182
FEATURE [App::DocumentObjectGroupPython] O_element036  label="O_element : 0.325"  # scripted group (container) (typed FeaturePython)
  n = 0.324791
FEATURE [App::DocumentObjectGroupPython] G4_ETHYL_CELLULOSE  # scripted group (container) (typed FeaturePython)
  Dunit = g/cm3
  Dvalue = 1.13
  Group = -> [H_element037,C_element040,O_element036]
  conduct = 2
  density = 1
  expand = 3
  formula = G4_ETHYL_CELLULOSE
  name = G4_ETHYL_CELLULOSE
  specific = 4
FEATURE [App::DocumentObjectGroupPython] C_element041  label="C_element : 024"  # scripted group (container) (typed FeaturePython)
  n = 2
  ref = C_element
FEATURE [App::DocumentObjectGroupPython] H_element038  label="H_element : 020"  # scripted group (container) (typed FeaturePython)
  n = 4
  ref = H_element
FEATURE [App::DocumentObjectGroupPython] G4_ETHYLENE  # scripted group (container) (typed FeaturePython)
  Dunit = g/cm3
  Dvalue = 0.00117497
  Group = -> [C_element041,H_element038]
  conduct = 2
  density = 1
  expand = 3
  formula = G4_ETHYLENE
  name = G4_ETHYLENE
  specific = 4
FEATURE [App::DocumentObjectGroupPython] H_element039  label="H_element : 0.096"  # scripted group (container) (typed FeaturePython)
  n = 0.096
FEATURE [App::DocumentObjectGroupPython] C_element042  label="C_element : 0.195"  # scripted group (container) (typed FeaturePython)
  n = 0.195
FEATURE [App::DocumentObjectGroupPython] N_element016  label="N_element : 0.057"  # scripted group (container) (typed FeaturePython)
  n = 0.057
FEATURE [App::DocumentObjectGroupPython] O_element037  label="O_element : 0.646"  # scripted group (container) (typed FeaturePython)
  n = 0.646
FEATURE [App::DocumentObjectGroupPython] Na_element006  label="Na_element : 0.017"  # scripted group (container) (typed FeaturePython)
  n = 0.001
FEATURE [App::DocumentObjectGroupPython] P_element005  label="P_element : 0.104"  # scripted group (container) (typed FeaturePython)
  n = 0.001
FEATURE [App::DocumentObjectGroupPython] S_element010  label="S_element : 0.016"  # scripted group (container) (typed FeaturePython)
  n = 0.003
FEATURE [App::DocumentObjectGroupPython] Cl_element010  label="Cl_element : 0.005"  # scripted group (container) (typed FeaturePython)
  n = 0.001
FEATURE [App::DocumentObjectGroupPython] G4_EYE_LENS_ICRP  # scripted group (container) (typed FeaturePython)
  Dunit = g/cm3
  Dvalue = 1.07
  Group = -> [H_element039,C_element042,N_element016,O_element037,Na_element006,P_element005,S_element010,Cl_element010]
  conduct = 2
  density = 1
  expand = 3
  formula = G4_EYE_LENS_ICRP
  name = G4_EYE_LENS_ICRP
  specific = 4
FEATURE [App::DocumentObjectGroupPython] Fe_element003  label="Fe_element : 2"  # scripted group (container) (typed FeaturePython)
  n = 2
  ref = Fe_element
FEATURE [App::DocumentObjectGroupPython] O_element038  label="O_element : 019"  # scripted group (container) (typed FeaturePython)
  n = 3
  ref = O_element
FEATURE [App::DocumentObjectGroupPython] G4_FERRIC_OXIDE  # scripted group (container) (typed FeaturePython)
  Dunit = g/cm3
  Dvalue = 5.2
  Group = -> [Fe_element003,O_element038]
  conduct = 2
  density = 1
  expand = 3
  formula = G4_FERRIC_OXIDE
  name = G4_FERRIC_OXIDE
  specific = 4
FEATURE [App::DocumentObjectGroupPython] Fe_element004  label="Fe_element : 1"  # scripted group (container) (typed FeaturePython)
  n = 1
  ref = Fe_element
FEATURE [App::DocumentObjectGroupPython] B_element003  label="B_element : 1"  # scripted group (container) (typed FeaturePython)
  n = 1
  ref = B_element
FEATURE [App::DocumentObjectGroupPython] G4_FERROBORIDE  # scripted group (container) (typed FeaturePython)
  Dunit = g/cm3
  Dvalue = 7.15
  Group = -> [Fe_element004,B_element003]
  conduct = 2
  density = 1
  expand = 3
  formula = G4_FERROBORIDE
  name = G4_FERROBORIDE
  specific = 4
FEATURE [App::DocumentObjectGroupPython] Fe_element005  label="Fe_element : 003"  # scripted group (container) (typed FeaturePython)
  n = 1
  ref = Fe_element
FEATURE [App::DocumentObjectGroupPython] O_element039  label="O_element : 020"  # scripted group (container) (typed FeaturePython)
  n = 1
  ref = O_element
FEATURE [App::DocumentObjectGroupPython] G4_FERROUS_OXIDE  # scripted group (container) (typed FeaturePython)
  Dunit = g/cm3
  Dvalue = 5.7
  Group = -> [Fe_element005,O_element039]
  conduct = 2
  density = 1
  expand = 3
  formula = G4_FERROUS_OXIDE
  name = G4_FERROUS_OXIDE
  specific = 4
FEATURE [App::DocumentObjectGroupPython] H_element040  label="H_element : 0.115"  # scripted group (container) (typed FeaturePython)
  n = 0.108259
FEATURE [App::DocumentObjectGroupPython] N_element017  label="N_element : 0.000"  # scripted group (container) (typed FeaturePython)
  n = 2.7e-05
FEATURE [App::DocumentObjectGroupPython] O_element040  label="O_element : 0.879"  # scripted group (container) (typed FeaturePython)
  n = 0.878636
FEATURE [App::DocumentObjectGroupPython] Na_element007  label="Na_element : 0.000"  # scripted group (container) (typed FeaturePython)
  n = 2.2e-05
FEATURE [App::DocumentObjectGroupPython] S_element011  label="S_element : 0.013"  # scripted group (container) (typed FeaturePython)
  n = 0.012968
FEATURE [App::DocumentObjectGroupPython] Cl_element011  label="Cl_element : 0.000"  # scripted group (container) (typed FeaturePython)
  n = 3.4e-05
FEATURE [App::DocumentObjectGroupPython] Fe_element006  label="Fe_element : 0.000"  # scripted group (container) (typed FeaturePython)
  n = 5.4e-05
FEATURE [App::DocumentObjectGroupPython] G4_FERROUS_SULFATE  # scripted group (container) (typed FeaturePython)
  Dunit = g/cm3
  Dvalue = 1.024
  Group = -> [H_element040,N_element017,O_element040,Na_element007,S_element011,Cl_element011,Fe_element006]
  conduct = 2
  density = 1
  expand = 3
  formula = G4_FERROUS_SULFATE
  name = G4_FERROUS_SULFATE
  specific = 4
FEATURE [App::DocumentObjectGroupPython] C_element043  label="C_element : 0.099"  # scripted group (container) (typed FeaturePython)
  n = 0.099335
FEATURE [App::DocumentObjectGroupPython] F_element007  label="F_element : 0.314"  # scripted group (container) (typed FeaturePython)
  n = 0.314247
FEATURE [App::DocumentObjectGroupPython] Cl_element012  label="Cl_element : 0.586"  # scripted group (container) (typed FeaturePython)
  n = 0.586418
FEATURE [App::DocumentObjectGroupPython] G4_FREON_12  label="G4_FREON-12"  # scripted group (container) (typed FeaturePython)
  Dunit = g/cm3
  Dvalue = 1.12
  Group = -> [C_element043,F_element007,Cl_element012]
  conduct = 2
  density = 1
  expand = 3
  formula = G4_FREON-12
  name = G4_FREON-12
  specific = 4
FEATURE [App::DocumentObjectGroupPython] C_element044  label="C_element : 0.057"  # scripted group (container) (typed FeaturePython)
  n = 0.057245
FEATURE [App::DocumentObjectGroupPython] F_element008  label="F_element : 0.181"  # scripted group (container) (typed FeaturePython)
  n = 0.181096
FEATURE [App::DocumentObjectGroupPython] Br_element001  label="Br_element : 0.762"  # scripted group (container) (typed FeaturePython)
  n = 0.761659
FEATURE [App::DocumentObjectGroupPython] G4_FREON_12B2  label="G4_FREON-12B2"  # scripted group (container) (typed FeaturePython)
  Dunit = g/cm3
  Dvalue = 1.8
  Group = -> [C_element044,F_element008,Br_element001]
  conduct = 2
  density = 1
  expand = 3
  formula = G4_FREON-12B2
  name = G4_FREON-12B2
  specific = 4
FEATURE [App::DocumentObjectGroupPython] C_element045  label="C_element : 0.115"  # scripted group (container) (typed FeaturePython)
  n = 0.114983
FEATURE [App::DocumentObjectGroupPython] F_element009  label="F_element : 0.546"  # scripted group (container) (typed FeaturePython)
  n = 0.545621
FEATURE [App::DocumentObjectGroupPython] Cl_element013  label="Cl_element : 0.339"  # scripted group (container) (typed FeaturePython)
  n = 0.339396
FEATURE [App::DocumentObjectGroupPython] G4_FREON_13  label="G4_FREON-13"  # scripted group (container) (typed FeaturePython)
  Dunit = g/cm3
  Dvalue = 0.95
  Group = -> [C_element045,F_element009,Cl_element013]
  conduct = 2
  density = 1
  expand = 3
  formula = G4_FREON-13
  name = G4_FREON-13
  specific = 4
FEATURE [App::DocumentObjectGroupPython] C_element046  label="C_element : 025"  # scripted group (container) (typed FeaturePython)
  n = 1
  ref = C_element
FEATURE [App::DocumentObjectGroupPython] F_element010  label="F_element : 3"  # scripted group (container) (typed FeaturePython)
  n = 3
  ref = F_element
FEATURE [App::DocumentObjectGroupPython] Br_element002  label="Br_element : 1"  # scripted group (container) (typed FeaturePython)
  n = 1
  ref = Br_element
FEATURE [App::DocumentObjectGroupPython] G4_FREON_13B1  label="G4_FREON-13B1"  # scripted group (container) (typed FeaturePython)
  Dunit = g/cm3
  Dvalue = 1.5
  Group = -> [C_element046,F_element010,Br_element002]
  conduct = 2
  density = 1
  expand = 3
  formula = G4_FREON-13B1
  name = G4_FREON-13B1
  specific = 4
FEATURE [App::DocumentObjectGroupPython] C_element047  label="C_element : 0.061"  # scripted group (container) (typed FeaturePython)
  n = 0.061309
FEATURE [App::DocumentObjectGroupPython] F_element011  label="F_element : 0.291"  # scripted group (container) (typed FeaturePython)
  n = 0.290924
FEATURE [App::DocumentObjectGroupPython] I_element002  label="I_element : 0.648"  # scripted group (container) (typed FeaturePython)
  n = 0.647767
FEATURE [App::DocumentObjectGroupPython] G4_FREON_13I1  label="G4_FREON-13I1"  # scripted group (container) (typed FeaturePython)
  Dunit = g/cm3
  Dvalue = 1.8
  Group = -> [C_element047,F_element011,I_element002]
  conduct = 2
  density = 1
  expand = 3
  formula = G4_FREON-13I1
  name = G4_FREON-13I1
  specific = 4
FEATURE [App::DocumentObjectGroupPython] Gd_element001  label="Gd_element : 2"  # scripted group (container) (typed FeaturePython)
  n = 2
  ref = Gd_element
FEATURE [App::DocumentObjectGroupPython] O_element041  label="O_element : 021"  # scripted group (container) (typed FeaturePython)
  n = 2
  ref = O_element
FEATURE [App::DocumentObjectGroupPython] S_element012  label="S_element : 004"  # scripted group (container) (typed FeaturePython)
  n = 1
  ref = S_element
FEATURE [App::DocumentObjectGroupPython] G4_GADOLINIUM_OXYSULFIDE  # scripted group (container) (typed FeaturePython)
  Dunit = g/cm3
  Dvalue = 7.44
  Group = -> [Gd_element001,O_element041,S_element012]
  conduct = 2
  density = 1
  expand = 3
  formula = G4_GADOLINIUM_OXYSULFIDE
  name = G4_GADOLINIUM_OXYSULFIDE
  specific = 4
FEATURE [App::DocumentObjectGroupPython] Ga_element001  label="Ga_element : 1"  # scripted group (container) (typed FeaturePython)
  n = 1
  ref = Ga_element
FEATURE [App::DocumentObjectGroupPython] As_element001  label="As_element : 1"  # scripted group (container) (typed FeaturePython)
  n = 1
  ref = As_element
FEATURE [App::DocumentObjectGroupPython] G4_GALLIUM_ARSENIDE  # scripted group (container) (typed FeaturePython)
  Dunit = g/cm3
  Dvalue = 5.31
  Group = -> [Ga_element001,As_element001]
  conduct = 2
  density = 1
  expand = 3
  formula = G4_GALLIUM_ARSENIDE
  name = G4_GALLIUM_ARSENIDE
  specific = 4
FEATURE [App::DocumentObjectGroupPython] H_element041  label="H_element : 0.081"  # scripted group (container) (typed FeaturePython)
  n = 0.08118
FEATURE [App::DocumentObjectGroupPython] C_element048  label="C_element : 0.416"  # scripted group (container) (typed FeaturePython)
  n = 0.41606
FEATURE [App::DocumentObjectGroupPython] N_element018  label="N_element : 0.111"  # scripted group (container) (typed FeaturePython)
  n = 0.11124
FEATURE [App::DocumentObjectGroupPython] O_element042  label="O_element : 0.381"  # scripted group (container) (typed FeaturePython)
  n = 0.38064
FEATURE [App::DocumentObjectGroupPython] S_element013  label="S_element : 0.011"  # scripted group (container) (typed FeaturePython)
  n = 0.01088
FEATURE [App::DocumentObjectGroupPython] G4_GEL_PHOTO_EMULSION  # scripted group (container) (typed FeaturePython)
  Dunit = g/cm3
  Dvalue = 1.2914
  Group = -> [H_element041,C_element048,N_element018,O_element042,S_element013]
  conduct = 2
  density = 1
  expand = 3
  formula = G4_GEL_PHOTO_EMULSION
  name = G4_GEL_PHOTO_EMULSION
  specific = 4
FEATURE [App::DocumentObjectGroupPython] B_element004  label="B_element : 0.040"  # scripted group (container) (typed FeaturePython)
  n = 0.0400639
FEATURE [App::DocumentObjectGroupPython] O_element043  label="O_element : 0.540"  # scripted group (container) (typed FeaturePython)
  n = 0.539561
FEATURE [App::DocumentObjectGroupPython] Na_element008  label="Na_element : 0.028"  # scripted group (container) (typed FeaturePython)
  n = 0.0281909
FEATURE [App::DocumentObjectGroupPython] Al_element003  label="Al_element : 0.012"  # scripted group (container) (typed FeaturePython)
  n = 0.011644
FEATURE [App::DocumentObjectGroupPython] Si_element003  label="Si_element : 0.377"  # scripted group (container) (typed FeaturePython)
  n = 0.377219
FEATURE [App::DocumentObjectGroupPython] K_element004  label="K_element : 0.014"  # scripted group (container) (typed FeaturePython)
  n = 0.00332099
FEATURE [App::DocumentObjectGroupPython] G4_Pyrex_Glass  # scripted group (container) (typed FeaturePython)
  Dunit = g/cm3
  Dvalue = 2.23
  Group = -> [B_element004,O_element043,Na_element008,Al_element003,Si_element003,K_element004]
  conduct = 2
  density = 1
  expand = 3
  formula = G4_Pyrex_Glass
  name = G4_Pyrex_Glass
  specific = 4
FEATURE [App::DocumentObjectGroupPython] O_element044  label="O_element : 0.156"  # scripted group (container) (typed FeaturePython)
  n = 0.156453
FEATURE [App::DocumentObjectGroupPython] Si_element004  label="Si_element : 0.081"  # scripted group (container) (typed FeaturePython)
  n = 0.080866
FEATURE [App::DocumentObjectGroupPython] Ti_element001  label="Ti_element : 0.008"  # scripted group (container) (typed FeaturePython)
  n = 0.008092
FEATURE [App::DocumentObjectGroupPython] As_element002  label="As_element : 0.003"  # scripted group (container) (typed FeaturePython)
  n = 0.002651
FEATURE [App::DocumentObjectGroupPython] Pb_element001  label="Pb_element : 0.752"  # scripted group (container) (typed FeaturePython)
  n = 0.751938
FEATURE [App::DocumentObjectGroupPython] G4_GLASS_LEAD  # scripted group (container) (typed FeaturePython)
  Dunit = g/cm3
  Dvalue = 6.22
  Group = -> [O_element044,Si_element004,Ti_element001,As_element002,Pb_element001]
  conduct = 2
  density = 1
  expand = 3
  formula = G4_GLASS_LEAD
  name = G4_GLASS_LEAD
  specific = 4
FEATURE [App::DocumentObjectGroupPython] O_element045  label="O_element : 0.460"  # scripted group (container) (typed FeaturePython)
  n = 0.4598
FEATURE [App::DocumentObjectGroupPython] Na_element009  label="Na_element : 0.096"  # scripted group (container) (typed FeaturePython)
  n = 0.0964411
FEATURE [App::DocumentObjectGroupPython] Si_element005  label="Si_element : 0.378"  # scripted group (container) (typed FeaturePython)
  n = 0.336553
FEATURE [App::DocumentObjectGroupPython] Ca_element011  label="Ca_element : 0.107"  # scripted group (container) (typed FeaturePython)
  n = 0.107205
FEATURE [App::DocumentObjectGroupPython] G4_GLASS_PLATE  # scripted group (container) (typed FeaturePython)
  Dunit = g/cm3
  Dvalue = 2.4
  Group = -> [O_element045,Na_element009,Si_element005,Ca_element011]
  conduct = 2
  density = 1
  expand = 3
  formula = G4_GLASS_PLATE
  name = G4_GLASS_PLATE
  specific = 4
FEATURE [App::DocumentObjectGroupPython] C_element049  label="C_element : 026"  # scripted group (container) (typed FeaturePython)
  n = 5
  ref = C_element
FEATURE [App::DocumentObjectGroupPython] H_element042  label="H_element : 021"  # scripted group (container) (typed FeaturePython)
  n = 10
  ref = H_element
FEATURE [App::DocumentObjectGroupPython] N_element019  label="N_element : 2"  # scripted group (container) (typed FeaturePython)
  n = 2
  ref = N_element
FEATURE [App::DocumentObjectGroupPython] O_element046  label="O_element : 022"  # scripted group (container) (typed FeaturePython)
  n = 3
  ref = O_element
FEATURE [App::DocumentObjectGroupPython] G4_GLUTAMINE  # scripted group (container) (typed FeaturePython)
  Dunit = g/cm3
  Dvalue = 1.46
  Group = -> [C_element049,H_element042,N_element019,O_element046]
  conduct = 2
  density = 1
  expand = 3
  formula = G4_GLUTAMINE
  name = G4_GLUTAMINE
  specific = 4
FEATURE [App::DocumentObjectGroupPython] C_element050  label="C_element : 027"  # scripted group (container) (typed FeaturePython)
  n = 3
  ref = C_element
FEATURE [App::DocumentObjectGroupPython] H_element043  label="H_element : 022"  # scripted group (container) (typed FeaturePython)
  n = 8
  ref = H_element
FEATURE [App::DocumentObjectGroupPython] O_element047  label="O_element : 023"  # scripted group (container) (typed FeaturePython)
  n = 3
  ref = O_element
FEATURE [App::DocumentObjectGroupPython] G4_GLYCEROL  # scripted group (container) (typed FeaturePython)
  Dunit = g/cm3
  Dvalue = 1.2613
  Group = -> [C_element050,H_element043,O_element047]
  conduct = 2
  density = 1
  expand = 3
  formula = G4_GLYCEROL
  name = G4_GLYCEROL
  specific = 4
FEATURE [App::DocumentObjectGroupPython] C_element051  label="C_element : 028"  # scripted group (container) (typed FeaturePython)
  n = 5
  ref = C_element
FEATURE [App::DocumentObjectGroupPython] H_element044  label="H_element : 023"  # scripted group (container) (typed FeaturePython)
  n = 5
  ref = H_element
FEATURE [App::DocumentObjectGroupPython] N_element020  label="N_element : 009"  # scripted group (container) (typed FeaturePython)
  n = 5
  ref = N_element
FEATURE [App::DocumentObjectGroupPython] O_element048  label="O_element : 024"  # scripted group (container) (typed FeaturePython)
  n = 1
  ref = O_element
FEATURE [App::DocumentObjectGroupPython] G4_GUANINE  # scripted group (container) (typed FeaturePython)
  Dunit = g/cm3
  Dvalue = 2.2
  Group = -> [C_element051,H_element044,N_element020,O_element048]
  conduct = 2
  density = 1
  expand = 3
  formula = G4_GUANINE
  name = G4_GUANINE
  specific = 4
FEATURE [App::DocumentObjectGroupPython] Ca_element012  label="Ca_element : 006"  # scripted group (container) (typed FeaturePython)
  n = 1
  ref = Ca_element
FEATURE [App::DocumentObjectGroupPython] S_element014  label="S_element : 005"  # scripted group (container) (typed FeaturePython)
  n = 1
  ref = S_element
FEATURE [App::DocumentObjectGroupPython] O_element049  label="O_element : 6"  # scripted group (container) (typed FeaturePython)
  n = 6
  ref = O_element
FEATURE [App::DocumentObjectGroupPython] H_element045  label="H_element : 024"  # scripted group (container) (typed FeaturePython)
  n = 4
  ref = H_element
FEATURE [App::DocumentObjectGroupPython] G4_GYPSUM  # scripted group (container) (typed FeaturePython)
  Dunit = g/cm3
  Dvalue = 2.32
  Group = -> [Ca_element012,S_element014,O_element049,H_element045]
  conduct = 2
  density = 1
  expand = 3
  formula = G4_GYPSUM
  name = G4_GYPSUM
  specific = 4
FEATURE [App::DocumentObjectGroupPython] C_element052  label="C_element : 7"  # scripted group (container) (typed FeaturePython)
  n = 7
  ref = C_element
FEATURE [App::DocumentObjectGroupPython] H_element046  label="H_element : 16"  # scripted group (container) (typed FeaturePython)
  n = 16
  ref = H_element
FEATURE [App::DocumentObjectGroupPython] G4_N_HEPTANE  label="G4_N-HEPTANE"  # scripted group (container) (typed FeaturePython)
  Dunit = g/cm3
  Dvalue = 0.68376
  Group = -> [C_element052,H_element046]
  conduct = 2
  density = 1
  expand = 3
  formula = G4_N-HEPTANE
  name = G4_N-HEPTANE
  specific = 4
FEATURE [App::DocumentObjectGroupPython] C_element053  label="C_element : 029"  # scripted group (container) (typed FeaturePython)
  n = 6
  ref = C_element
FEATURE [App::DocumentObjectGroupPython] H_element047  label="H_element : 14"  # scripted group (container) (typed FeaturePython)
  n = 14
  ref = H_element
FEATURE [App::DocumentObjectGroupPython] G4_N_HEXANE  label="G4_N-HEXANE"  # scripted group (container) (typed FeaturePython)
  Dunit = g/cm3
  Dvalue = 0.6603
  Group = -> [C_element053,H_element047]
  conduct = 2
  density = 1
  expand = 3
  formula = G4_N-HEXANE
  name = G4_N-HEXANE
  specific = 4
FEATURE [App::DocumentObjectGroupPython] C_element054  label="C_element : 22"  # scripted group (container) (typed FeaturePython)
  n = 22
  ref = C_element
FEATURE [App::DocumentObjectGroupPython] H_element048  label="H_element : 025"  # scripted group (container) (typed FeaturePython)
  n = 10
  ref = H_element
FEATURE [App::DocumentObjectGroupPython] N_element021  label="N_element : 010"  # scripted group (container) (typed FeaturePython)
  n = 2
  ref = N_element
FEATURE [App::DocumentObjectGroupPython] O_element050  label="O_element : 025"  # scripted group (container) (typed FeaturePython)
  n = 5
  ref = O_element
FEATURE [App::DocumentObjectGroupPython] G4_KAPTON  # scripted group (container) (typed FeaturePython)
  Dunit = g/cm3
  Dvalue = 1.42
  Group = -> [C_element054,H_element048,N_element021,O_element050]
  conduct = 2
  density = 1
  expand = 3
  formula = G4_KAPTON
  name = G4_KAPTON
  specific = 4
FEATURE [App::DocumentObjectGroupPython] La_element001  label="La_element : 1"  # scripted group (container) (typed FeaturePython)
  n = 1
  ref = La_element
FEATURE [App::DocumentObjectGroupPython] Br_element003  label="Br_element : 002"  # scripted group (container) (typed FeaturePython)
  n = 1
  ref = Br_element
FEATURE [App::DocumentObjectGroupPython] O_element051  label="O_element : 026"  # scripted group (container) (typed FeaturePython)
  n = 1
  ref = O_element
FEATURE [App::DocumentObjectGroupPython] G4_LANTHANUM_OXYBROMIDE  # scripted group (container) (typed FeaturePython)
  Dunit = g/cm3
  Dvalue = 6.28
  Group = -> [La_element001,Br_element003,O_element051]
  conduct = 2
  density = 1
  expand = 3
  formula = G4_LANTHANUM_OXYBROMIDE
  name = G4_LANTHANUM_OXYBROMIDE
  specific = 4
FEATURE [App::DocumentObjectGroupPython] La_element002  label="La_element : 2"  # scripted group (container) (typed FeaturePython)
  n = 2
  ref = La_element
FEATURE [App::DocumentObjectGroupPython] O_element052  label="O_element : 027"  # scripted group (container) (typed FeaturePython)
  n = 2
  ref = O_element
FEATURE [App::DocumentObjectGroupPython] S_element015  label="S_element : 006"  # scripted group (container) (typed FeaturePython)
  n = 1
  ref = S_element
FEATURE [App::DocumentObjectGroupPython] G4_LANTHANUM_OXYSULFIDE  # scripted group (container) (typed FeaturePython)
  Dunit = g/cm3
  Dvalue = 5.86
  Group = -> [La_element002,O_element052,S_element015]
  conduct = 2
  density = 1
  expand = 3
  formula = G4_LANTHANUM_OXYSULFIDE
  name = G4_LANTHANUM_OXYSULFIDE
  specific = 4
FEATURE [App::DocumentObjectGroupPython] O_element053  label="O_element : 0.072"  # scripted group (container) (typed FeaturePython)
  n = 0.071682
FEATURE [App::DocumentObjectGroupPython] Pb_element002  label="Pb_element : 0.928"  # scripted group (container) (typed FeaturePython)
  n = 0.928318
FEATURE [App::DocumentObjectGroupPython] G4_LEAD_OXIDE  # scripted group (container) (typed FeaturePython)
  Dunit = g/cm3
  Dvalue = 9.53
  Group = -> [O_element053,Pb_element002]
  conduct = 2
  density = 1
  expand = 3
  formula = G4_LEAD_OXIDE
  name = G4_LEAD_OXIDE
  specific = 4
FEATURE [App::DocumentObjectGroupPython] Li_element001  label="Li_element : 1"  # scripted group (container) (typed FeaturePython)
  n = 1
  ref = Li_element
FEATURE [App::DocumentObjectGroupPython] N_element022  label="N_element : 011"  # scripted group (container) (typed FeaturePython)
  n = 1
  ref = N_element
FEATURE [App::DocumentObjectGroupPython] H_element049  label="H_element : 026"  # scripted group (container) (typed FeaturePython)
  n = 2
  ref = H_element
FEATURE [App::DocumentObjectGroupPython] G4_LITHIUM_AMIDE  # scripted group (container) (typed FeaturePython)
  Dunit = g/cm3
  Dvalue = 1.178
  Group = -> [Li_element001,N_element022,H_element049]
  conduct = 2
  density = 1
  expand = 3
  formula = G4_LITHIUM_AMIDE
  name = G4_LITHIUM_AMIDE
  specific = 4
FEATURE [App::DocumentObjectGroupPython] Li_element002  label="Li_element : 2"  # scripted group (container) (typed FeaturePython)
  n = 2
  ref = Li_element
FEATURE [App::DocumentObjectGroupPython] C_element055  label="C_element : 030"  # scripted group (container) (typed FeaturePython)
  n = 1
  ref = C_element
FEATURE [App::DocumentObjectGroupPython] O_element054  label="O_element : 028"  # scripted group (container) (typed FeaturePython)
  n = 3
  ref = O_element
FEATURE [App::DocumentObjectGroupPython] G4_LITHIUM_CARBONATE  # scripted group (container) (typed FeaturePython)
  Dunit = g/cm3
  Dvalue = 2.11
  Group = -> [Li_element002,C_element055,O_element054]
  conduct = 2
  density = 1
  expand = 3
  formula = G4_LITHIUM_CARBONATE
  name = G4_LITHIUM_CARBONATE
  specific = 4
FEATURE [App::DocumentObjectGroupPython] Li_element003  label="Li_element : 003"  # scripted group (container) (typed FeaturePython)
  n = 1
  ref = Li_element
FEATURE [App::DocumentObjectGroupPython] F_element012  label="F_element : 004"  # scripted group (container) (typed FeaturePython)
  n = 1
  ref = F_element
FEATURE [App::DocumentObjectGroupPython] G4_LITHIUM_FLUORIDE  # scripted group (container) (typed FeaturePython)
  Dunit = g/cm3
  Dvalue = 2.635
  Group = -> [Li_element003,F_element012]
  conduct = 2
  density = 1
  expand = 3
  formula = G4_LITHIUM_FLUORIDE
  name = G4_LITHIUM_FLUORIDE
  specific = 4
FEATURE [App::DocumentObjectGroupPython] Li_element004  label="Li_element : 004"  # scripted group (container) (typed FeaturePython)
  n = 1
  ref = Li_element
FEATURE [App::DocumentObjectGroupPython] H_element050  label="H_element : 027"  # scripted group (container) (typed FeaturePython)
  n = 1
  ref = H_element
FEATURE [App::DocumentObjectGroupPython] G4_LITHIUM_HYDRIDE  # scripted group (container) (typed FeaturePython)
  Dunit = g/cm3
  Dvalue = 0.82
  Group = -> [Li_element004,H_element050]
  conduct = 2
  density = 1
  expand = 3
  formula = G4_LITHIUM_HYDRIDE
  name = G4_LITHIUM_HYDRIDE
  specific = 4
FEATURE [App::DocumentObjectGroupPython] Li_element005  label="Li_element : 005"  # scripted group (container) (typed FeaturePython)
  n = 1
  ref = Li_element
FEATURE [App::DocumentObjectGroupPython] I_element003  label="I_element : 002"  # scripted group (container) (typed FeaturePython)
  n = 1
  ref = I_element
FEATURE [App::DocumentObjectGroupPython] G4_LITHIUM_IODIDE  # scripted group (container) (typed FeaturePython)
  Dunit = g/cm3
  Dvalue = 3.494
  Group = -> [Li_element005,I_element003]
  conduct = 2
  density = 1
  expand = 3
  formula = G4_LITHIUM_IODIDE
  name = G4_LITHIUM_IODIDE
  specific = 4
FEATURE [App::DocumentObjectGroupPython] Li_element006  label="Li_element : 006"  # scripted group (container) (typed FeaturePython)
  n = 2
  ref = Li_element
FEATURE [App::DocumentObjectGroupPython] O_element055  label="O_element : 029"  # scripted group (container) (typed FeaturePython)
  n = 1
  ref = O_element
FEATURE [App::DocumentObjectGroupPython] G4_LITHIUM_OXIDE  # scripted group (container) (typed FeaturePython)
  Dunit = g/cm3
  Dvalue = 2.013
  Group = -> [Li_element006,O_element055]
  conduct = 2
  density = 1
  expand = 3
  formula = G4_LITHIUM_OXIDE
  name = G4_LITHIUM_OXIDE
  specific = 4
FEATURE [App::DocumentObjectGroupPython] Li_element007  label="Li_element : 007"  # scripted group (container) (typed FeaturePython)
  n = 2
  ref = Li_element
FEATURE [App::DocumentObjectGroupPython] B_element005  label="B_element : 005"  # scripted group (container) (typed FeaturePython)
  n = 4
  ref = B_element
FEATURE [App::DocumentObjectGroupPython] O_element056  label="O_element : 7"  # scripted group (container) (typed FeaturePython)
  n = 7
  ref = O_element
FEATURE [App::DocumentObjectGroupPython] G4_LITHIUM_TETRABORATE  # scripted group (container) (typed FeaturePython)
  Dunit = g/cm3
  Dvalue = 2.44
  Group = -> [Li_element007,B_element005,O_element056]
  conduct = 2
  density = 1
  expand = 3
  formula = G4_LITHIUM_TETRABORATE
  name = G4_LITHIUM_TETRABORATE
  specific = 4
FEATURE [App::DocumentObjectGroupPython] H_element051  label="H_element : 0.105"  # scripted group (container) (typed FeaturePython)
  n = 0.105
FEATURE [App::DocumentObjectGroupPython] C_element056  label="C_element : 0.083"  # scripted group (container) (typed FeaturePython)
  n = 0.083
FEATURE [App::DocumentObjectGroupPython] N_element023  label="N_element : 0.023"  # scripted group (container) (typed FeaturePython)
  n = 0.023
FEATURE [App::DocumentObjectGroupPython] O_element057  label="O_element : 0.779"  # scripted group (container) (typed FeaturePython)
  n = 0.779
FEATURE [App::DocumentObjectGroupPython] Na_element010  label="Na_element : 0.097"  # scripted group (container) (typed FeaturePython)
  n = 0.002
FEATURE [App::DocumentObjectGroupPython] P_element006  label="P_element : 0.105"  # scripted group (container) (typed FeaturePython)
  n = 0.001
FEATURE [App::DocumentObjectGroupPython] S_element016  label="S_element : 0.017"  # scripted group (container) (typed FeaturePython)
  n = 0.002
FEATURE [App::DocumentObjectGroupPython] Cl_element014  label="Cl_element : 0.587"  # scripted group (container) (typed FeaturePython)
  n = 0.003
FEATURE [App::DocumentObjectGroupPython] K_element005  label="K_element : 0.015"  # scripted group (container) (typed FeaturePython)
  n = 0.002
FEATURE [App::DocumentObjectGroupPython] G4_LUNG_ICRP  # scripted group (container) (typed FeaturePython)
  Dunit = g/cm3
  Dvalue = 1.04
  Group = -> [H_element051,C_element056,N_element023,O_element057,Na_element010,P_element006,S_element016,Cl_element014,K_element005]
  conduct = 2
  density = 1
  expand = 3
  formula = G4_LUNG_ICRP
  name = G4_LUNG_ICRP
  specific = 4
FEATURE [App::DocumentObjectGroupPython] H_element052  label="H_element : 0.116"  # scripted group (container) (typed FeaturePython)
  n = 0.114318
FEATURE [App::DocumentObjectGroupPython] C_element057  label="C_element : 0.656"  # scripted group (container) (typed FeaturePython)
  n = 0.655824
FEATURE [App::DocumentObjectGroupPython] O_element058  label="O_element : 0.092"  # scripted group (container) (typed FeaturePython)
  n = 0.0921831
FEATURE [App::DocumentObjectGroupPython] Mg_element004  label="Mg_element : 0.135"  # scripted group (container) (typed FeaturePython)
  n = 0.134792
FEATURE [App::DocumentObjectGroupPython] Ca_element013  label="Ca_element : 0.003"  # scripted group (container) (typed FeaturePython)
  n = 0.002883
FEATURE [App::DocumentObjectGroupPython] G4_M3_WAX  # scripted group (container) (typed FeaturePython)
  Dunit = g/cm3
  Dvalue = 1.05
  Group = -> [H_element052,C_element057,O_element058,Mg_element004,Ca_element013]
  conduct = 2
  density = 1
  expand = 3
  formula = G4_M3_WAX
  name = G4_M3_WAX
  specific = 4
FEATURE [App::DocumentObjectGroupPython] Mg_element005  label="Mg_element : 1"  # scripted group (container) (typed FeaturePython)
  n = 1
  ref = Mg_element
FEATURE [App::DocumentObjectGroupPython] C_element058  label="C_element : 031"  # scripted group (container) (typed FeaturePython)
  n = 1
  ref = C_element
FEATURE [App::DocumentObjectGroupPython] O_element059  label="O_element : 030"  # scripted group (container) (typed FeaturePython)
  n = 3
  ref = O_element
FEATURE [App::DocumentObjectGroupPython] G4_MAGNESIUM_CARBONATE  # scripted group (container) (typed FeaturePython)
  Dunit = g/cm3
  Dvalue = 2.958
  Group = -> [Mg_element005,C_element058,O_element059]
  conduct = 2
  density = 1
  expand = 3
  formula = G4_MAGNESIUM_CARBONATE
  name = G4_MAGNESIUM_CARBONATE
  specific = 4
FEATURE [App::DocumentObjectGroupPython] Mg_element006  label="Mg_element : 002"  # scripted group (container) (typed FeaturePython)
  n = 1
  ref = Mg_element
FEATURE [App::DocumentObjectGroupPython] F_element013  label="F_element : 005"  # scripted group (container) (typed FeaturePython)
  n = 2
  ref = F_element
FEATURE [App::DocumentObjectGroupPython] G4_MAGNESIUM_FLUORIDE  # scripted group (container) (typed FeaturePython)
  Dunit = g/cm3
  Dvalue = 3
  Group = -> [Mg_element006,F_element013]
  conduct = 2
  density = 1
  expand = 3
  formula = G4_MAGNESIUM_FLUORIDE
  name = G4_MAGNESIUM_FLUORIDE
  specific = 4
FEATURE [App::DocumentObjectGroupPython] Mg_element007  label="Mg_element : 003"  # scripted group (container) (typed FeaturePython)
  n = 1
  ref = Mg_element
FEATURE [App::DocumentObjectGroupPython] O_element060  label="O_element : 031"  # scripted group (container) (typed FeaturePython)
  n = 1
  ref = O_element
FEATURE [App::DocumentObjectGroupPython] G4_MAGNESIUM_OXIDE  # scripted group (container) (typed FeaturePython)
  Dunit = g/cm3
  Dvalue = 3.58
  Group = -> [Mg_element007,O_element060]
  conduct = 2
  density = 1
  expand = 3
  formula = G4_MAGNESIUM_OXIDE
  name = G4_MAGNESIUM_OXIDE
  specific = 4
FEATURE [App::DocumentObjectGroupPython] Mg_element008  label="Mg_element : 004"  # scripted group (container) (typed FeaturePython)
  n = 1
  ref = Mg_element
FEATURE [App::DocumentObjectGroupPython] B_element006  label="B_element : 006"  # scripted group (container) (typed FeaturePython)
  n = 4
  ref = B_element
FEATURE [App::DocumentObjectGroupPython] O_element061  label="O_element : 032"  # scripted group (container) (typed FeaturePython)
  n = 7
  ref = O_element
FEATURE [App::DocumentObjectGroupPython] G4_MAGNESIUM_TETRABORATE  # scripted group (container) (typed FeaturePython)
  Dunit = g/cm3
  Dvalue = 2.53
  Group = -> [Mg_element008,B_element006,O_element061]
  conduct = 2
  density = 1
  expand = 3
  formula = G4_MAGNESIUM_TETRABORATE
  name = G4_MAGNESIUM_TETRABORATE
  specific = 4
FEATURE [App::DocumentObjectGroupPython] Hg_element001  label="Hg_element : 1"  # scripted group (container) (typed FeaturePython)
  n = 1
  ref = Hg_element
FEATURE [App::DocumentObjectGroupPython] I_element004  label="I_element : 2"  # scripted group (container) (typed FeaturePython)
  n = 2
  ref = I_element
FEATURE [App::DocumentObjectGroupPython] G4_MERCURIC_IODIDE  # scripted group (container) (typed FeaturePython)
  Dunit = g/cm3
  Dvalue = 6.36
  Group = -> [Hg_element001,I_element004]
  conduct = 2
  density = 1
  expand = 3
  formula = G4_MERCURIC_IODIDE
  name = G4_MERCURIC_IODIDE
  specific = 4
FEATURE [App::DocumentObjectGroupPython] C_element059  label="C_element : 032"  # scripted group (container) (typed FeaturePython)
  n = 1
  ref = C_element
FEATURE [App::DocumentObjectGroupPython] H_element053  label="H_element : 028"  # scripted group (container) (typed FeaturePython)
  n = 4
  ref = H_element
FEATURE [App::DocumentObjectGroupPython] G4_METHANE  # scripted group (container) (typed FeaturePython)
  Dunit = g/cm3
  Dvalue = 0.000667151
  Group = -> [C_element059,H_element053]
  conduct = 2
  density = 1
  expand = 3
  formula = G4_METHANE
  name = G4_METHANE
  specific = 4
FEATURE [App::DocumentObjectGroupPython] C_element060  label="C_element : 033"  # scripted group (container) (typed FeaturePython)
  n = 1
  ref = C_element
FEATURE [App::DocumentObjectGroupPython] H_element054  label="H_element : 029"  # scripted group (container) (typed FeaturePython)
  n = 4
  ref = H_element
FEATURE [App::DocumentObjectGroupPython] O_element062  label="O_element : 033"  # scripted group (container) (typed FeaturePython)
  n = 1
  ref = O_element
FEATURE [App::DocumentObjectGroupPython] G4_METHANOL  # scripted group (container) (typed FeaturePython)
  Dunit = g/cm3
  Dvalue = 0.7914
  Group = -> [C_element060,H_element054,O_element062]
  conduct = 2
  density = 1
  expand = 3
  formula = G4_METHANOL
  name = G4_METHANOL
  specific = 4
FEATURE [App::DocumentObjectGroupPython] H_element055  label="H_element : 0.134"  # scripted group (container) (typed FeaturePython)
  n = 0.13404
FEATURE [App::DocumentObjectGroupPython] C_element061  label="C_element : 0.778"  # scripted group (container) (typed FeaturePython)
  n = 0.77796
FEATURE [App::DocumentObjectGroupPython] O_element063  label="O_element : 0.035"  # scripted group (container) (typed FeaturePython)
  n = 0.03502
FEATURE [App::DocumentObjectGroupPython] Mg_element009  label="Mg_element : 0.039"  # scripted group (container) (typed FeaturePython)
  n = 0.038594
FEATURE [App::DocumentObjectGroupPython] Ti_element002  label="Ti_element : 0.014"  # scripted group (container) (typed FeaturePython)
  n = 0.014386
FEATURE [App::DocumentObjectGroupPython] G4_MIX_D_WAX  # scripted group (container) (typed FeaturePython)
  Dunit = g/cm3
  Dvalue = 0.99
  Group = -> [H_element055,C_element061,O_element063,Mg_element009,Ti_element002]
  conduct = 2
  density = 1
  expand = 3
  formula = G4_MIX_D_WAX
  name = G4_MIX_D_WAX
  specific = 4
FEATURE [App::DocumentObjectGroupPython] H_element056  label="H_element : 0.135"  # scripted group (container) (typed FeaturePython)
  n = 0.081192
FEATURE [App::DocumentObjectGroupPython] C_element062  label="C_element : 0.583"  # scripted group (container) (typed FeaturePython)
  n = 0.583442
FEATURE [App::DocumentObjectGroupPython] N_element024  label="N_element : 0.018"  # scripted group (container) (typed FeaturePython)
  n = 0.017798
FEATURE [App::DocumentObjectGroupPython] O_element064  label="O_element : 0.186"  # scripted group (container) (typed FeaturePython)
  n = 0.186381
FEATURE [App::DocumentObjectGroupPython] Mg_element010  label="Mg_element : 0.130"  # scripted group (container) (typed FeaturePython)
  n = 0.130287
FEATURE [App::DocumentObjectGroupPython] Cl_element015  label="Cl_element : 0.588"  # scripted group (container) (typed FeaturePython)
  n = 0.0009
FEATURE [App::DocumentObjectGroupPython] G4_MS20_TISSUE  # scripted group (container) (typed FeaturePython)
  Dunit = g/cm3
  Dvalue = 1
  Group = -> [H_element056,C_element062,N_element024,O_element064,Mg_element010,Cl_element015]
  conduct = 2
  density = 1
  expand = 3
  formula = G4_MS20_TISSUE
  name = G4_MS20_TISSUE
  specific = 4
FEATURE [App::DocumentObjectGroupPython] H_element057  label="H_element : 0.136"  # scripted group (container) (typed FeaturePython)
  n = 0.102
FEATURE [App::DocumentObjectGroupPython] C_element063  label="C_element : 0.143"  # scripted group (container) (typed FeaturePython)
  n = 0.143
FEATURE [App::DocumentObjectGroupPython] N_element025  label="N_element : 0.034"  # scripted group (container) (typed FeaturePython)
  n = 0.034
FEATURE [App::DocumentObjectGroupPython] O_element065  label="O_element : 0.710"  # scripted group (container) (typed FeaturePython)
  n = 0.71
FEATURE [App::DocumentObjectGroupPython] Na_element011  label="Na_element : 0.098"  # scripted group (container) (typed FeaturePython)
  n = 0.001
FEATURE [App::DocumentObjectGroupPython] P_element007  label="P_element : 0.002"  # scripted group (container) (typed FeaturePython)
  n = 0.002
FEATURE [App::DocumentObjectGroupPython] S_element017  label="S_element : 0.018"  # scripted group (container) (typed FeaturePython)
  n = 0.003
FEATURE [App::DocumentObjectGroupPython] Cl_element016  label="Cl_element : 0.589"  # scripted group (container) (typed FeaturePython)
  n = 0.001
FEATURE [App::DocumentObjectGroupPython] K_element006  label="K_element : 0.004"  # scripted group (container) (typed FeaturePython)
  n = 0.004
FEATURE [App::DocumentObjectGroupPython] G4_MUSCLE_SKELETAL_ICRP  # scripted group (container) (typed FeaturePython)
  Dunit = g/cm3
  Dvalue = 1.05
  Group = -> [H_element057,C_element063,N_element025,O_element065,Na_element011,P_element007,S_element017,Cl_element016,K_element006]
  conduct = 2
  density = 1
  expand = 3
  formula = G4_MUSCLE_SKELETAL_ICRP
  name = G4_MUSCLE_SKELETAL_ICRP
  specific = 4
FEATURE [App::DocumentObjectGroupPython] H_element058  label="H_element : 0.137"  # scripted group (container) (typed FeaturePython)
  n = 0.102102
FEATURE [App::DocumentObjectGroupPython] C_element064  label="C_element : 0.123"  # scripted group (container) (typed FeaturePython)
  n = 0.123123
FEATURE [App::DocumentObjectGroupPython] N_element026  label="N_element : 0.756"  # scripted group (container) (typed FeaturePython)
  n = 0.035035
FEATURE [App::DocumentObjectGroupPython] O_element066  label="O_element : 0.730"  # scripted group (container) (typed FeaturePython)
  n = 0.72973
FEATURE [App::DocumentObjectGroupPython] Na_element012  label="Na_element : 0.099"  # scripted group (container) (typed FeaturePython)
  n = 0.001001
FEATURE [App::DocumentObjectGroupPython] P_element008  label="P_element : 0.106"  # scripted group (container) (typed FeaturePython)
  n = 0.002002
FEATURE [App::DocumentObjectGroupPython] S_element018  label="S_element : 0.019"  # scripted group (container) (typed FeaturePython)
  n = 0.004004
FEATURE [App::DocumentObjectGroupPython] K_element007  label="K_element : 0.016"  # scripted group (container) (typed FeaturePython)
  n = 0.003003
FEATURE [App::DocumentObjectGroupPython] G4_MUSCLE_STRIATED_ICRU  # scripted group (container) (typed FeaturePython)
  Dunit = g/cm3
  Dvalue = 1.04
  Group = -> [H_element058,C_element064,N_element026,O_element066,Na_element012,P_element008,S_element018,K_element007]
  conduct = 2
  density = 1
  expand = 3
  formula = G4_MUSCLE_STRIATED_ICRU
  name = G4_MUSCLE_STRIATED_ICRU
  specific = 4
FEATURE [App::DocumentObjectGroupPython] H_element059  label="H_element : 0.098"  # scripted group (container) (typed FeaturePython)
  n = 0.0982341
FEATURE [App::DocumentObjectGroupPython] C_element065  label="C_element : 0.156"  # scripted group (container) (typed FeaturePython)
  n = 0.156214
FEATURE [App::DocumentObjectGroupPython] N_element027  label="N_element : 0.757"  # scripted group (container) (typed FeaturePython)
  n = 0.035451
FEATURE [App::DocumentObjectGroupPython] O_element067  label="O_element : 0.880"  # scripted group (container) (typed FeaturePython)
  n = 0.710101
FEATURE [App::DocumentObjectGroupPython] G4_MUSCLE_WITH_SUCROSE  # scripted group (container) (typed FeaturePython)
  Dunit = g/cm3
  Dvalue = 1.11
  Group = -> [H_element059,C_element065,N_element027,O_element067]
  conduct = 2
  density = 1
  expand = 3
  formula = G4_MUSCLE_WITH_SUCROSE
  name = G4_MUSCLE_WITH_SUCROSE
  specific = 4
FEATURE [App::DocumentObjectGroupPython] H_element060  label="H_element : 0.138"  # scripted group (container) (typed FeaturePython)
  n = 0.101969
FEATURE [App::DocumentObjectGroupPython] C_element066  label="C_element : 0.120"  # scripted group (container) (typed FeaturePython)
  n = 0.120058
FEATURE [App::DocumentObjectGroupPython] N_element028  label="N_element : 0.758"  # scripted group (container) (typed FeaturePython)
  n = 0.035451
FEATURE [App::DocumentObjectGroupPython] O_element068  label="O_element : 0.743"  # scripted group (container) (typed FeaturePython)
  n = 0.742522
FEATURE [App::DocumentObjectGroupPython] G4_MUSCLE_WITHOUT_SUCROSE  # scripted group (container) (typed FeaturePython)
  Dunit = g/cm3
  Dvalue = 1.07
  Group = -> [H_element060,C_element066,N_element028,O_element068]
  conduct = 2
  density = 1
  expand = 3
  formula = G4_MUSCLE_WITHOUT_SUCROSE
  name = G4_MUSCLE_WITHOUT_SUCROSE
  specific = 4
FEATURE [App::DocumentObjectGroupPython] C_element067  label="C_element : 10"  # scripted group (container) (typed FeaturePython)
  n = 10
  ref = C_element
FEATURE [App::DocumentObjectGroupPython] H_element061  label="H_element : 030"  # scripted group (container) (typed FeaturePython)
  n = 8
  ref = H_element
FEATURE [App::DocumentObjectGroupPython] G4_NAPHTHALENE  # scripted group (container) (typed FeaturePython)
  Dunit = g/cm3
  Dvalue = 1.145
  Group = -> [C_element067,H_element061]
  conduct = 2
  density = 1
  expand = 3
  formula = G4_NAPHTHALENE
  name = G4_NAPHTHALENE
  specific = 4
FEATURE [App::DocumentObjectGroupPython] C_element068  label="C_element : 034"  # scripted group (container) (typed FeaturePython)
  n = 6
  ref = C_element
FEATURE [App::DocumentObjectGroupPython] H_element062  label="H_element : 031"  # scripted group (container) (typed FeaturePython)
  n = 5
  ref = H_element
FEATURE [App::DocumentObjectGroupPython] N_element029  label="N_element : 012"  # scripted group (container) (typed FeaturePython)
  n = 1
  ref = N_element
FEATURE [App::DocumentObjectGroupPython] O_element069  label="O_element : 034"  # scripted group (container) (typed FeaturePython)
  n = 2
  ref = O_element
FEATURE [App::DocumentObjectGroupPython] G4_NITROBENZENE  # scripted group (container) (typed FeaturePython)
  Dunit = g/cm3
  Dvalue = 1.19867
  Group = -> [C_element068,H_element062,N_element029,O_element069]
  conduct = 2
  density = 1
  expand = 3
  formula = G4_NITROBENZENE
  name = G4_NITROBENZENE
  specific = 4
FEATURE [App::DocumentObjectGroupPython] N_element030  label="N_element : 013"  # scripted group (container) (typed FeaturePython)
  n = 2
  ref = N_element
FEATURE [App::DocumentObjectGroupPython] O_element070  label="O_element : 035"  # scripted group (container) (typed FeaturePython)
  n = 1
  ref = O_element
FEATURE [App::DocumentObjectGroupPython] G4_NITROUS_OXIDE  # scripted group (container) (typed FeaturePython)
  Dunit = g/cm3
  Dvalue = 0.00183094
  Group = -> [N_element030,O_element070]
  conduct = 2
  density = 1
  expand = 3
  formula = G4_NITROUS_OXIDE
  name = G4_NITROUS_OXIDE
  specific = 4
FEATURE [App::DocumentObjectGroupPython] H_element063  label="H_element : 0.104"  # scripted group (container) (typed FeaturePython)
  n = 0.103509
FEATURE [App::DocumentObjectGroupPython] C_element069  label="C_element : 0.648"  # scripted group (container) (typed FeaturePython)
  n = 0.648416
FEATURE [App::DocumentObjectGroupPython] N_element031  label="N_element : 0.100"  # scripted group (container) (typed FeaturePython)
  n = 0.0995361
FEATURE [App::DocumentObjectGroupPython] O_element071  label="O_element : 0.149"  # scripted group (container) (typed FeaturePython)
  n = 0.148539
FEATURE [App::DocumentObjectGroupPython] G4_NYLON_8062  label="G4_NYLON-8062"  # scripted group (container) (typed FeaturePython)
  Dunit = g/cm3
  Dvalue = 1.08
  Group = -> [H_element063,C_element069,N_element031,O_element071]
  conduct = 2
  density = 1
  expand = 3
  formula = G4_NYLON-8062
  name = G4_NYLON-8062
  specific = 4
FEATURE [App::DocumentObjectGroupPython] C_element070  label="C_element : 035"  # scripted group (container) (typed FeaturePython)
  n = 6
  ref = C_element
FEATURE [App::DocumentObjectGroupPython] H_element064  label="H_element : 11"  # scripted group (container) (typed FeaturePython)
  n = 11
  ref = H_element
FEATURE [App::DocumentObjectGroupPython] N_element032  label="N_element : 014"  # scripted group (container) (typed FeaturePython)
  n = 1
  ref = N_element
FEATURE [App::DocumentObjectGroupPython] O_element072  label="O_element : 036"  # scripted group (container) (typed FeaturePython)
  n = 1
  ref = O_element
FEATURE [App::DocumentObjectGroupPython] G4_NYLON_6_6  label="G4_NYLON-6-6"  # scripted group (container) (typed FeaturePython)
  Dunit = g/cm3
  Dvalue = 1.14
  Group = -> [C_element070,H_element064,N_element032,O_element072]
  conduct = 2
  density = 1
  expand = 3
  formula = G4_NYLON-6-6
  name = G4_NYLON-6-6
  specific = 4
FEATURE [App::DocumentObjectGroupPython] H_element065  label="H_element : 0.139"  # scripted group (container) (typed FeaturePython)
  n = 0.107062
FEATURE [App::DocumentObjectGroupPython] C_element071  label="C_element : 0.680"  # scripted group (container) (typed FeaturePython)
  n = 0.680449
FEATURE [App::DocumentObjectGroupPython] N_element033  label="N_element : 0.099"  # scripted group (container) (typed FeaturePython)
  n = 0.099189
FEATURE [App::DocumentObjectGroupPython] O_element073  label="O_element : 0.113"  # scripted group (container) (typed FeaturePython)
  n = 0.1133
FEATURE [App::DocumentObjectGroupPython] G4_NYLON_6_10  label="G4_NYLON-6-10"  # scripted group (container) (typed FeaturePython)
  Dunit = g/cm3
  Dvalue = 1.14
  Group = -> [H_element065,C_element071,N_element033,O_element073]
  conduct = 2
  density = 1
  expand = 3
  formula = G4_NYLON-6-10
  name = G4_NYLON-6-10
  specific = 4
FEATURE [App::DocumentObjectGroupPython] H_element066  label="H_element : 0.140"  # scripted group (container) (typed FeaturePython)
  n = 0.115476
FEATURE [App::DocumentObjectGroupPython] C_element072  label="C_element : 0.721"  # scripted group (container) (typed FeaturePython)
  n = 0.720818
FEATURE [App::DocumentObjectGroupPython] N_element034  label="N_element : 0.076"  # scripted group (container) (typed FeaturePython)
  n = 0.0764169
FEATURE [App::DocumentObjectGroupPython] O_element074  label="O_element : 0.087"  # scripted group (container) (typed FeaturePython)
  n = 0.0872889
FEATURE [App::DocumentObjectGroupPython] G4_NYLON_11_RILSAN  label="G4_NYLON-11_RILSAN"  # scripted group (container) (typed FeaturePython)
  Dunit = g/cm3
  Dvalue = 1.425
  Group = -> [H_element066,C_element072,N_element034,O_element074]
  conduct = 2
  density = 1
  expand = 3
  formula = G4_NYLON-11_RILSAN
  name = G4_NYLON-11_RILSAN
  specific = 4
FEATURE [App::DocumentObjectGroupPython] C_element073  label="C_element : 8"  # scripted group (container) (typed FeaturePython)
  n = 8
  ref = C_element
FEATURE [App::DocumentObjectGroupPython] H_element067  label="H_element : 18"  # scripted group (container) (typed FeaturePython)
  n = 18
  ref = H_element
FEATURE [App::DocumentObjectGroupPython] G4_OCTANE  # scripted group (container) (typed FeaturePython)
  Dunit = g/cm3
  Dvalue = 0.7026
  Group = -> [C_element073,H_element067]
  conduct = 2
  density = 1
  expand = 3
  formula = G4_OCTANE
  name = G4_OCTANE
  specific = 4
FEATURE [App::DocumentObjectGroupPython] C_element074  label="C_element : 25"  # scripted group (container) (typed FeaturePython)
  n = 25
  ref = C_element
FEATURE [App::DocumentObjectGroupPython] H_element068  label="H_element : 52"  # scripted group (container) (typed FeaturePython)
  n = 52
  ref = H_element
FEATURE [App::DocumentObjectGroupPython] G4_PARAFFIN  # scripted group (container) (typed FeaturePython)
  Dunit = g/cm3
  Dvalue = 0.93
  Group = -> [C_element074,H_element068]
  conduct = 2
  density = 1
  expand = 3
  formula = G4_PARAFFIN
  name = G4_PARAFFIN
  specific = 4
FEATURE [App::DocumentObjectGroupPython] C_element075  label="C_element : 036"  # scripted group (container) (typed FeaturePython)
  n = 5
  ref = C_element
FEATURE [App::DocumentObjectGroupPython] H_element069  label="H_element : 032"  # scripted group (container) (typed FeaturePython)
  n = 12
  ref = H_element
FEATURE [App::DocumentObjectGroupPython] G4_N_PENTANE  label="G4_N-PENTANE"  # scripted group (container) (typed FeaturePython)
  Dunit = g/cm3
  Dvalue = 0.6262
  Group = -> [C_element075,H_element069]
  conduct = 2
  density = 1
  expand = 3
  formula = G4_N-PENTANE
  name = G4_N-PENTANE
  specific = 4
FEATURE [App::DocumentObjectGroupPython] H_element070  label="H_element : 0.014"  # scripted group (container) (typed FeaturePython)
  n = 0.0141
FEATURE [App::DocumentObjectGroupPython] C_element076  label="C_element : 0.072"  # scripted group (container) (typed FeaturePython)
  n = 0.072261
FEATURE [App::DocumentObjectGroupPython] N_element035  label="N_element : 0.019"  # scripted group (container) (typed FeaturePython)
  n = 0.01932
FEATURE [App::DocumentObjectGroupPython] O_element075  label="O_element : 0.066"  # scripted group (container) (typed FeaturePython)
  n = 0.066101
FEATURE [App::DocumentObjectGroupPython] S_element019  label="S_element : 0.020"  # scripted group (container) (typed FeaturePython)
  n = 0.00189
FEATURE [App::DocumentObjectGroupPython] Br_element004  label="Br_element : 0.349"  # scripted group (container) (typed FeaturePython)
  n = 0.349103
FEATURE [App::DocumentObjectGroupPython] Ag_element001  label="Ag_element : 0.474"  # scripted group (container) (typed FeaturePython)
  n = 0.474105
FEATURE [App::DocumentObjectGroupPython] I_element005  label="I_element : 0.003"  # scripted group (container) (typed FeaturePython)
  n = 0.00312
FEATURE [App::DocumentObjectGroupPython] G4_PHOTO_EMULSION  # scripted group (container) (typed FeaturePython)
  Dunit = g/cm3
  Dvalue = 3.815
  Group = -> [H_element070,C_element076,N_element035,O_element075,S_element019,Br_element004,Ag_element001,I_element005]
  conduct = 2
  density = 1
  expand = 3
  formula = G4_PHOTO_EMULSION
  name = G4_PHOTO_EMULSION
  specific = 4
FEATURE [App::DocumentObjectGroupPython] C_element077  label="C_element : 9"  # scripted group (container) (typed FeaturePython)
  n = 9
  ref = C_element
FEATURE [App::DocumentObjectGroupPython] H_element071  label="H_element : 033"  # scripted group (container) (typed FeaturePython)
  n = 10
  ref = H_element
FEATURE [App::DocumentObjectGroupPython] G4_PLASTIC_SC_VINYLTOLUENE  # scripted group (container) (typed FeaturePython)
  Dunit = g/cm3
  Dvalue = 1.032
  Group = -> [C_element077,H_element071]
  conduct = 2
  density = 1
  expand = 3
  formula = G4_PLASTIC_SC_VINYLTOLUENE
  name = G4_PLASTIC_SC_VINYLTOLUENE
  specific = 4
FEATURE [App::DocumentObjectGroupPython] Pu_element001  label="Pu_element : 1"  # scripted group (container) (typed FeaturePython)
  n = 1
  ref = Pu_element
FEATURE [App::DocumentObjectGroupPython] O_element076  label="O_element : 037"  # scripted group (container) (typed FeaturePython)
  n = 2
  ref = O_element
FEATURE [App::DocumentObjectGroupPython] G4_PLUTONIUM_DIOXIDE  # scripted group (container) (typed FeaturePython)
  Dunit = g/cm3
  Dvalue = 11.46
  Group = -> [Pu_element001,O_element076]
  conduct = 2
  density = 1
  expand = 3
  formula = G4_PLUTONIUM_DIOXIDE
  name = G4_PLUTONIUM_DIOXIDE
  specific = 4
FEATURE [App::DocumentObjectGroupPython] C_element078  label="C_element : 037"  # scripted group (container) (typed FeaturePython)
  n = 3
  ref = C_element
FEATURE [App::DocumentObjectGroupPython] H_element072  label="H_element : 034"  # scripted group (container) (typed FeaturePython)
  n = 3
  ref = H_element
FEATURE [App::DocumentObjectGroupPython] N_element036  label="N_element : 015"  # scripted group (container) (typed FeaturePython)
  n = 1
  ref = N_element
FEATURE [App::DocumentObjectGroupPython] G4_POLYACRYLONITRILE  # scripted group (container) (typed FeaturePython)
  Dunit = g/cm3
  Dvalue = 1.17
  Group = -> [C_element078,H_element072,N_element036]
  conduct = 2
  density = 1
  expand = 3
  formula = G4_POLYACRYLONITRILE
  name = G4_POLYACRYLONITRILE
  specific = 4
FEATURE [App::DocumentObjectGroupPython] C_element079  label="C_element : 16"  # scripted group (container) (typed FeaturePython)
  n = 16
  ref = C_element
FEATURE [App::DocumentObjectGroupPython] H_element073  label="H_element : 035"  # scripted group (container) (typed FeaturePython)
  n = 14
  ref = H_element
FEATURE [App::DocumentObjectGroupPython] O_element077  label="O_element : 038"  # scripted group (container) (typed FeaturePython)
  n = 3
  ref = O_element
FEATURE [App::DocumentObjectGroupPython] G4_POLYCARBONATE  # scripted group (container) (typed FeaturePython)
  Dunit = g/cm3
  Dvalue = 1.2
  Group = -> [C_element079,H_element073,O_element077]
  conduct = 2
  density = 1
  expand = 3
  formula = G4_POLYCARBONATE
  name = G4_POLYCARBONATE
  specific = 4
FEATURE [App::DocumentObjectGroupPython] C_element080  label="C_element : 038"  # scripted group (container) (typed FeaturePython)
  n = 8
  ref = C_element
FEATURE [App::DocumentObjectGroupPython] H_element074  label="H_element : 036"  # scripted group (container) (typed FeaturePython)
  n = 7
  ref = H_element
FEATURE [App::DocumentObjectGroupPython] Cl_element017  label="Cl_element : 007"  # scripted group (container) (typed FeaturePython)
  n = 1
  ref = Cl_element
FEATURE [App::DocumentObjectGroupPython] G4_POLYCHLOROSTYRENE  # scripted group (container) (typed FeaturePython)
  Dunit = g/cm3
  Dvalue = 1.3
  Group = -> [C_element080,H_element074,Cl_element017]
  conduct = 2
  density = 1
  expand = 3
  formula = G4_POLYCHLOROSTYRENE
  name = G4_POLYCHLOROSTYRENE
  specific = 4
FEATURE [App::DocumentObjectGroupPython] C_element081  label="C_element : 039"  # scripted group (container) (typed FeaturePython)
  n = 1
  ref = C_element
FEATURE [App::DocumentObjectGroupPython] H_element075  label="H_element : 037"  # scripted group (container) (typed FeaturePython)
  n = 2
  ref = H_element
FEATURE [App::DocumentObjectGroupPython] G4_POLYETHYLENE  # scripted group (container) (typed FeaturePython)
  Dunit = g/cm3
  Dvalue = 0.94
  Group = -> [C_element081,H_element075]
  conduct = 2
  density = 1
  expand = 3
  formula = G4_POLYETHYLENE
  name = G4_POLYETHYLENE
  specific = 4
FEATURE [App::DocumentObjectGroupPython] C_element082  label="C_element : 040"  # scripted group (container) (typed FeaturePython)
  n = 10
  ref = C_element
FEATURE [App::DocumentObjectGroupPython] H_element076  label="H_element : 038"  # scripted group (container) (typed FeaturePython)
  n = 8
  ref = H_element
FEATURE [App::DocumentObjectGroupPython] O_element078  label="O_element : 039"  # scripted group (container) (typed FeaturePython)
  n = 4
  ref = O_element
FEATURE [App::DocumentObjectGroupPython] G4_MYLAR  # scripted group (container) (typed FeaturePython)
  Dunit = g/cm3
  Dvalue = 1.4
  Group = -> [C_element082,H_element076,O_element078]
  conduct = 2
  density = 1
  expand = 3
  formula = G4_MYLAR
  name = G4_MYLAR
  specific = 4
FEATURE [App::DocumentObjectGroupPython] C_element083  label="C_element : 041"  # scripted group (container) (typed FeaturePython)
  n = 5
  ref = C_element
FEATURE [App::DocumentObjectGroupPython] H_element077  label="H_element : 039"  # scripted group (container) (typed FeaturePython)
  n = 8
  ref = H_element
FEATURE [App::DocumentObjectGroupPython] O_element079  label="O_element : 040"  # scripted group (container) (typed FeaturePython)
  n = 2
  ref = O_element
FEATURE [App::DocumentObjectGroupPython] G4_PLEXIGLASS  # scripted group (container) (typed FeaturePython)
  Dunit = g/cm3
  Dvalue = 1.19
  Group = -> [C_element083,H_element077,O_element079]
  conduct = 2
  density = 1
  expand = 3
  formula = G4_PLEXIGLASS
  name = G4_PLEXIGLASS
  specific = 4
FEATURE [App::DocumentObjectGroupPython] C_element084  label="C_element : 042"  # scripted group (container) (typed FeaturePython)
  n = 1
  ref = C_element
FEATURE [App::DocumentObjectGroupPython] H_element078  label="H_element : 040"  # scripted group (container) (typed FeaturePython)
  n = 2
  ref = H_element
FEATURE [App::DocumentObjectGroupPython] O_element080  label="O_element : 041"  # scripted group (container) (typed FeaturePython)
  n = 1
  ref = O_element
FEATURE [App::DocumentObjectGroupPython] G4_POLYOXYMETHYLENE  # scripted group (container) (typed FeaturePython)
  Dunit = g/cm3
  Dvalue = 1.425
  Group = -> [C_element084,H_element078,O_element080]
  conduct = 2
  density = 1
  expand = 3
  formula = G4_POLYOXYMETHYLENE
  name = G4_POLYOXYMETHYLENE
  specific = 4
FEATURE [App::DocumentObjectGroupPython] C_element085  label="C_element : 043"  # scripted group (container) (typed FeaturePython)
  n = 2
  ref = C_element
FEATURE [App::DocumentObjectGroupPython] H_element079  label="H_element : 041"  # scripted group (container) (typed FeaturePython)
  n = 4
  ref = H_element
FEATURE [App::DocumentObjectGroupPython] G4_POLYPROPYLENE  # scripted group (container) (typed FeaturePython)
  Dunit = g/cm3
  Dvalue = 0.9
  Group = -> [C_element085,H_element079]
  conduct = 2
  density = 1
  expand = 3
  formula = G4_POLYPROPYLENE
  name = G4_POLYPROPYLENE
  specific = 4
FEATURE [App::DocumentObjectGroupPython] C_element086  label="C_element : 044"  # scripted group (container) (typed FeaturePython)
  n = 8
  ref = C_element
FEATURE [App::DocumentObjectGroupPython] H_element080  label="H_element : 042"  # scripted group (container) (typed FeaturePython)
  n = 8
  ref = H_element
FEATURE [App::DocumentObjectGroupPython] G4_POLYSTYRENE  # scripted group (container) (typed FeaturePython)
  Dunit = g/cm3
  Dvalue = 1.06
  Group = -> [C_element086,H_element080]
  conduct = 2
  density = 1
  expand = 3
  formula = G4_POLYSTYRENE
  name = G4_POLYSTYRENE
  specific = 4
FEATURE [App::DocumentObjectGroupPython] C_element087  label="C_element : 045"  # scripted group (container) (typed FeaturePython)
  n = 2
  ref = C_element
FEATURE [App::DocumentObjectGroupPython] F_element014  label="F_element : 4"  # scripted group (container) (typed FeaturePython)
  n = 4
  ref = F_element
FEATURE [App::DocumentObjectGroupPython] G4_TEFLON  # scripted group (container) (typed FeaturePython)
  Dunit = g/cm3
  Dvalue = 2.2
  Group = -> [C_element087,F_element014]
  conduct = 2
  density = 1
  expand = 3
  formula = G4_TEFLON
  name = G4_TEFLON
  specific = 4
FEATURE [App::DocumentObjectGroupPython] C_element088  label="C_element : 046"  # scripted group (container) (typed FeaturePython)
  n = 2
  ref = C_element
FEATURE [App::DocumentObjectGroupPython] F_element015  label="F_element : 006"  # scripted group (container) (typed FeaturePython)
  n = 3
  ref = F_element
FEATURE [App::DocumentObjectGroupPython] Cl_element018  label="Cl_element : 008"  # scripted group (container) (typed FeaturePython)
  n = 1
  ref = Cl_element
FEATURE [App::DocumentObjectGroupPython] G4_POLYTRIFLUOROCHLOROETHYLENE  # scripted group (container) (typed FeaturePython)
  Dunit = g/cm3
  Dvalue = 2.1
  Group = -> [C_element088,F_element015,Cl_element018]
  conduct = 2
  density = 1
  expand = 3
  formula = G4_POLYTRIFLUOROCHLOROETHYLENE
  name = G4_POLYTRIFLUOROCHLOROETHYLENE
  specific = 4
FEATURE [App::DocumentObjectGroupPython] C_element089  label="C_element : 047"  # scripted group (container) (typed FeaturePython)
  n = 4
  ref = C_element
FEATURE [App::DocumentObjectGroupPython] H_element081  label="H_element : 043"  # scripted group (container) (typed FeaturePython)
  n = 6
  ref = H_element
FEATURE [App::DocumentObjectGroupPython] O_element081  label="O_element : 042"  # scripted group (container) (typed FeaturePython)
  n = 2
  ref = O_element
FEATURE [App::DocumentObjectGroupPython] G4_POLYVINYL_ACETATE  # scripted group (container) (typed FeaturePython)
  Dunit = g/cm3
  Dvalue = 1.19
  Group = -> [C_element089,H_element081,O_element081]
  conduct = 2
  density = 1
  expand = 3
  formula = G4_POLYVINYL_ACETATE
  name = G4_POLYVINYL_ACETATE
  specific = 4
FEATURE [App::DocumentObjectGroupPython] C_element090  label="C_element : 048"  # scripted group (container) (typed FeaturePython)
  n = 2
  ref = C_element
FEATURE [App::DocumentObjectGroupPython] H_element082  label="H_element : 044"  # scripted group (container) (typed FeaturePython)
  n = 4
  ref = H_element
FEATURE [App::DocumentObjectGroupPython] O_element082  label="O_element : 043"  # scripted group (container) (typed FeaturePython)
  n = 1
  ref = O_element
FEATURE [App::DocumentObjectGroupPython] G4_POLYVINYL_ALCOHOL  # scripted group (container) (typed FeaturePython)
  Dunit = g/cm3
  Dvalue = 1.3
  Group = -> [C_element090,H_element082,O_element082]
  conduct = 2
  density = 1
  expand = 3
  formula = G4_POLYVINYL_ALCOHOL
  name = G4_POLYVINYL_ALCOHOL
  specific = 4
FEATURE [App::DocumentObjectGroupPython] C_element091  label="C_element : 049"  # scripted group (container) (typed FeaturePython)
  n = 8
  ref = C_element
FEATURE [App::DocumentObjectGroupPython] H_element083  label="H_element : 045"  # scripted group (container) (typed FeaturePython)
  n = 14
  ref = H_element
FEATURE [App::DocumentObjectGroupPython] O_element083  label="O_element : 044"  # scripted group (container) (typed FeaturePython)
  n = 2
  ref = O_element
FEATURE [App::DocumentObjectGroupPython] G4_POLYVINYL_BUTYRAL  # scripted group (container) (typed FeaturePython)
  Dunit = g/cm3
  Dvalue = 1.12
  Group = -> [C_element091,H_element083,O_element083]
  conduct = 2
  density = 1
  expand = 3
  formula = G4_POLYVINYL_BUTYRAL
  name = G4_POLYVINYL_BUTYRAL
  specific = 4
FEATURE [App::DocumentObjectGroupPython] C_element092  label="C_element : 050"  # scripted group (container) (typed FeaturePython)
  n = 2
  ref = C_element
FEATURE [App::DocumentObjectGroupPython] H_element084  label="H_element : 046"  # scripted group (container) (typed FeaturePython)
  n = 3
  ref = H_element
FEATURE [App::DocumentObjectGroupPython] Cl_element019  label="Cl_element : 009"  # scripted group (container) (typed FeaturePython)
  n = 1
  ref = Cl_element
FEATURE [App::DocumentObjectGroupPython] G4_POLYVINYL_CHLORIDE  # scripted group (container) (typed FeaturePython)
  Dunit = g/cm3
  Dvalue = 1.3
  Group = -> [C_element092,H_element084,Cl_element019]
  conduct = 2
  density = 1
  expand = 3
  formula = G4_POLYVINYL_CHLORIDE
  name = G4_POLYVINYL_CHLORIDE
  specific = 4
FEATURE [App::DocumentObjectGroupPython] C_element093  label="C_element : 051"  # scripted group (container) (typed FeaturePython)
  n = 2
  ref = C_element
FEATURE [App::DocumentObjectGroupPython] H_element085  label="H_element : 047"  # scripted group (container) (typed FeaturePython)
  n = 2
  ref = H_element
FEATURE [App::DocumentObjectGroupPython] Cl_element020  label="Cl_element : 010"  # scripted group (container) (typed FeaturePython)
  n = 2
  ref = Cl_element
FEATURE [App::DocumentObjectGroupPython] G4_POLYVINYLIDENE_CHLORIDE  # scripted group (container) (typed FeaturePython)
  Dunit = g/cm3
  Dvalue = 1.7
  Group = -> [C_element093,H_element085,Cl_element020]
  conduct = 2
  density = 1
  expand = 3
  formula = G4_POLYVINYLIDENE_CHLORIDE
  name = G4_POLYVINYLIDENE_CHLORIDE
  specific = 4
FEATURE [App::DocumentObjectGroupPython] C_element094  label="C_element : 052"  # scripted group (container) (typed FeaturePython)
  n = 2
  ref = C_element
FEATURE [App::DocumentObjectGroupPython] H_element086  label="H_element : 048"  # scripted group (container) (typed FeaturePython)
  n = 2
  ref = H_element
FEATURE [App::DocumentObjectGroupPython] F_element016  label="F_element : 007"  # scripted group (container) (typed FeaturePython)
  n = 2
  ref = F_element
FEATURE [App::DocumentObjectGroupPython] G4_POLYVINYLIDENE_FLUORIDE  # scripted group (container) (typed FeaturePython)
  Dunit = g/cm3
  Dvalue = 1.76
  Group = -> [C_element094,H_element086,F_element016]
  conduct = 2
  density = 1
  expand = 3
  formula = G4_POLYVINYLIDENE_FLUORIDE
  name = G4_POLYVINYLIDENE_FLUORIDE
  specific = 4
FEATURE [App::DocumentObjectGroupPython] C_element095  label="C_element : 053"  # scripted group (container) (typed FeaturePython)
  n = 6
  ref = C_element
FEATURE [App::DocumentObjectGroupPython] H_element087  label="H_element : 9"  # scripted group (container) (typed FeaturePython)
  n = 9
  ref = H_element
FEATURE [App::DocumentObjectGroupPython] N_element037  label="N_element : 016"  # scripted group (container) (typed FeaturePython)
  n = 1
  ref = N_element
FEATURE [App::DocumentObjectGroupPython] O_element084  label="O_element : 045"  # scripted group (container) (typed FeaturePython)
  n = 1
  ref = O_element
FEATURE [App::DocumentObjectGroupPython] G4_POLYVINYL_PYRROLIDONE  # scripted group (container) (typed FeaturePython)
  Dunit = g/cm3
  Dvalue = 1.25
  Group = -> [C_element095,H_element087,N_element037,O_element084]
  conduct = 2
  density = 1
  expand = 3
  formula = G4_POLYVINYL_PYRROLIDONE
  name = G4_POLYVINYL_PYRROLIDONE
  specific = 4
FEATURE [App::DocumentObjectGroupPython] K_element008  label="K_element : 1"  # scripted group (container) (typed FeaturePython)
  n = 1
  ref = K_element
FEATURE [App::DocumentObjectGroupPython] I_element006  label="I_element : 003"  # scripted group (container) (typed FeaturePython)
  n = 1
  ref = I_element
FEATURE [App::DocumentObjectGroupPython] G4_POTASSIUM_IODIDE  # scripted group (container) (typed FeaturePython)
  Dunit = g/cm3
  Dvalue = 3.13
  Group = -> [K_element008,I_element006]
  conduct = 2
  density = 1
  expand = 3
  formula = G4_POTASSIUM_IODIDE
  name = G4_POTASSIUM_IODIDE
  specific = 4
FEATURE [App::DocumentObjectGroupPython] K_element009  label="K_element : 2"  # scripted group (container) (typed FeaturePython)
  n = 2
  ref = K_element
FEATURE [App::DocumentObjectGroupPython] O_element085  label="O_element : 046"  # scripted group (container) (typed FeaturePython)
  n = 1
  ref = O_element
FEATURE [App::DocumentObjectGroupPython] G4_POTASSIUM_OXIDE  # scripted group (container) (typed FeaturePython)
  Dunit = g/cm3
  Dvalue = 2.32
  Group = -> [K_element009,O_element085]
  conduct = 2
  density = 1
  expand = 3
  formula = G4_POTASSIUM_OXIDE
  name = G4_POTASSIUM_OXIDE
  specific = 4
FEATURE [App::DocumentObjectGroupPython] C_element096  label="C_element : 054"  # scripted group (container) (typed FeaturePython)
  n = 3
  ref = C_element
FEATURE [App::DocumentObjectGroupPython] H_element088  label="H_element : 049"  # scripted group (container) (typed FeaturePython)
  n = 8
  ref = H_element
FEATURE [App::DocumentObjectGroupPython] G4_PROPANE  # scripted group (container) (typed FeaturePython)
  Dunit = g/cm3
  Dvalue = 0.00187939
  Group = -> [C_element096,H_element088]
  conduct = 2
  density = 1
  expand = 3
  formula = G4_PROPANE
  name = G4_PROPANE
  specific = 4
FEATURE [App::DocumentObjectGroupPython] C_element097  label="C_element : 055"  # scripted group (container) (typed FeaturePython)
  n = 3
  ref = C_element
FEATURE [App::DocumentObjectGroupPython] H_element089  label="H_element : 050"  # scripted group (container) (typed FeaturePython)
  n = 8
  ref = H_element
FEATURE [App::DocumentObjectGroupPython] G4_lPROPANE  # scripted group (container) (typed FeaturePython)
  Dunit = g/cm3
  Dvalue = 0.43
  Group = -> [C_element097,H_element089]
  conduct = 2
  density = 1
  expand = 3
  formula = G4_lPROPANE
  name = G4_lPROPANE
  specific = 4
FEATURE [App::DocumentObjectGroupPython] C_element098  label="C_element : 056"  # scripted group (container) (typed FeaturePython)
  n = 3
  ref = C_element
FEATURE [App::DocumentObjectGroupPython] H_element090  label="H_element : 051"  # scripted group (container) (typed FeaturePython)
  n = 8
  ref = H_element
FEATURE [App::DocumentObjectGroupPython] O_element086  label="O_element : 047"  # scripted group (container) (typed FeaturePython)
  n = 1
  ref = O_element
FEATURE [App::DocumentObjectGroupPython] G4_N_PROPYL_ALCOHOL  label="G4_N-PROPYL_ALCOHOL"  # scripted group (container) (typed FeaturePython)
  Dunit = g/cm3
  Dvalue = 0.8035
  Group = -> [C_element098,H_element090,O_element086]
  conduct = 2
  density = 1
  expand = 3
  formula = G4_N-PROPYL_ALCOHOL
  name = G4_N-PROPYL_ALCOHOL
  specific = 4
FEATURE [App::DocumentObjectGroupPython] C_element099  label="C_element : 057"  # scripted group (container) (typed FeaturePython)
  n = 5
  ref = C_element
FEATURE [App::DocumentObjectGroupPython] H_element091  label="H_element : 052"  # scripted group (container) (typed FeaturePython)
  n = 5
  ref = H_element
FEATURE [App::DocumentObjectGroupPython] N_element038  label="N_element : 017"  # scripted group (container) (typed FeaturePython)
  n = 1
  ref = N_element
FEATURE [App::DocumentObjectGroupPython] G4_PYRIDINE  # scripted group (container) (typed FeaturePython)
  Dunit = g/cm3
  Dvalue = 0.9819
  Group = -> [C_element099,H_element091,N_element038]
  conduct = 2
  density = 1
  expand = 3
  formula = G4_PYRIDINE
  name = G4_PYRIDINE
  specific = 4
FEATURE [App::DocumentObjectGroupPython] H_element092  label="H_element : 0.144"  # scripted group (container) (typed FeaturePython)
  n = 0.143711
FEATURE [App::DocumentObjectGroupPython] C_element100  label="C_element : 0.856"  # scripted group (container) (typed FeaturePython)
  n = 0.856289
FEATURE [App::DocumentObjectGroupPython] G4_RUBBER_BUTYL  # scripted group (container) (typed FeaturePython)
  Dunit = g/cm3
  Dvalue = 0.92
  Group = -> [H_element092,C_element100]
  conduct = 2
  density = 1
  expand = 3
  formula = G4_RUBBER_BUTYL
  name = G4_RUBBER_BUTYL
  specific = 4
FEATURE [App::DocumentObjectGroupPython] H_element093  label="H_element : 0.118"  # scripted group (container) (typed FeaturePython)
  n = 0.118371
FEATURE [App::DocumentObjectGroupPython] C_element101  label="C_element : 0.882"  # scripted group (container) (typed FeaturePython)
  n = 0.881629
FEATURE [App::DocumentObjectGroupPython] G4_RUBBER_NATURAL  # scripted group (container) (typed FeaturePython)
  Dunit = g/cm3
  Dvalue = 0.92
  Group = -> [H_element093,C_element101]
  conduct = 2
  density = 1
  expand = 3
  formula = G4_RUBBER_NATURAL
  name = G4_RUBBER_NATURAL
  specific = 4
FEATURE [App::DocumentObjectGroupPython] H_element094  label="H_element : 0.145"  # scripted group (container) (typed FeaturePython)
  n = 0.05692
FEATURE [App::DocumentObjectGroupPython] C_element102  label="C_element : 0.543"  # scripted group (container) (typed FeaturePython)
  n = 0.542646
FEATURE [App::DocumentObjectGroupPython] Cl_element021  label="Cl_element : 0.400"  # scripted group (container) (typed FeaturePython)
  n = 0.400434
FEATURE [App::DocumentObjectGroupPython] G4_RUBBER_NEOPRENE  # scripted group (container) (typed FeaturePython)
  Dunit = g/cm3
  Dvalue = 1.23
  Group = -> [H_element094,C_element102,Cl_element021]
  conduct = 2
  density = 1
  expand = 3
  formula = G4_RUBBER_NEOPRENE
  name = G4_RUBBER_NEOPRENE
  specific = 4
FEATURE [App::DocumentObjectGroupPython] Si_element006  label="Si_element : 1"  # scripted group (container) (typed FeaturePython)
  n = 1
  ref = Si_element
FEATURE [App::DocumentObjectGroupPython] O_element087  label="O_element : 048"  # scripted group (container) (typed FeaturePython)
  n = 2
  ref = O_element
FEATURE [App::DocumentObjectGroupPython] G4_SILICON_DIOXIDE  # scripted group (container) (typed FeaturePython)
  Dunit = g/cm3
  Dvalue = 2.32
  Group = -> [Si_element006,O_element087]
  conduct = 2
  density = 1
  expand = 3
  formula = G4_SILICON_DIOXIDE
  name = G4_SILICON_DIOXIDE
  specific = 4
FEATURE [App::DocumentObjectGroupPython] Ag_element002  label="Ag_element : 1"  # scripted group (container) (typed FeaturePython)
  n = 1
  ref = Ag_element
FEATURE [App::DocumentObjectGroupPython] Br_element005  label="Br_element : 003"  # scripted group (container) (typed FeaturePython)
  n = 1
  ref = Br_element
FEATURE [App::DocumentObjectGroupPython] G4_SILVER_BROMIDE  # scripted group (container) (typed FeaturePython)
  Dunit = g/cm3
  Dvalue = 6.473
  Group = -> [Ag_element002,Br_element005]
  conduct = 2
  density = 1
  expand = 3
  formula = G4_SILVER_BROMIDE
  name = G4_SILVER_BROMIDE
  specific = 4
FEATURE [App::DocumentObjectGroupPython] Ag_element003  label="Ag_element : 002"  # scripted group (container) (typed FeaturePython)
  n = 1
  ref = Ag_element
FEATURE [App::DocumentObjectGroupPython] Cl_element022  label="Cl_element : 011"  # scripted group (container) (typed FeaturePython)
  n = 1
  ref = Cl_element
FEATURE [App::DocumentObjectGroupPython] G4_SILVER_CHLORIDE  # scripted group (container) (typed FeaturePython)
  Dunit = g/cm3
  Dvalue = 5.56
  Group = -> [Ag_element003,Cl_element022]
  conduct = 2
  density = 1
  expand = 3
  formula = G4_SILVER_CHLORIDE
  name = G4_SILVER_CHLORIDE
  specific = 4
FEATURE [App::DocumentObjectGroupPython] Br_element006  label="Br_element : 0.423"  # scripted group (container) (typed FeaturePython)
  n = 0.422895
FEATURE [App::DocumentObjectGroupPython] Ag_element004  label="Ag_element : 0.574"  # scripted group (container) (typed FeaturePython)
  n = 0.573748
FEATURE [App::DocumentObjectGroupPython] I_element007  label="I_element : 0.649"  # scripted group (container) (typed FeaturePython)
  n = 0.003357
FEATURE [App::DocumentObjectGroupPython] G4_SILVER_HALIDES  # scripted group (container) (typed FeaturePython)
  Dunit = g/cm3
  Dvalue = 6.47
  Group = -> [Br_element006,Ag_element004,I_element007]
  conduct = 2
  density = 1
  expand = 3
  formula = G4_SILVER_HALIDES
  name = G4_SILVER_HALIDES
  specific = 4
FEATURE [App::DocumentObjectGroupPython] Ag_element005  label="Ag_element : 003"  # scripted group (container) (typed FeaturePython)
  n = 1
  ref = Ag_element
FEATURE [App::DocumentObjectGroupPython] I_element008  label="I_element : 004"  # scripted group (container) (typed FeaturePython)
  n = 1
  ref = I_element
FEATURE [App::DocumentObjectGroupPython] G4_SILVER_IODIDE  # scripted group (container) (typed FeaturePython)
  Dunit = g/cm3
  Dvalue = 6.01
  Group = -> [Ag_element005,I_element008]
  conduct = 2
  density = 1
  expand = 3
  formula = G4_SILVER_IODIDE
  name = G4_SILVER_IODIDE
  specific = 4
FEATURE [App::DocumentObjectGroupPython] H_element095  label="H_element : 0.100"  # scripted group (container) (typed FeaturePython)
  n = 0.1
FEATURE [App::DocumentObjectGroupPython] C_element103  label="C_element : 0.204"  # scripted group (container) (typed FeaturePython)
  n = 0.204
FEATURE [App::DocumentObjectGroupPython] N_element039  label="N_element : 0.759"  # scripted group (container) (typed FeaturePython)
  n = 0.042
FEATURE [App::DocumentObjectGroupPython] O_element088  label="O_element : 0.645"  # scripted group (container) (typed FeaturePython)
  n = 0.645
FEATURE [App::DocumentObjectGroupPython] Na_element013  label="Na_element : 0.100"  # scripted group (container) (typed FeaturePython)
  n = 0.002
FEATURE [App::DocumentObjectGroupPython] P_element009  label="P_element : 0.107"  # scripted group (container) (typed FeaturePython)
  n = 0.001
FEATURE [App::DocumentObjectGroupPython] S_element020  label="S_element : 0.021"  # scripted group (container) (typed FeaturePython)
  n = 0.002
FEATURE [App::DocumentObjectGroupPython] Cl_element023  label="Cl_element : 0.590"  # scripted group (container) (typed FeaturePython)
  n = 0.003
FEATURE [App::DocumentObjectGroupPython] K_element010  label="K_element : 0.001"  # scripted group (container) (typed FeaturePython)
  n = 0.001
FEATURE [App::DocumentObjectGroupPython] G4_SKIN_ICRP  # scripted group (container) (typed FeaturePython)
  Dunit = g/cm3
  Dvalue = 1.09
  Group = -> [H_element095,C_element103,N_element039,O_element088,Na_element013,P_element009,S_element020,Cl_element023,K_element010]
  conduct = 2
  density = 1
  expand = 3
  formula = G4_SKIN_ICRP
  name = G4_SKIN_ICRP
  specific = 4
FEATURE [App::DocumentObjectGroupPython] Na_element014  label="Na_element : 2"  # scripted group (container) (typed FeaturePython)
  n = 2
  ref = Na_element
FEATURE [App::DocumentObjectGroupPython] C_element104  label="C_element : 058"  # scripted group (container) (typed FeaturePython)
  n = 1
  ref = C_element
FEATURE [App::DocumentObjectGroupPython] O_element089  label="O_element : 049"  # scripted group (container) (typed FeaturePython)
  n = 3
  ref = O_element
FEATURE [App::DocumentObjectGroupPython] G4_SODIUM_CARBONATE  # scripted group (container) (typed FeaturePython)
  Dunit = g/cm3
  Dvalue = 2.532
  Group = -> [Na_element014,C_element104,O_element089]
  conduct = 2
  density = 1
  expand = 3
  formula = G4_SODIUM_CARBONATE
  name = G4_SODIUM_CARBONATE
  specific = 4
FEATURE [App::DocumentObjectGroupPython] Na_element015  label="Na_element : 1"  # scripted group (container) (typed FeaturePython)
  n = 1
  ref = Na_element
FEATURE [App::DocumentObjectGroupPython] I_element009  label="I_element : 005"  # scripted group (container) (typed FeaturePython)
  n = 1
  ref = I_element
FEATURE [App::DocumentObjectGroupPython] G4_SODIUM_IODIDE  # scripted group (container) (typed FeaturePython)
  Dunit = g/cm3
  Dvalue = 3.667
  Group = -> [Na_element015,I_element009]
  conduct = 2
  density = 1
  expand = 3
  formula = G4_SODIUM_IODIDE
  name = G4_SODIUM_IODIDE
  specific = 4
FEATURE [App::DocumentObjectGroupPython] Na_element016  label="Na_element : 003"  # scripted group (container) (typed FeaturePython)
  n = 2
  ref = Na_element
FEATURE [App::DocumentObjectGroupPython] O_element090  label="O_element : 050"  # scripted group (container) (typed FeaturePython)
  n = 1
  ref = O_element
FEATURE [App::DocumentObjectGroupPython] G4_SODIUM_MONOXIDE  # scripted group (container) (typed FeaturePython)
  Dunit = g/cm3
  Dvalue = 2.27
  Group = -> [Na_element016,O_element090]
  conduct = 2
  density = 1
  expand = 3
  formula = G4_SODIUM_MONOXIDE
  name = G4_SODIUM_MONOXIDE
  specific = 4
FEATURE [App::DocumentObjectGroupPython] Na_element017  label="Na_element : 004"  # scripted group (container) (typed FeaturePython)
  n = 1
  ref = Na_element
FEATURE [App::DocumentObjectGroupPython] N_element040  label="N_element : 018"  # scripted group (container) (typed FeaturePython)
  n = 1
  ref = N_element
FEATURE [App::DocumentObjectGroupPython] O_element091  label="O_element : 051"  # scripted group (container) (typed FeaturePython)
  n = 3
  ref = O_element
FEATURE [App::DocumentObjectGroupPython] G4_SODIUM_NITRATE  # scripted group (container) (typed FeaturePython)
  Dunit = g/cm3
  Dvalue = 2.261
  Group = -> [Na_element017,N_element040,O_element091]
  conduct = 2
  density = 1
  expand = 3
  formula = G4_SODIUM_NITRATE
  name = G4_SODIUM_NITRATE
  specific = 4
FEATURE [App::DocumentObjectGroupPython] C_element105  label="C_element : 059"  # scripted group (container) (typed FeaturePython)
  n = 14
  ref = C_element
FEATURE [App::DocumentObjectGroupPython] H_element096  label="H_element : 053"  # scripted group (container) (typed FeaturePython)
  n = 12
  ref = H_element
FEATURE [App::DocumentObjectGroupPython] G4_STILBENE  # scripted group (container) (typed FeaturePython)
  Dunit = g/cm3
  Dvalue = 0.9707
  Group = -> [C_element105,H_element096]
  conduct = 2
  density = 1
  expand = 3
  formula = G4_STILBENE
  name = G4_STILBENE
  specific = 4
FEATURE [App::DocumentObjectGroupPython] C_element106  label="C_element : 12"  # scripted group (container) (typed FeaturePython)
  n = 12
  ref = C_element
FEATURE [App::DocumentObjectGroupPython] H_element097  label="H_element : 22"  # scripted group (container) (typed FeaturePython)
  n = 22
  ref = H_element
FEATURE [App::DocumentObjectGroupPython] O_element092  label="O_element : 11"  # scripted group (container) (typed FeaturePython)
  n = 11
  ref = O_element
FEATURE [App::DocumentObjectGroupPython] G4_SUCROSE  # scripted group (container) (typed FeaturePython)
  Dunit = g/cm3
  Dvalue = 1.5805
  Group = -> [C_element106,H_element097,O_element092]
  conduct = 2
  density = 1
  expand = 3
  formula = G4_SUCROSE
  name = G4_SUCROSE
  specific = 4
FEATURE [App::DocumentObjectGroupPython] C_element107  label="C_element : 18"  # scripted group (container) (typed FeaturePython)
  n = 18
  ref = C_element
FEATURE [App::DocumentObjectGroupPython] H_element098  label="H_element : 054"  # scripted group (container) (typed FeaturePython)
  n = 14
  ref = H_element
FEATURE [App::DocumentObjectGroupPython] G4_TERPHENYL  # scripted group (container) (typed FeaturePython)
  Dunit = g/cm3
  Dvalue = 1.24
  Group = -> [C_element107,H_element098]
  conduct = 2
  density = 1
  expand = 3
  formula = G4_TERPHENYL
  name = G4_TERPHENYL
  specific = 4
FEATURE [App::DocumentObjectGroupPython] H_element099  label="H_element : 0.146"  # scripted group (container) (typed FeaturePython)
  n = 0.106
FEATURE [App::DocumentObjectGroupPython] C_element108  label="C_element : 0.883"  # scripted group (container) (typed FeaturePython)
  n = 0.099
FEATURE [App::DocumentObjectGroupPython] N_element041  label="N_element : 0.020"  # scripted group (container) (typed FeaturePython)
  n = 0.02
FEATURE [App::DocumentObjectGroupPython] O_element093  label="O_element : 0.766"  # scripted group (container) (typed FeaturePython)
  n = 0.766
FEATURE [App::DocumentObjectGroupPython] Na_element018  label="Na_element : 0.101"  # scripted group (container) (typed FeaturePython)
  n = 0.002
FEATURE [App::DocumentObjectGroupPython] P_element010  label="P_element : 0.108"  # scripted group (container) (typed FeaturePython)
  n = 0.001
FEATURE [App::DocumentObjectGroupPython] S_element021  label="S_element : 0.022"  # scripted group (container) (typed FeaturePython)
  n = 0.002
FEATURE [App::DocumentObjectGroupPython] Cl_element024  label="Cl_element : 0.002"  # scripted group (container) (typed FeaturePython)
  n = 0.002
FEATURE [App::DocumentObjectGroupPython] K_element011  label="K_element : 0.017"  # scripted group (container) (typed FeaturePython)
  n = 0.002
FEATURE [App::DocumentObjectGroupPython] G4_TESTIS_ICRP  # scripted group (container) (typed FeaturePython)
  Dunit = g/cm3
  Dvalue = 1.04
  Group = -> [H_element099,C_element108,N_element041,O_element093,Na_element018,P_element010,S_element021,Cl_element024,K_element011]
  conduct = 2
  density = 1
  expand = 3
  formula = G4_TESTIS_ICRP
  name = G4_TESTIS_ICRP
  specific = 4
FEATURE [App::DocumentObjectGroupPython] C_element109  label="C_element : 060"  # scripted group (container) (typed FeaturePython)
  n = 2
  ref = C_element
FEATURE [App::DocumentObjectGroupPython] Cl_element025  label="Cl_element : 012"  # scripted group (container) (typed FeaturePython)
  n = 4
  ref = Cl_element
FEATURE [App::DocumentObjectGroupPython] G4_TETRACHLOROETHYLENE  # scripted group (container) (typed FeaturePython)
  Dunit = g/cm3
  Dvalue = 1.625
  Group = -> [C_element109,Cl_element025]
  conduct = 2
  density = 1
  expand = 3
  formula = G4_TETRACHLOROETHYLENE
  name = G4_TETRACHLOROETHYLENE
  specific = 4
FEATURE [App::DocumentObjectGroupPython] Tl_element001  label="Tl_element : 1"  # scripted group (container) (typed FeaturePython)
  n = 1
  ref = Tl_element
FEATURE [App::DocumentObjectGroupPython] Cl_element026  label="Cl_element : 013"  # scripted group (container) (typed FeaturePython)
  n = 1
  ref = Cl_element
FEATURE [App::DocumentObjectGroupPython] G4_THALLIUM_CHLORIDE  # scripted group (container) (typed FeaturePython)
  Dunit = g/cm3
  Dvalue = 7.004
  Group = -> [Tl_element001,Cl_element026]
  conduct = 2
  density = 1
  expand = 3
  formula = G4_THALLIUM_CHLORIDE
  name = G4_THALLIUM_CHLORIDE
  specific = 4
FEATURE [App::DocumentObjectGroupPython] H_element100  label="H_element : 0.147"  # scripted group (container) (typed FeaturePython)
  n = 0.105
FEATURE [App::DocumentObjectGroupPython] C_element110  label="C_element : 0.256"  # scripted group (container) (typed FeaturePython)
  n = 0.256
FEATURE [App::DocumentObjectGroupPython] N_element042  label="N_element : 0.760"  # scripted group (container) (typed FeaturePython)
  n = 0.027
FEATURE [App::DocumentObjectGroupPython] O_element094  label="O_element : 0.602"  # scripted group (container) (typed FeaturePython)
  n = 0.602
FEATURE [App::DocumentObjectGroupPython] Na_element019  label="Na_element : 0.102"  # scripted group (container) (typed FeaturePython)
  n = 0.001
FEATURE [App::DocumentObjectGroupPython] P_element011  label="P_element : 0.109"  # scripted group (container) (typed FeaturePython)
  n = 0.002
FEATURE [App::DocumentObjectGroupPython] S_element022  label="S_element : 0.023"  # scripted group (container) (typed FeaturePython)
  n = 0.003
FEATURE [App::DocumentObjectGroupPython] Cl_element027  label="Cl_element : 0.591"  # scripted group (container) (typed FeaturePython)
  n = 0.002
FEATURE [App::DocumentObjectGroupPython] K_element012  label="K_element : 0.018"  # scripted group (container) (typed FeaturePython)
  n = 0.002
FEATURE [App::DocumentObjectGroupPython] G4_TISSUE_SOFT_ICRP  # scripted group (container) (typed FeaturePython)
  Dunit = g/cm3
  Dvalue = 1.03
  Group = -> [H_element100,C_element110,N_element042,O_element094,Na_element019,P_element011,S_element022,Cl_element027,K_element012]
  conduct = 2
  density = 1
  expand = 3
  formula = G4_TISSUE_SOFT_ICRP
  name = G4_TISSUE_SOFT_ICRP
  specific = 4
FEATURE [App::DocumentObjectGroupPython] H_element101  label="H_element : 0.148"  # scripted group (container) (typed FeaturePython)
  n = 0.101
FEATURE [App::DocumentObjectGroupPython] C_element111  label="C_element : 0.111"  # scripted group (container) (typed FeaturePython)
  n = 0.111
FEATURE [App::DocumentObjectGroupPython] N_element043  label="N_element : 0.026"  # scripted group (container) (typed FeaturePython)
  n = 0.026
FEATURE [App::DocumentObjectGroupPython] O_element095  label="O_element : 0.762"  # scripted group (container) (typed FeaturePython)
  n = 0.762
FEATURE [App::DocumentObjectGroupPython] G4_TISSUE_SOFT_ICRU_4  label="G4_TISSUE_SOFT_ICRU-4"  # scripted group (container) (typed FeaturePython)
  Dunit = g/cm3
  Dvalue = 1
  Group = -> [H_element101,C_element111,N_element043,O_element095]
  conduct = 2
  density = 1
  expand = 3
  formula = G4_TISSUE_SOFT_ICRU-4
  name = G4_TISSUE_SOFT_ICRU-4
  specific = 4
FEATURE [App::DocumentObjectGroupPython] H_element102  label="H_element : 0.149"  # scripted group (container) (typed FeaturePython)
  n = 0.101869
FEATURE [App::DocumentObjectGroupPython] C_element112  label="C_element : 0.456"  # scripted group (container) (typed FeaturePython)
  n = 0.456179
FEATURE [App::DocumentObjectGroupPython] N_element044  label="N_element : 0.761"  # scripted group (container) (typed FeaturePython)
  n = 0.035172
FEATURE [App::DocumentObjectGroupPython] O_element096  label="O_element : 0.407"  # scripted group (container) (typed FeaturePython)
  n = 0.40678
FEATURE [App::DocumentObjectGroupPython] G4_TISSUE_METHANE  label="G4_TISSUE-METHANE"  # scripted group (container) (typed FeaturePython)
  Dunit = g/cm3
  Dvalue = 0.00106409
  Group = -> [H_element102,C_element112,N_element044,O_element096]
  conduct = 2
  density = 1
  expand = 3
  formula = G4_TISSUE-METHANE
  name = G4_TISSUE-METHANE
  specific = 4
FEATURE [App::DocumentObjectGroupPython] H_element103  label="H_element : 0.103"  # scripted group (container) (typed FeaturePython)
  n = 0.102672
FEATURE [App::DocumentObjectGroupPython] C_element113  label="C_element : 0.569"  # scripted group (container) (typed FeaturePython)
  n = 0.56894
FEATURE [App::DocumentObjectGroupPython] N_element045  label="N_element : 0.762"  # scripted group (container) (typed FeaturePython)
  n = 0.035022
FEATURE [App::DocumentObjectGroupPython] O_element097  label="O_element : 0.293"  # scripted group (container) (typed FeaturePython)
  n = 0.293366
FEATURE [App::DocumentObjectGroupPython] G4_TISSUE_PROPANE  label="G4_TISSUE-PROPANE"  # scripted group (container) (typed FeaturePython)
  Dunit = g/cm3
  Dvalue = 0.00182628
  Group = -> [H_element103,C_element113,N_element045,O_element097]
  conduct = 2
  density = 1
  expand = 3
  formula = G4_TISSUE-PROPANE
  name = G4_TISSUE-PROPANE
  specific = 4
FEATURE [App::DocumentObjectGroupPython] Ti_element003  label="Ti_element : 1"  # scripted group (container) (typed FeaturePython)
  n = 1
  ref = Ti_element
FEATURE [App::DocumentObjectGroupPython] O_element098  label="O_element : 052"  # scripted group (container) (typed FeaturePython)
  n = 2
  ref = O_element
FEATURE [App::DocumentObjectGroupPython] G4_TITANIUM_DIOXIDE  # scripted group (container) (typed FeaturePython)
  Dunit = g/cm3
  Dvalue = 4.26
  Group = -> [Ti_element003,O_element098]
  conduct = 2
  density = 1
  expand = 3
  formula = G4_TITANIUM_DIOXIDE
  name = G4_TITANIUM_DIOXIDE
  specific = 4
FEATURE [App::DocumentObjectGroupPython] C_element114  label="C_element : 061"  # scripted group (container) (typed FeaturePython)
  n = 7
  ref = C_element
FEATURE [App::DocumentObjectGroupPython] H_element104  label="H_element : 055"  # scripted group (container) (typed FeaturePython)
  n = 8
  ref = H_element
FEATURE [App::DocumentObjectGroupPython] G4_TOLUENE  # scripted group (container) (typed FeaturePython)
  Dunit = g/cm3
  Dvalue = 0.8669
  Group = -> [C_element114,H_element104]
  conduct = 2
  density = 1
  expand = 3
  formula = G4_TOLUENE
  name = G4_TOLUENE
  specific = 4
FEATURE [App::DocumentObjectGroupPython] C_element115  label="C_element : 062"  # scripted group (container) (typed FeaturePython)
  n = 2
  ref = C_element
FEATURE [App::DocumentObjectGroupPython] H_element105  label="H_element : 056"  # scripted group (container) (typed FeaturePython)
  n = 1
  ref = H_element
FEATURE [App::DocumentObjectGroupPython] Cl_element028  label="Cl_element : 014"  # scripted group (container) (typed FeaturePython)
  n = 3
  ref = Cl_element
FEATURE [App::DocumentObjectGroupPython] G4_TRICHLOROETHYLENE  # scripted group (container) (typed FeaturePython)
  Dunit = g/cm3
  Dvalue = 1.46
  Group = -> [C_element115,H_element105,Cl_element028]
  conduct = 2
  density = 1
  expand = 3
  formula = G4_TRICHLOROETHYLENE
  name = G4_TRICHLOROETHYLENE
  specific = 4
FEATURE [App::DocumentObjectGroupPython] C_element116  label="C_element : 063"  # scripted group (container) (typed FeaturePython)
  n = 6
  ref = C_element
FEATURE [App::DocumentObjectGroupPython] H_element106  label="H_element : 15"  # scripted group (container) (typed FeaturePython)
  n = 15
  ref = H_element
FEATURE [App::DocumentObjectGroupPython] O_element099  label="O_element : 053"  # scripted group (container) (typed FeaturePython)
  n = 4
  ref = O_element
FEATURE [App::DocumentObjectGroupPython] P_element012  label="P_element : 1"  # scripted group (container) (typed FeaturePython)
  n = 1
  ref = P_element
FEATURE [App::DocumentObjectGroupPython] G4_TRIETHYL_PHOSPHATE  # scripted group (container) (typed FeaturePython)
  Dunit = g/cm3
  Dvalue = 1.07
  Group = -> [C_element116,H_element106,O_element099,P_element012]
  conduct = 2
  density = 1
  expand = 3
  formula = G4_TRIETHYL_PHOSPHATE
  name = G4_TRIETHYL_PHOSPHATE
  specific = 4
FEATURE [App::DocumentObjectGroupPython] W_element003  label="W_element : 003"  # scripted group (container) (typed FeaturePython)
  n = 1
  ref = W_element
FEATURE [App::DocumentObjectGroupPython] F_element017  label="F_element : 6"  # scripted group (container) (typed FeaturePython)
  n = 6
  ref = F_element
FEATURE [App::DocumentObjectGroupPython] G4_TUNGSTEN_HEXAFLUORIDE  # scripted group (container) (typed FeaturePython)
  Dunit = g/cm3
  Dvalue = 2.4
  Group = -> [W_element003,F_element017]
  conduct = 2
  density = 1
  expand = 3
  formula = G4_TUNGSTEN_HEXAFLUORIDE
  name = G4_TUNGSTEN_HEXAFLUORIDE
  specific = 4
FEATURE [App::DocumentObjectGroupPython] U_element001  label="U_element : 1"  # scripted group (container) (typed FeaturePython)
  n = 1
  ref = U_element
FEATURE [App::DocumentObjectGroupPython] C_element117  label="C_element : 064"  # scripted group (container) (typed FeaturePython)
  n = 2
  ref = C_element
FEATURE [App::DocumentObjectGroupPython] G4_URANIUM_DICARBIDE  # scripted group (container) (typed FeaturePython)
  Dunit = g/cm3
  Dvalue = 11.28
  Group = -> [U_element001,C_element117]
  conduct = 2
  density = 1
  expand = 3
  formula = G4_URANIUM_DICARBIDE
  name = G4_URANIUM_DICARBIDE
  specific = 4
FEATURE [App::DocumentObjectGroupPython] U_element002  label="U_element : 002"  # scripted group (container) (typed FeaturePython)
  n = 1
  ref = U_element
FEATURE [App::DocumentObjectGroupPython] C_element118  label="C_element : 065"  # scripted group (container) (typed FeaturePython)
  n = 1
  ref = C_element
FEATURE [App::DocumentObjectGroupPython] G4_URANIUM_MONOCARBIDE  # scripted group (container) (typed FeaturePython)
  Dunit = g/cm3
  Dvalue = 13.63
  Group = -> [U_element002,C_element118]
  conduct = 2
  density = 1
  expand = 3
  formula = G4_URANIUM_MONOCARBIDE
  name = G4_URANIUM_MONOCARBIDE
  specific = 4
FEATURE [App::DocumentObjectGroupPython] U_element003  label="U_element : 003"  # scripted group (container) (typed FeaturePython)
  n = 1
  ref = U_element
FEATURE [App::DocumentObjectGroupPython] O_element100  label="O_element : 054"  # scripted group (container) (typed FeaturePython)
  n = 2
  ref = O_element
FEATURE [App::DocumentObjectGroupPython] G4_URANIUM_OXIDE  # scripted group (container) (typed FeaturePython)
  Dunit = g/cm3
  Dvalue = 10.96
  Group = -> [U_element003,O_element100]
  conduct = 2
  density = 1
  expand = 3
  formula = G4_URANIUM_OXIDE
  name = G4_URANIUM_OXIDE
  specific = 4
FEATURE [App::DocumentObjectGroupPython] C_element119  label="C_element : 066"  # scripted group (container) (typed FeaturePython)
  n = 1
  ref = C_element
FEATURE [App::DocumentObjectGroupPython] H_element107  label="H_element : 057"  # scripted group (container) (typed FeaturePython)
  n = 4
  ref = H_element
FEATURE [App::DocumentObjectGroupPython] N_element046  label="N_element : 019"  # scripted group (container) (typed FeaturePython)
  n = 2
  ref = N_element
FEATURE [App::DocumentObjectGroupPython] O_element101  label="O_element : 055"  # scripted group (container) (typed FeaturePython)
  n = 1
  ref = O_element
FEATURE [App::DocumentObjectGroupPython] G4_UREA  # scripted group (container) (typed FeaturePython)
  Dunit = g/cm3
  Dvalue = 1.323
  Group = -> [C_element119,H_element107,N_element046,O_element101]
  conduct = 2
  density = 1
  expand = 3
  formula = G4_UREA
  name = G4_UREA
  specific = 4
FEATURE [App::DocumentObjectGroupPython] C_element120  label="C_element : 067"  # scripted group (container) (typed FeaturePython)
  n = 5
  ref = C_element
FEATURE [App::DocumentObjectGroupPython] H_element108  label="H_element : 058"  # scripted group (container) (typed FeaturePython)
  n = 11
  ref = H_element
FEATURE [App::DocumentObjectGroupPython] N_element047  label="N_element : 020"  # scripted group (container) (typed FeaturePython)
  n = 1
  ref = N_element
FEATURE [App::DocumentObjectGroupPython] O_element102  label="O_element : 056"  # scripted group (container) (typed FeaturePython)
  n = 2
  ref = O_element
FEATURE [App::DocumentObjectGroupPython] G4_VALINE  # scripted group (container) (typed FeaturePython)
  Dunit = g/cm3
  Dvalue = 1.23
  Group = -> [C_element120,H_element108,N_element047,O_element102]
  conduct = 2
  density = 1
  expand = 3
  formula = G4_VALINE
  name = G4_VALINE
  specific = 4
FEATURE [App::DocumentObjectGroupPython] H_element109  label="H_element : 0.009"  # scripted group (container) (typed FeaturePython)
  n = 0.009417
FEATURE [App::DocumentObjectGroupPython] C_element121  label="C_element : 0.281"  # scripted group (container) (typed FeaturePython)
  n = 0.280555
FEATURE [App::DocumentObjectGroupPython] F_element018  label="F_element : 0.710"  # scripted group (container) (typed FeaturePython)
  n = 0.710028
FEATURE [App::DocumentObjectGroupPython] G4_VITON  # scripted group (container) (typed FeaturePython)
  Dunit = g/cm3
  Dvalue = 1.8
  Group = -> [H_element109,C_element121,F_element018]
  conduct = 2
  density = 1
  expand = 3
  formula = G4_VITON
  name = G4_VITON
  specific = 4
FEATURE [App::DocumentObjectGroupPython] H_element110  label="H_element : 059"  # scripted group (container) (typed FeaturePython)
  n = 2
  ref = H_element
FEATURE [App::DocumentObjectGroupPython] O_element103  label="O_element : 057"  # scripted group (container) (typed FeaturePython)
  n = 1
  ref = O_element
FEATURE [App::DocumentObjectGroupPython] G4_WATER  # scripted group (container) (typed FeaturePython)
  Dunit = g/cm3
  Dvalue = 1
  Group = -> [H_element110,O_element103]
  conduct = 2
  density = 1
  expand = 3
  formula = G4_WATER
  name = G4_WATER
  specific = 4
FEATURE [App::DocumentObjectGroupPython] H_element111  label="H_element : 060"  # scripted group (container) (typed FeaturePython)
  n = 2
  ref = H_element
FEATURE [App::DocumentObjectGroupPython] O_element104  label="O_element : 058"  # scripted group (container) (typed FeaturePython)
  n = 1
  ref = O_element
FEATURE [App::DocumentObjectGroupPython] G4_WATER_VAPOR  # scripted group (container) (typed FeaturePython)
  Dunit = g/cm3
  Dvalue = 0.000756182
  Group = -> [H_element111,O_element104]
  conduct = 2
  density = 1
  expand = 3
  formula = G4_WATER_VAPOR
  name = G4_WATER_VAPOR
  specific = 4
FEATURE [App::DocumentObjectGroupPython] C_element122  label="C_element : 068"  # scripted group (container) (typed FeaturePython)
  n = 8
  ref = C_element
FEATURE [App::DocumentObjectGroupPython] H_element112  label="H_element : 061"  # scripted group (container) (typed FeaturePython)
  n = 10
  ref = H_element
FEATURE [App::DocumentObjectGroupPython] G4_XYLENE  # scripted group (container) (typed FeaturePython)
  Dunit = g/cm3
  Dvalue = 0.87
  Group = -> [C_element122,H_element112]
  conduct = 2
  density = 1
  expand = 3
  formula = G4_XYLENE
  name = G4_XYLENE
  specific = 4
FEATURE [App::DocumentObjectGroupPython] C_element123  label="C_element : 069"  # scripted group (container) (typed FeaturePython)
  n = 1
  ref = C_element
FEATURE [App::DocumentObjectGroupPython] G4_GRAPHITE  # scripted group (container) (typed FeaturePython)
  Dunit = g/cm3
  Dvalue = 2.21
  Group = -> [C_element123]
  conduct = 2
  density = 1
  expand = 3
  formula = G4_GRAPHITE
  name = G4_GRAPHITE
  specific = 4
FEATURE [App::DocumentObjectGroupPython] NIST  # scripted group (container) (typed FeaturePython)
  Group = -> [G4_A_150_TISSUE,G4_ACETONE,G4_ACETYLENE,G4_ADENINE,G4_ADIPOSE_TISSUE_ICRP,G4_AIR,G4_ALANINE,G4_ALUMINUM_OXIDE,G4_AMBER,G4_AMMONIA,G4_ANILINE,G4_ANTHRACENE,G4_B_100_BONE,G4_BAKELITE,G4_BARIUM_FLUORIDE,G4_BARIUM_SULFATE,G4_BENZENE,G4_BERYLLIUM_OXIDE,G4_BGO,G4_BLOOD_ICRP,G4_BONE_COMPACT_ICRU,G4_BONE_CORTICAL_ICRP,G4_BORON_CARBIDE,G4_BORON_OXIDE,G4_BRAIN_ICRP,G4_BUTANE,G4_N_BUTYL_ALCOHOL,G4_C_552,+152 more]
FEATURE [App::DocumentObjectGroupPython] H_element113  label="H_element : 062"  # scripted group (container) (typed FeaturePython)
  n = 1
  ref = H_element
FEATURE [App::DocumentObjectGroupPython] G4_H  # scripted group (container) (typed FeaturePython)
  Dunit = g/cm3
  Dvalue = 8.3748e-05
  Group = -> [H_element113]
  conduct = 2
  density = 1
  expand = 3
  formula = H
  name = G4_H
  specific = 4
FEATURE [App::DocumentObjectGroupPython] He_element001  label="He_element : 1"  # scripted group (container) (typed FeaturePython)
  n = 1
  ref = He_element
FEATURE [App::DocumentObjectGroupPython] G4_He  # scripted group (container) (typed FeaturePython)
  Dunit = g/cm3
  Dvalue = 0.000166322
  Group = -> [He_element001]
  conduct = 2
  density = 1
  expand = 3
  formula = He
  name = G4_He
  specific = 4
FEATURE [App::DocumentObjectGroupPython] Li_element008  label="Li_element : 008"  # scripted group (container) (typed FeaturePython)
  n = 1
  ref = Li_element
FEATURE [App::DocumentObjectGroupPython] G4_Li  # scripted group (container) (typed FeaturePython)
  Dunit = g/cm3
  Dvalue = 0.534
  Group = -> [Li_element008]
  conduct = 2
  density = 1
  expand = 3
  formula = Li
  name = G4_Li
  specific = 4
FEATURE [App::DocumentObjectGroupPython] Be_element002  label="Be_element : 002"  # scripted group (container) (typed FeaturePython)
  n = 1
  ref = Be_element
FEATURE [App::DocumentObjectGroupPython] G4_Be  # scripted group (container) (typed FeaturePython)
  Dunit = g/cm3
  Dvalue = 1.848
  Group = -> [Be_element002]
  conduct = 2
  density = 1
  expand = 3
  formula = Be
  name = G4_Be
  specific = 4
FEATURE [App::DocumentObjectGroupPython] B_element007  label="B_element : 007"  # scripted group (container) (typed FeaturePython)
  n = 1
  ref = B_element
FEATURE [App::DocumentObjectGroupPython] G4_B  # scripted group (container) (typed FeaturePython)
  Dunit = g/cm3
  Dvalue = 2.37
  Group = -> [B_element007]
  conduct = 2
  density = 1
  expand = 3
  formula = B
  name = G4_B
  specific = 4
FEATURE [App::DocumentObjectGroupPython] C_element124  label="C_element : 070"  # scripted group (container) (typed FeaturePython)
  n = 1
  ref = C_element
FEATURE [App::DocumentObjectGroupPython] G4_C  # scripted group (container) (typed FeaturePython)
  Dunit = g/cm3
  Dvalue = 2
  Group = -> [C_element124]
  conduct = 2
  density = 1
  expand = 3
  formula = C
  name = G4_C
  specific = 4
FEATURE [App::DocumentObjectGroupPython] N_element048  label="N_element : 021"  # scripted group (container) (typed FeaturePython)
  n = 1
  ref = N_element
FEATURE [App::DocumentObjectGroupPython] G4_N  # scripted group (container) (typed FeaturePython)
  Dunit = g/cm3
  Dvalue = 0.0011652
  Group = -> [N_element048]
  conduct = 2
  density = 1
  expand = 3
  formula = N
  name = G4_N
  specific = 4
FEATURE [App::DocumentObjectGroupPython] O_element105  label="O_element : 059"  # scripted group (container) (typed FeaturePython)
  n = 1
  ref = O_element
FEATURE [App::DocumentObjectGroupPython] G4_O  # scripted group (container) (typed FeaturePython)
  Dunit = g/cm3
  Dvalue = 0.00133151
  Group = -> [O_element105]
  conduct = 2
  density = 1
  expand = 3
  formula = O
  name = G4_O
  specific = 4
FEATURE [App::DocumentObjectGroupPython] F_element019  label="F_element : 008"  # scripted group (container) (typed FeaturePython)
  n = 1
  ref = F_element
FEATURE [App::DocumentObjectGroupPython] G4_F  # scripted group (container) (typed FeaturePython)
  Dunit = g/cm3
  Dvalue = 0.00158029
  Group = -> [F_element019]
  conduct = 2
  density = 1
  expand = 3
  formula = F
  name = G4_F
  specific = 4
FEATURE [App::DocumentObjectGroupPython] Ne_element001  label="Ne_element : 1"  # scripted group (container) (typed FeaturePython)
  n = 1
  ref = Ne_element
FEATURE [App::DocumentObjectGroupPython] G4_Ne  # scripted group (container) (typed FeaturePython)
  Dunit = g/cm3
  Dvalue = 0.000838505
  Group = -> [Ne_element001]
  conduct = 2
  density = 1
  expand = 3
  formula = Ne
  name = G4_Ne
  specific = 4
FEATURE [App::DocumentObjectGroupPython] Na_element020  label="Na_element : 005"  # scripted group (container) (typed FeaturePython)
  n = 1
  ref = Na_element
FEATURE [App::DocumentObjectGroupPython] G4_Na  # scripted group (container) (typed FeaturePython)
  Dunit = g/cm3
  Dvalue = 0.971
  Group = -> [Na_element020]
  conduct = 2
  density = 1
  expand = 3
  formula = Na
  name = G4_Na
  specific = 4
FEATURE [App::DocumentObjectGroupPython] Mg_element011  label="Mg_element : 005"  # scripted group (container) (typed FeaturePython)
  n = 1
  ref = Mg_element
FEATURE [App::DocumentObjectGroupPython] G4_Mg  # scripted group (container) (typed FeaturePython)
  Dunit = g/cm3
  Dvalue = 1.74
  Group = -> [Mg_element011]
  conduct = 2
  density = 1
  expand = 3
  formula = Mg
  name = G4_Mg
  specific = 4
FEATURE [App::DocumentObjectGroupPython] Al_element004  label="Al_element : 1"  # scripted group (container) (typed FeaturePython)
  n = 1
  ref = Al_element
FEATURE [App::DocumentObjectGroupPython] G4_Al  # scripted group (container) (typed FeaturePython)
  Dunit = g/cm3
  Dvalue = 2.699
  Group = -> [Al_element004]
  conduct = 2
  density = 1
  expand = 3
  formula = Al
  name = G4_Al
  specific = 4
FEATURE [App::DocumentObjectGroupPython] Si_element007  label="Si_element : 002"  # scripted group (container) (typed FeaturePython)
  n = 1
  ref = Si_element
FEATURE [App::DocumentObjectGroupPython] G4_Si  # scripted group (container) (typed FeaturePython)
  Dunit = g/cm3
  Dvalue = 2.33
  Group = -> [Si_element007]
  conduct = 2
  density = 1
  expand = 3
  formula = Si
  name = G4_Si
  specific = 4
FEATURE [App::DocumentObjectGroupPython] P_element013  label="P_element : 002"  # scripted group (container) (typed FeaturePython)
  n = 1
  ref = P_element
FEATURE [App::DocumentObjectGroupPython] G4_P  # scripted group (container) (typed FeaturePython)
  Dunit = g/cm3
  Dvalue = 2.2
  Group = -> [P_element013]
  conduct = 2
  density = 1
  expand = 3
  formula = P
  name = G4_P
  specific = 4
FEATURE [App::DocumentObjectGroupPython] S_element023  label="S_element : 007"  # scripted group (container) (typed FeaturePython)
  n = 1
  ref = S_element
FEATURE [App::DocumentObjectGroupPython] G4_S  # scripted group (container) (typed FeaturePython)
  Dunit = g/cm3
  Dvalue = 2
  Group = -> [S_element023]
  conduct = 2
  density = 1
  expand = 3
  formula = S
  name = G4_S
  specific = 4
FEATURE [App::DocumentObjectGroupPython] Cl_element029  label="Cl_element : 015"  # scripted group (container) (typed FeaturePython)
  n = 1
  ref = Cl_element
FEATURE [App::DocumentObjectGroupPython] G4_Cl  # scripted group (container) (typed FeaturePython)
  Dunit = g/cm3
  Dvalue = 0.00299473
  Group = -> [Cl_element029]
  conduct = 2
  density = 1
  expand = 3
  formula = Cl
  name = G4_Cl
  specific = 4
FEATURE [App::DocumentObjectGroupPython] Ar_element002  label="Ar_element : 1"  # scripted group (container) (typed FeaturePython)
  n = 1
  ref = Ar_element
FEATURE [App::DocumentObjectGroupPython] G4_Ar  # scripted group (container) (typed FeaturePython)
  Dunit = g/cm3
  Dvalue = 0.00166201
  Group = -> [Ar_element002]
  conduct = 2
  density = 1
  expand = 3
  formula = Ar
  name = G4_Ar
  specific = 4
FEATURE [App::DocumentObjectGroupPython] K_element013  label="K_element : 003"  # scripted group (container) (typed FeaturePython)
  n = 1
  ref = K_element
FEATURE [App::DocumentObjectGroupPython] G4_K  # scripted group (container) (typed FeaturePython)
  Dunit = g/cm3
  Dvalue = 0.862
  Group = -> [K_element013]
  conduct = 2
  density = 1
  expand = 3
  formula = K
  name = G4_K
  specific = 4
FEATURE [App::DocumentObjectGroupPython] Ca_element014  label="Ca_element : 007"  # scripted group (container) (typed FeaturePython)
  n = 1
  ref = Ca_element
FEATURE [App::DocumentObjectGroupPython] G4_Ca  # scripted group (container) (typed FeaturePython)
  Dunit = g/cm3
  Dvalue = 1.55
  Group = -> [Ca_element014]
  conduct = 2
  density = 1
  expand = 3
  formula = Ca
  name = G4_Ca
  specific = 4
FEATURE [App::DocumentObjectGroupPython] Sc_element001  label="Sc_element : 1"  # scripted group (container) (typed FeaturePython)
  n = 1
  ref = Sc_element
FEATURE [App::DocumentObjectGroupPython] G4_Sc  # scripted group (container) (typed FeaturePython)
  Dunit = g/cm3
  Dvalue = 2.989
  Group = -> [Sc_element001]
  conduct = 2
  density = 1
  expand = 3
  formula = Sc
  name = G4_Sc
  specific = 4
FEATURE [App::DocumentObjectGroupPython] Ti_element004  label="Ti_element : 002"  # scripted group (container) (typed FeaturePython)
  n = 1
  ref = Ti_element
FEATURE [App::DocumentObjectGroupPython] G4_Ti  # scripted group (container) (typed FeaturePython)
  Dunit = g/cm3
  Dvalue = 4.54
  Group = -> [Ti_element004]
  conduct = 2
  density = 1
  expand = 3
  formula = Ti
  name = G4_Ti
  specific = 4
FEATURE [App::DocumentObjectGroupPython] V_element001  label="V_element : 1"  # scripted group (container) (typed FeaturePython)
  n = 1
  ref = V_element
FEATURE [App::DocumentObjectGroupPython] G4_V  # scripted group (container) (typed FeaturePython)
  Dunit = g/cm3
  Dvalue = 6.11
  Group = -> [V_element001]
  conduct = 2
  density = 1
  expand = 3
  formula = V
  name = G4_V
  specific = 4
FEATURE [App::DocumentObjectGroupPython] Cr_element001  label="Cr_element : 1"  # scripted group (container) (typed FeaturePython)
  n = 1
  ref = Cr_element
FEATURE [App::DocumentObjectGroupPython] G4_Cr  # scripted group (container) (typed FeaturePython)
  Dunit = g/cm3
  Dvalue = 7.18
  Group = -> [Cr_element001]
  conduct = 2
  density = 1
  expand = 3
  formula = Cr
  name = G4_Cr
  specific = 4
FEATURE [App::DocumentObjectGroupPython] Mn_element001  label="Mn_element : 1"  # scripted group (container) (typed FeaturePython)
  n = 1
  ref = Mn_element
FEATURE [App::DocumentObjectGroupPython] G4_Mn  # scripted group (container) (typed FeaturePython)
  Dunit = g/cm3
  Dvalue = 7.44
  Group = -> [Mn_element001]
  conduct = 2
  density = 1
  expand = 3
  formula = Mn
  name = G4_Mn
  specific = 4
FEATURE [App::DocumentObjectGroupPython] Fe_element007  label="Fe_element : 004"  # scripted group (container) (typed FeaturePython)
  n = 1
  ref = Fe_element
FEATURE [App::DocumentObjectGroupPython] G4_Fe  # scripted group (container) (typed FeaturePython)
  Dunit = g/cm3
  Dvalue = 7.874
  Group = -> [Fe_element007]
  conduct = 2
  density = 1
  expand = 3
  formula = Fe
  name = G4_Fe
  specific = 4
FEATURE [App::DocumentObjectGroupPython] Co_element001  label="Co_element : 1"  # scripted group (container) (typed FeaturePython)
  n = 1
  ref = Co_element
FEATURE [App::DocumentObjectGroupPython] G4_Co  # scripted group (container) (typed FeaturePython)
  Dunit = g/cm3
  Dvalue = 8.9
  Group = -> [Co_element001]
  conduct = 2
  density = 1
  expand = 3
  formula = Co
  name = G4_Co
  specific = 4
FEATURE [App::DocumentObjectGroupPython] Ni_element001  label="Ni_element : 1"  # scripted group (container) (typed FeaturePython)
  n = 1
  ref = Ni_element
FEATURE [App::DocumentObjectGroupPython] G4_Ni  # scripted group (container) (typed FeaturePython)
  Dunit = g/cm3
  Dvalue = 8.902
  Group = -> [Ni_element001]
  conduct = 2
  density = 1
  expand = 3
  formula = Ni
  name = G4_Ni
  specific = 4
FEATURE [App::DocumentObjectGroupPython] Cu_element001  label="Cu_element : 1"  # scripted group (container) (typed FeaturePython)
  n = 1
  ref = Cu_element
FEATURE [App::DocumentObjectGroupPython] G4_Cu  # scripted group (container) (typed FeaturePython)
  Dunit = g/cm3
  Dvalue = 8.96
  Group = -> [Cu_element001]
  conduct = 2
  density = 1
  expand = 3
  formula = Cu
  name = G4_Cu
  specific = 4
FEATURE [App::DocumentObjectGroupPython] Zn_element001  label="Zn_element : 1"  # scripted group (container) (typed FeaturePython)
  n = 1
  ref = Zn_element
FEATURE [App::DocumentObjectGroupPython] G4_Zn  # scripted group (container) (typed FeaturePython)
  Dunit = g/cm3
  Dvalue = 7.133
  Group = -> [Zn_element001]
  conduct = 2
  density = 1
  expand = 3
  formula = Zn
  name = G4_Zn
  specific = 4
FEATURE [App::DocumentObjectGroupPython] Ga_element002  label="Ga_element : 002"  # scripted group (container) (typed FeaturePython)
  n = 1
  ref = Ga_element
FEATURE [App::DocumentObjectGroupPython] G4_Ga  # scripted group (container) (typed FeaturePython)
  Dunit = g/cm3
  Dvalue = 5.904
  Group = -> [Ga_element002]
  conduct = 2
  density = 1
  expand = 3
  formula = Ga
  name = G4_Ga
  specific = 4
FEATURE [App::DocumentObjectGroupPython] Ge_element002  label="Ge_element : 1"  # scripted group (container) (typed FeaturePython)
  n = 1
  ref = Ge_element
FEATURE [App::DocumentObjectGroupPython] G4_Ge  # scripted group (container) (typed FeaturePython)
  Dunit = g/cm3
  Dvalue = 5.323
  Group = -> [Ge_element002]
  conduct = 2
  density = 1
  expand = 3
  formula = Ge
  name = G4_Ge
  specific = 4
FEATURE [App::DocumentObjectGroupPython] As_element003  label="As_element : 002"  # scripted group (container) (typed FeaturePython)
  n = 1
  ref = As_element
FEATURE [App::DocumentObjectGroupPython] G4_As  # scripted group (container) (typed FeaturePython)
  Dunit = g/cm3
  Dvalue = 5.73
  Group = -> [As_element003]
  conduct = 2
  density = 1
  expand = 3
  formula = As
  name = G4_As
  specific = 4
FEATURE [App::DocumentObjectGroupPython] Se_element001  label="Se_element : 1"  # scripted group (container) (typed FeaturePython)
  n = 1
  ref = Se_element
FEATURE [App::DocumentObjectGroupPython] G4_Se  # scripted group (container) (typed FeaturePython)
  Dunit = g/cm3
  Dvalue = 4.5
  Group = -> [Se_element001]
  conduct = 2
  density = 1
  expand = 3
  formula = Se
  name = G4_Se
  specific = 4
FEATURE [App::DocumentObjectGroupPython] Br_element007  label="Br_element : 004"  # scripted group (container) (typed FeaturePython)
  n = 1
  ref = Br_element
FEATURE [App::DocumentObjectGroupPython] G4_Br  # scripted group (container) (typed FeaturePython)
  Dunit = g/cm3
  Dvalue = 0.0070721
  Group = -> [Br_element007]
  conduct = 2
  density = 1
  expand = 3
  formula = Br
  name = G4_Br
  specific = 4
FEATURE [App::DocumentObjectGroupPython] Kr_element001  label="Kr_element : 1"  # scripted group (container) (typed FeaturePython)
  n = 1
  ref = Kr_element
FEATURE [App::DocumentObjectGroupPython] G4_Kr  # scripted group (container) (typed FeaturePython)
  Dunit = g/cm3
  Dvalue = 0.00347832
  Group = -> [Kr_element001]
  conduct = 2
  density = 1
  expand = 3
  formula = Kr
  name = G4_Kr
  specific = 4
FEATURE [App::DocumentObjectGroupPython] Rb_element001  label="Rb_element : 1"  # scripted group (container) (typed FeaturePython)
  n = 1
  ref = Rb_element
FEATURE [App::DocumentObjectGroupPython] G4_Rb  # scripted group (container) (typed FeaturePython)
  Dunit = g/cm3
  Dvalue = 1.532
  Group = -> [Rb_element001]
  conduct = 2
  density = 1
  expand = 3
  formula = Rb
  name = G4_Rb
  specific = 4
FEATURE [App::DocumentObjectGroupPython] Sr_element001  label="Sr_element : 1"  # scripted group (container) (typed FeaturePython)
  n = 1
  ref = Sr_element
FEATURE [App::DocumentObjectGroupPython] G4_Sr  # scripted group (container) (typed FeaturePython)
  Dunit = g/cm3
  Dvalue = 2.54
  Group = -> [Sr_element001]
  conduct = 2
  density = 1
  expand = 3
  formula = Sr
  name = G4_Sr
  specific = 4
FEATURE [App::DocumentObjectGroupPython] Y_element001  label="Y_element : 1"  # scripted group (container) (typed FeaturePython)
  n = 1
  ref = Y_element
FEATURE [App::DocumentObjectGroupPython] G4_Y  # scripted group (container) (typed FeaturePython)
  Dunit = g/cm3
  Dvalue = 4.469
  Group = -> [Y_element001]
  conduct = 2
  density = 1
  expand = 3
  formula = Y
  name = G4_Y
  specific = 4
FEATURE [App::DocumentObjectGroupPython] Zr_element001  label="Zr_element : 1"  # scripted group (container) (typed FeaturePython)
  n = 1
  ref = Zr_element
FEATURE [App::DocumentObjectGroupPython] G4_Zr  # scripted group (container) (typed FeaturePython)
  Dunit = g/cm3
  Dvalue = 6.506
  Group = -> [Zr_element001]
  conduct = 2
  density = 1
  expand = 3
  formula = Zr
  name = G4_Zr
  specific = 4
FEATURE [App::DocumentObjectGroupPython] Nb_element001  label="Nb_element : 1"  # scripted group (container) (typed FeaturePython)
  n = 1
  ref = Nb_element
FEATURE [App::DocumentObjectGroupPython] G4_Nb  # scripted group (container) (typed FeaturePython)
  Dunit = g/cm3
  Dvalue = 8.57
  Group = -> [Nb_element001]
  conduct = 2
  density = 1
  expand = 3
  formula = Nb
  name = G4_Nb
  specific = 4
FEATURE [App::DocumentObjectGroupPython] Mo_element001  label="Mo_element : 1"  # scripted group (container) (typed FeaturePython)
  n = 1
  ref = Mo_element
FEATURE [App::DocumentObjectGroupPython] G4_Mo  # scripted group (container) (typed FeaturePython)
  Dunit = g/cm3
  Dvalue = 10.22
  Group = -> [Mo_element001]
  conduct = 2
  density = 1
  expand = 3
  formula = Mo
  name = G4_Mo
  specific = 4
FEATURE [App::DocumentObjectGroupPython] Tc_element001  label="Tc_element : 1"  # scripted group (container) (typed FeaturePython)
  n = 1
  ref = Tc_element
FEATURE [App::DocumentObjectGroupPython] G4_Tc  # scripted group (container) (typed FeaturePython)
  Dunit = g/cm3
  Dvalue = 11.5
  Group = -> [Tc_element001]
  conduct = 2
  density = 1
  expand = 3
  formula = Tc
  name = G4_Tc
  specific = 4
FEATURE [App::DocumentObjectGroupPython] Ru_element001  label="Ru_element : 1"  # scripted group (container) (typed FeaturePython)
  n = 1
  ref = Ru_element
FEATURE [App::DocumentObjectGroupPython] G4_Ru  # scripted group (container) (typed FeaturePython)
  Dunit = g/cm3
  Dvalue = 12.41
  Group = -> [Ru_element001]
  conduct = 2
  density = 1
  expand = 3
  formula = Ru
  name = G4_Ru
  specific = 4
FEATURE [App::DocumentObjectGroupPython] Rh_element001  label="Rh_element : 1"  # scripted group (container) (typed FeaturePython)
  n = 1
  ref = Rh_element
FEATURE [App::DocumentObjectGroupPython] G4_Rh  # scripted group (container) (typed FeaturePython)
  Dunit = g/cm3
  Dvalue = 12.41
  Group = -> [Rh_element001]
  conduct = 2
  density = 1
  expand = 3
  formula = Rh
  name = G4_Rh
  specific = 4
FEATURE [App::DocumentObjectGroupPython] Pd_element001  label="Pd_element : 1"  # scripted group (container) (typed FeaturePython)
  n = 1
  ref = Pd_element
FEATURE [App::DocumentObjectGroupPython] G4_Pd  # scripted group (container) (typed FeaturePython)
  Dunit = g/cm3
  Dvalue = 12.02
  Group = -> [Pd_element001]
  conduct = 2
  density = 1
  expand = 3
  formula = Pd
  name = G4_Pd
  specific = 4
FEATURE [App::DocumentObjectGroupPython] Ag_element006  label="Ag_element : 004"  # scripted group (container) (typed FeaturePython)
  n = 1
  ref = Ag_element
FEATURE [App::DocumentObjectGroupPython] G4_Ag  # scripted group (container) (typed FeaturePython)
  Dunit = g/cm3
  Dvalue = 10.5
  Group = -> [Ag_element006]
  conduct = 2
  density = 1
  expand = 3
  formula = Ag
  name = G4_Ag
  specific = 4
FEATURE [App::DocumentObjectGroupPython] Cd_element003  label="Cd_element : 003"  # scripted group (container) (typed FeaturePython)
  n = 1
  ref = Cd_element
FEATURE [App::DocumentObjectGroupPython] G4_Cd  # scripted group (container) (typed FeaturePython)
  Dunit = g/cm3
  Dvalue = 8.65
  Group = -> [Cd_element003]
  conduct = 2
  density = 1
  expand = 3
  formula = Cd
  name = G4_Cd
  specific = 4
FEATURE [App::DocumentObjectGroupPython] In_element001  label="In_element : 1"  # scripted group (container) (typed FeaturePython)
  n = 1
  ref = In_element
FEATURE [App::DocumentObjectGroupPython] G4_In  # scripted group (container) (typed FeaturePython)
  Dunit = g/cm3
  Dvalue = 7.31
  Group = -> [In_element001]
  conduct = 2
  density = 1
  expand = 3
  formula = In
  name = G4_In
  specific = 4
FEATURE [App::DocumentObjectGroupPython] Sn_element001  label="Sn_element : 1"  # scripted group (container) (typed FeaturePython)
  n = 1
  ref = Sn_element
FEATURE [App::DocumentObjectGroupPython] G4_Sn  # scripted group (container) (typed FeaturePython)
  Dunit = g/cm3
  Dvalue = 7.31
  Group = -> [Sn_element001]
  conduct = 2
  density = 1
  expand = 3
  formula = Sn
  name = G4_Sn
  specific = 4
FEATURE [App::DocumentObjectGroupPython] Sb_element001  label="Sb_element : 1"  # scripted group (container) (typed FeaturePython)
  n = 1
  ref = Sb_element
FEATURE [App::DocumentObjectGroupPython] G4_Sb  # scripted group (container) (typed FeaturePython)
  Dunit = g/cm3
  Dvalue = 6.691
  Group = -> [Sb_element001]
  conduct = 2
  density = 1
  expand = 3
  formula = Sb
  name = G4_Sb
  specific = 4
FEATURE [App::DocumentObjectGroupPython] Te_element002  label="Te_element : 002"  # scripted group (container) (typed FeaturePython)
  n = 1
  ref = Te_element
FEATURE [App::DocumentObjectGroupPython] G4_Te  # scripted group (container) (typed FeaturePython)
  Dunit = g/cm3
  Dvalue = 6.24
  Group = -> [Te_element002]
  conduct = 2
  density = 1
  expand = 3
  formula = Te
  name = G4_Te
  specific = 4
FEATURE [App::DocumentObjectGroupPython] I_element010  label="I_element : 006"  # scripted group (container) (typed FeaturePython)
  n = 1
  ref = I_element
FEATURE [App::DocumentObjectGroupPython] G4_I  # scripted group (container) (typed FeaturePython)
  Dunit = g/cm3
  Dvalue = 4.93
  Group = -> [I_element010]
  conduct = 2
  density = 1
  expand = 3
  formula = I
  name = G4_I
  specific = 4
FEATURE [App::DocumentObjectGroupPython] Xe_element001  label="Xe_element : 1"  # scripted group (container) (typed FeaturePython)
  n = 1
  ref = Xe_element
FEATURE [App::DocumentObjectGroupPython] G4_Xe  # scripted group (container) (typed FeaturePython)
  Dunit = g/cm3
  Dvalue = 0.00548536
  Group = -> [Xe_element001]
  conduct = 2
  density = 1
  expand = 3
  formula = Xe
  name = G4_Xe
  specific = 4
FEATURE [App::DocumentObjectGroupPython] Cs_element003  label="Cs_element : 003"  # scripted group (container) (typed FeaturePython)
  n = 1
  ref = Cs_element
FEATURE [App::DocumentObjectGroupPython] G4_Cs  # scripted group (container) (typed FeaturePython)
  Dunit = g/cm3
  Dvalue = 1.873
  Group = -> [Cs_element003]
  conduct = 2
  density = 1
  expand = 3
  formula = Cs
  name = G4_Cs
  specific = 4
FEATURE [App::DocumentObjectGroupPython] Ba_element003  label="Ba_element : 003"  # scripted group (container) (typed FeaturePython)
  n = 1
  ref = Ba_element
FEATURE [App::DocumentObjectGroupPython] G4_Ba  # scripted group (container) (typed FeaturePython)
  Dunit = g/cm3
  Dvalue = 3.5
  Group = -> [Ba_element003]
  conduct = 2
  density = 1
  expand = 3
  formula = Ba
  name = G4_Ba
  specific = 4
FEATURE [App::DocumentObjectGroupPython] La_element003  label="La_element : 003"  # scripted group (container) (typed FeaturePython)
  n = 1
  ref = La_element
FEATURE [App::DocumentObjectGroupPython] G4_La  # scripted group (container) (typed FeaturePython)
  Dunit = g/cm3
  Dvalue = 6.154
  Group = -> [La_element003]
  conduct = 2
  density = 1
  expand = 3
  formula = La
  name = G4_La
  specific = 4
FEATURE [App::DocumentObjectGroupPython] Ce_element002  label="Ce_element : 1"  # scripted group (container) (typed FeaturePython)
  n = 1
  ref = Ce_element
FEATURE [App::DocumentObjectGroupPython] G4_Ce  # scripted group (container) (typed FeaturePython)
  Dunit = g/cm3
  Dvalue = 6.657
  Group = -> [Ce_element002]
  conduct = 2
  density = 1
  expand = 3
  formula = Ce
  name = G4_Ce
  specific = 4
FEATURE [App::DocumentObjectGroupPython] Pr_element001  label="Pr_element : 1"  # scripted group (container) (typed FeaturePython)
  n = 1
  ref = Pr_element
FEATURE [App::DocumentObjectGroupPython] G4_Pr  # scripted group (container) (typed FeaturePython)
  Dunit = g/cm3
  Dvalue = 6.71
  Group = -> [Pr_element001]
  conduct = 2
  density = 1
  expand = 3
  formula = Pr
  name = G4_Pr
  specific = 4
FEATURE [App::DocumentObjectGroupPython] Nd_element001  label="Nd_element : 1"  # scripted group (container) (typed FeaturePython)
  n = 1
  ref = Nd_element
FEATURE [App::DocumentObjectGroupPython] G4_Nd  # scripted group (container) (typed FeaturePython)
  Dunit = g/cm3
  Dvalue = 6.9
  Group = -> [Nd_element001]
  conduct = 2
  density = 1
  expand = 3
  formula = Nd
  name = G4_Nd
  specific = 4
FEATURE [App::DocumentObjectGroupPython] Pm_element001  label="Pm_element : 1"  # scripted group (container) (typed FeaturePython)
  n = 1
  ref = Pm_element
FEATURE [App::DocumentObjectGroupPython] G4_Pm  # scripted group (container) (typed FeaturePython)
  Dunit = g/cm3
  Dvalue = 7.22
  Group = -> [Pm_element001]
  conduct = 2
  density = 1
  expand = 3
  formula = Pm
  name = G4_Pm
  specific = 4
FEATURE [App::DocumentObjectGroupPython] Sm_element001  label="Sm_element : 1"  # scripted group (container) (typed FeaturePython)
  n = 1
  ref = Sm_element
FEATURE [App::DocumentObjectGroupPython] G4_Sm  # scripted group (container) (typed FeaturePython)
  Dunit = g/cm3
  Dvalue = 7.46
  Group = -> [Sm_element001]
  conduct = 2
  density = 1
  expand = 3
  formula = Sm
  name = G4_Sm
  specific = 4
FEATURE [App::DocumentObjectGroupPython] Eu_element001  label="Eu_element : 1"  # scripted group (container) (typed FeaturePython)
  n = 1
  ref = Eu_element
FEATURE [App::DocumentObjectGroupPython] G4_Eu  # scripted group (container) (typed FeaturePython)
  Dunit = g/cm3
  Dvalue = 5.243
  Group = -> [Eu_element001]
  conduct = 2
  density = 1
  expand = 3
  formula = Eu
  name = G4_Eu
  specific = 4
FEATURE [App::DocumentObjectGroupPython] Gd_element002  label="Gd_element : 1"  # scripted group (container) (typed FeaturePython)
  n = 1
  ref = Gd_element
FEATURE [App::DocumentObjectGroupPython] G4_Gd  # scripted group (container) (typed FeaturePython)
  Dunit = g/cm3
  Dvalue = 7.9004
  Group = -> [Gd_element002]
  conduct = 2
  density = 1
  expand = 3
  formula = Gd
  name = G4_Gd
  specific = 4
FEATURE [App::DocumentObjectGroupPython] Tb_element001  label="Tb_element : 1"  # scripted group (container) (typed FeaturePython)
  n = 1
  ref = Tb_element
FEATURE [App::DocumentObjectGroupPython] G4_Tb  # scripted group (container) (typed FeaturePython)
  Dunit = g/cm3
  Dvalue = 8.229
  Group = -> [Tb_element001]
  conduct = 2
  density = 1
  expand = 3
  formula = Tb
  name = G4_Tb
  specific = 4
FEATURE [App::DocumentObjectGroupPython] Dy_element001  label="Dy_element : 1"  # scripted group (container) (typed FeaturePython)
  n = 1
  ref = Dy_element
FEATURE [App::DocumentObjectGroupPython] G4_Dy  # scripted group (container) (typed FeaturePython)
  Dunit = g/cm3
  Dvalue = 8.55
  Group = -> [Dy_element001]
  conduct = 2
  density = 1
  expand = 3
  formula = Dy
  name = G4_Dy
  specific = 4
FEATURE [App::DocumentObjectGroupPython] Ho_element001  label="Ho_element : 1"  # scripted group (container) (typed FeaturePython)
  n = 1
  ref = Ho_element
FEATURE [App::DocumentObjectGroupPython] G4_Ho  # scripted group (container) (typed FeaturePython)
  Dunit = g/cm3
  Dvalue = 8.795
  Group = -> [Ho_element001]
  conduct = 2
  density = 1
  expand = 3
  formula = Ho
  name = G4_Ho
  specific = 4
FEATURE [App::DocumentObjectGroupPython] Er_element001  label="Er_element : 1"  # scripted group (container) (typed FeaturePython)
  n = 1
  ref = Er_element
FEATURE [App::DocumentObjectGroupPython] G4_Er  # scripted group (container) (typed FeaturePython)
  Dunit = g/cm3
  Dvalue = 9.066
  Group = -> [Er_element001]
  conduct = 2
  density = 1
  expand = 3
  formula = Er
  name = G4_Er
  specific = 4
FEATURE [App::DocumentObjectGroupPython] Tm_element001  label="Tm_element : 1"  # scripted group (container) (typed FeaturePython)
  n = 1
  ref = Tm_element
FEATURE [App::DocumentObjectGroupPython] G4_Tm  # scripted group (container) (typed FeaturePython)
  Dunit = g/cm3
  Dvalue = 9.321
  Group = -> [Tm_element001]
  conduct = 2
  density = 1
  expand = 3
  formula = Tm
  name = G4_Tm
  specific = 4
FEATURE [App::DocumentObjectGroupPython] Yb_element001  label="Yb_element : 1"  # scripted group (container) (typed FeaturePython)
  n = 1
  ref = Yb_element
FEATURE [App::DocumentObjectGroupPython] G4_Yb  # scripted group (container) (typed FeaturePython)
  Dunit = g/cm3
  Dvalue = 6.73
  Group = -> [Yb_element001]
  conduct = 2
  density = 1
  expand = 3
  formula = Yb
  name = G4_Yb
  specific = 4
FEATURE [App::DocumentObjectGroupPython] Lu_element001  label="Lu_element : 1"  # scripted group (container) (typed FeaturePython)
  n = 1
  ref = Lu_element
FEATURE [App::DocumentObjectGroupPython] G4_Lu  # scripted group (container) (typed FeaturePython)
  Dunit = g/cm3
  Dvalue = 9.84
  Group = -> [Lu_element001]
  conduct = 2
  density = 1
  expand = 3
  formula = Lu
  name = G4_Lu
  specific = 4
FEATURE [App::DocumentObjectGroupPython] Hf_element001  label="Hf_element : 1"  # scripted group (container) (typed FeaturePython)
  n = 1
  ref = Hf_element
FEATURE [App::DocumentObjectGroupPython] G4_Hf  # scripted group (container) (typed FeaturePython)
  Dunit = g/cm3
  Dvalue = 13.31
  Group = -> [Hf_element001]
  conduct = 2
  density = 1
  expand = 3
  formula = Hf
  name = G4_Hf
  specific = 4
FEATURE [App::DocumentObjectGroupPython] Ta_element001  label="Ta_element : 1"  # scripted group (container) (typed FeaturePython)
  n = 1
  ref = Ta_element
FEATURE [App::DocumentObjectGroupPython] G4_Ta  # scripted group (container) (typed FeaturePython)
  Dunit = g/cm3
  Dvalue = 16.654
  Group = -> [Ta_element001]
  conduct = 2
  density = 1
  expand = 3
  formula = Ta
  name = G4_Ta
  specific = 4
FEATURE [App::DocumentObjectGroupPython] W_element004  label="W_element : 004"  # scripted group (container) (typed FeaturePython)
  n = 1
  ref = W_element
FEATURE [App::DocumentObjectGroupPython] G4_W  # scripted group (container) (typed FeaturePython)
  Dunit = g/cm3
  Dvalue = 19.3
  Group = -> [W_element004]
  conduct = 2
  density = 1
  expand = 3
  formula = W
  name = G4_W
  specific = 4
FEATURE [App::DocumentObjectGroupPython] Re_element001  label="Re_element : 1"  # scripted group (container) (typed FeaturePython)
  n = 1
  ref = Re_element
FEATURE [App::DocumentObjectGroupPython] G4_Re  # scripted group (container) (typed FeaturePython)
  Dunit = g/cm3
  Dvalue = 21.02
  Group = -> [Re_element001]
  conduct = 2
  density = 1
  expand = 3
  formula = Re
  name = G4_Re
  specific = 4
FEATURE [App::DocumentObjectGroupPython] Os_element001  label="Os_element : 1"  # scripted group (container) (typed FeaturePython)
  n = 1
  ref = Os_element
FEATURE [App::DocumentObjectGroupPython] G4_Os  # scripted group (container) (typed FeaturePython)
  Dunit = g/cm3
  Dvalue = 22.57
  Group = -> [Os_element001]
  conduct = 2
  density = 1
  expand = 3
  formula = Os
  name = G4_Os
  specific = 4
FEATURE [App::DocumentObjectGroupPython] Ir_element001  label="Ir_element : 1"  # scripted group (container) (typed FeaturePython)
  n = 1
  ref = Ir_element
FEATURE [App::DocumentObjectGroupPython] G4_Ir  # scripted group (container) (typed FeaturePython)
  Dunit = g/cm3
  Dvalue = 22.42
  Group = -> [Ir_element001]
  conduct = 2
  density = 1
  expand = 3
  formula = Ir
  name = G4_Ir
  specific = 4
FEATURE [App::DocumentObjectGroupPython] Pt_element001  label="Pt_element : 1"  # scripted group (container) (typed FeaturePython)
  n = 1
  ref = Pt_element
FEATURE [App::DocumentObjectGroupPython] G4_Pt  # scripted group (container) (typed FeaturePython)
  Dunit = g/cm3
  Dvalue = 21.45
  Group = -> [Pt_element001]
  conduct = 2
  density = 1
  expand = 3
  formula = Pt
  name = G4_Pt
  specific = 4
FEATURE [App::DocumentObjectGroupPython] Au_element001  label="Au_element : 1"  # scripted group (container) (typed FeaturePython)
  n = 1
  ref = Au_element
FEATURE [App::DocumentObjectGroupPython] G4_Au  # scripted group (container) (typed FeaturePython)
  Dunit = g/cm3
  Dvalue = 19.32
  Group = -> [Au_element001]
  conduct = 2
  density = 1
  expand = 3
  formula = Au
  name = G4_Au
  specific = 4
FEATURE [App::DocumentObjectGroupPython] Hg_element002  label="Hg_element : 002"  # scripted group (container) (typed FeaturePython)
  n = 1
  ref = Hg_element
FEATURE [App::DocumentObjectGroupPython] G4_Hg  # scripted group (container) (typed FeaturePython)
  Dunit = g/cm3
  Dvalue = 13.546
  Group = -> [Hg_element002]
  conduct = 2
  density = 1
  expand = 3
  formula = Hg
  name = G4_Hg
  specific = 4
FEATURE [App::DocumentObjectGroupPython] Tl_element002  label="Tl_element : 002"  # scripted group (container) (typed FeaturePython)
  n = 1
  ref = Tl_element
FEATURE [App::DocumentObjectGroupPython] G4_Tl  # scripted group (container) (typed FeaturePython)
  Dunit = g/cm3
  Dvalue = 11.72
  Group = -> [Tl_element002]
  conduct = 2
  density = 1
  expand = 3
  formula = Tl
  name = G4_Tl
  specific = 4
FEATURE [App::DocumentObjectGroupPython] Pb_element003  label="Pb_element : 1"  # scripted group (container) (typed FeaturePython)
  n = 1
  ref = Pb_element
FEATURE [App::DocumentObjectGroupPython] G4_Pb  # scripted group (container) (typed FeaturePython)
  Dunit = g/cm3
  Dvalue = 11.35
  Group = -> [Pb_element003]
  conduct = 2
  density = 1
  expand = 3
  formula = Pb
  name = G4_Pb
  specific = 4
FEATURE [App::DocumentObjectGroupPython] Bi_element002  label="Bi_element : 1"  # scripted group (container) (typed FeaturePython)
  n = 1
  ref = Bi_element
FEATURE [App::DocumentObjectGroupPython] G4_Bi  # scripted group (container) (typed FeaturePython)
  Dunit = g/cm3
  Dvalue = 9.747
  Group = -> [Bi_element002]
  conduct = 2
  density = 1
  expand = 3
  formula = Bi
  name = G4_Bi
  specific = 4
FEATURE [App::DocumentObjectGroupPython] Po_element001  label="Po_element : 1"  # scripted group (container) (typed FeaturePython)
  n = 1
  ref = Po_element
FEATURE [App::DocumentObjectGroupPython] G4_Po  # scripted group (container) (typed FeaturePython)
  Dunit = g/cm3
  Dvalue = 9.32
  Group = -> [Po_element001]
  conduct = 2
  density = 1
  expand = 3
  formula = Po
  name = G4_Po
  specific = 4
FEATURE [App::DocumentObjectGroupPython] At_element001  label="At_element : 1"  # scripted group (container) (typed FeaturePython)
  n = 1
  ref = At_element
FEATURE [App::DocumentObjectGroupPython] G4_At  # scripted group (container) (typed FeaturePython)
  Dunit = g/cm3
  Dvalue = 9.32
  Group = -> [At_element001]
  conduct = 2
  density = 1
  expand = 3
  formula = At
  name = G4_At
  specific = 4
FEATURE [App::DocumentObjectGroupPython] Rn_element001  label="Rn_element : 1"  # scripted group (container) (typed FeaturePython)
  n = 1
  ref = Rn_element
FEATURE [App::DocumentObjectGroupPython] G4_Rn  # scripted group (container) (typed FeaturePython)
  Dunit = g/cm3
  Dvalue = 0.00900662
  Group = -> [Rn_element001]
  conduct = 2
  density = 1
  expand = 3
  formula = Rn
  name = G4_Rn
  specific = 4
FEATURE [App::DocumentObjectGroupPython] Fr_element001  label="Fr_element : 1"  # scripted group (container) (typed FeaturePython)
  n = 1
  ref = Fr_element
FEATURE [App::DocumentObjectGroupPython] G4_Fr  # scripted group (container) (typed FeaturePython)
  Dunit = g/cm3
  Dvalue = 1
  Group = -> [Fr_element001]
  conduct = 2
  density = 1
  expand = 3
  formula = Fr
  name = G4_Fr
  specific = 4
FEATURE [App::DocumentObjectGroupPython] Ra_element001  label="Ra_element : 1"  # scripted group (container) (typed FeaturePython)
  n = 1
  ref = Ra_element
FEATURE [App::DocumentObjectGroupPython] G4_Ra  # scripted group (container) (typed FeaturePython)
  Dunit = g/cm3
  Dvalue = 5
  Group = -> [Ra_element001]
  conduct = 2
  density = 1
  expand = 3
  formula = Ra
  name = G4_Ra
  specific = 4
FEATURE [App::DocumentObjectGroupPython] Ac_element001  label="Ac_element : 1"  # scripted group (container) (typed FeaturePython)
  n = 1
  ref = Ac_element
FEATURE [App::DocumentObjectGroupPython] G4_Ac  # scripted group (container) (typed FeaturePython)
  Dunit = g/cm3
  Dvalue = 10.07
  Group = -> [Ac_element001]
  conduct = 2
  density = 1
  expand = 3
  formula = Ac
  name = G4_Ac
  specific = 4
FEATURE [App::DocumentObjectGroupPython] Th_element001  label="Th_element : 1"  # scripted group (container) (typed FeaturePython)
  n = 1
  ref = Th_element
FEATURE [App::DocumentObjectGroupPython] G4_Th  # scripted group (container) (typed FeaturePython)
  Dunit = g/cm3
  Dvalue = 11.72
  Group = -> [Th_element001]
  conduct = 2
  density = 1
  expand = 3
  formula = Th
  name = G4_Th
  specific = 4
FEATURE [App::DocumentObjectGroupPython] Pa_element001  label="Pa_element : 1"  # scripted group (container) (typed FeaturePython)
  n = 1
  ref = Pa_element
FEATURE [App::DocumentObjectGroupPython] G4_Pa  # scripted group (container) (typed FeaturePython)
  Dunit = g/cm3
  Dvalue = 15.37
  Group = -> [Pa_element001]
  conduct = 2
  density = 1
  expand = 3
  formula = Pa
  name = G4_Pa
  specific = 4
FEATURE [App::DocumentObjectGroupPython] U_element004  label="U_element : 004"  # scripted group (container) (typed FeaturePython)
  n = 1
  ref = U_element
FEATURE [App::DocumentObjectGroupPython] G4_U  # scripted group (container) (typed FeaturePython)
  Dunit = g/cm3
  Dvalue = 18.95
  Group = -> [U_element004]
  conduct = 2
  density = 1
  expand = 3
  formula = U
  name = G4_U
  specific = 4
FEATURE [App::DocumentObjectGroupPython] Np_element001  label="Np_element : 1"  # scripted group (container) (typed FeaturePython)
  n = 1
  ref = Np_element
FEATURE [App::DocumentObjectGroupPython] G4_Np  # scripted group (container) (typed FeaturePython)
  Dunit = g/cm3
  Dvalue = 20.25
  Group = -> [Np_element001]
  conduct = 2
  density = 1
  expand = 3
  formula = Np
  name = G4_Np
  specific = 4
FEATURE [App::DocumentObjectGroupPython] Pu_element002  label="Pu_element : 002"  # scripted group (container) (typed FeaturePython)
  n = 1
  ref = Pu_element
FEATURE [App::DocumentObjectGroupPython] G4_Pu  # scripted group (container) (typed FeaturePython)
  Dunit = g/cm3
  Dvalue = 19.84
  Group = -> [Pu_element002]
  conduct = 2
  density = 1
  expand = 3
  formula = Pu
  name = G4_Pu
  specific = 4
FEATURE [App::DocumentObjectGroupPython] Am_element001  label="Am_element : 1"  # scripted group (container) (typed FeaturePython)
  n = 1
  ref = Am_element
FEATURE [App::DocumentObjectGroupPython] G4_Am  # scripted group (container) (typed FeaturePython)
  Dunit = g/cm3
  Dvalue = 13.67
  Group = -> [Am_element001]
  conduct = 2
  density = 1
  expand = 3
  formula = Am
  name = G4_Am
  specific = 4
FEATURE [App::DocumentObjectGroupPython] Cm_element001  label="Cm_element : 1"  # scripted group (container) (typed FeaturePython)
  n = 1
  ref = Cm_element
FEATURE [App::DocumentObjectGroupPython] G4_Cm  # scripted group (container) (typed FeaturePython)
  Dunit = g/cm3
  Dvalue = 13.51
  Group = -> [Cm_element001]
  conduct = 2
  density = 1
  expand = 3
  formula = Cm
  name = G4_Cm
  specific = 4
FEATURE [App::DocumentObjectGroupPython] Bk_element001  label="Bk_element : 1"  # scripted group (container) (typed FeaturePython)
  n = 1
  ref = Bk_element
FEATURE [App::DocumentObjectGroupPython] G4_Bk  # scripted group (container) (typed FeaturePython)
  Dunit = g/cm3
  Dvalue = 14
  Group = -> [Bk_element001]
  conduct = 2
  density = 1
  expand = 3
  formula = Bk
  name = G4_Bk
  specific = 4
FEATURE [App::DocumentObjectGroupPython] Cf_element001  label="Cf_element : 1"  # scripted group (container) (typed FeaturePython)
  n = 1
  ref = Cf_element
FEATURE [App::DocumentObjectGroupPython] G4_Cf  # scripted group (container) (typed FeaturePython)
  Dunit = g/cm3
  Dvalue = 10
  Group = -> [Cf_element001]
  conduct = 2
  density = 1
  expand = 3
  formula = Cf
  name = G4_Cf
  specific = 4
FEATURE [App::DocumentObjectGroupPython] Element  # scripted group (container) (typed FeaturePython)
  Group = -> [G4_H,G4_He,G4_Li,G4_Be,G4_B,G4_C,G4_N,G4_O,G4_F,G4_Ne,G4_Na,G4_Mg,G4_Al,G4_Si,G4_P,G4_S,G4_Cl,G4_Ar,G4_K,G4_Ca,G4_Sc,G4_Ti,G4_V,G4_Cr,G4_Mn,G4_Fe,G4_Co,G4_Ni,G4_Cu,G4_Zn,G4_Ga,G4_Ge,G4_As,G4_Se,G4_Br,G4_Kr,G4_Rb,G4_Sr,G4_Y,G4_Zr,G4_Nb,G4_Mo,G4_Tc,G4_Ru,G4_Rh,G4_Pd,G4_Ag,G4_Cd,G4_In,G4_Sn,G4_Sb,G4_Te,G4_I,G4_Xe,G4_Cs,G4_Ba,G4_La,G4_Ce,G4_Pr,G4_Nd,G4_Pm,G4_Sm,G4_Eu,G4_Gd,G4_Tb,G4_Dy,G4_Ho,G4_Er,+30 more]
FEATURE [App::DocumentObjectGroupPython] H_element114  label="H_element : 063"  # scripted group (container) (typed FeaturePython)
  n = 2
  ref = H_element
FEATURE [App::DocumentObjectGroupPython] G4_lH2  # scripted group (container) (typed FeaturePython)
  Dunit = g/cm3
  Dvalue = 0.0708
  Group = -> [H_element114]
  conduct = 2
  density = 1
  expand = 3
  formula = G4_lH2
  name = G4_lH2
  specific = 4
FEATURE [App::DocumentObjectGroupPython] N_element049  label="N_element : 022"  # scripted group (container) (typed FeaturePython)
  n = 2
  ref = N_element
FEATURE [App::DocumentObjectGroupPython] G4_lN2  # scripted group (container) (typed FeaturePython)
  Dunit = g/cm3
  Dvalue = 0.807
  Group = -> [N_element049]
  conduct = 2
  density = 1
  expand = 3
  formula = G4_lN2
  name = G4_lN2
  specific = 4
FEATURE [App::DocumentObjectGroupPython] O_element106  label="O_element : 060"  # scripted group (container) (typed FeaturePython)
  n = 2
  ref = O_element
FEATURE [App::DocumentObjectGroupPython] G4_lO2  # scripted group (container) (typed FeaturePython)
  Dunit = g/cm3
  Dvalue = 1.141
  Group = -> [O_element106]
  conduct = 2
  density = 1
  expand = 3
  formula = G4_lO2
  name = G4_lO2
  specific = 4
FEATURE [App::DocumentObjectGroupPython] Ar  label="Ar : 1"  # scripted group (container) (typed FeaturePython)
  n = 1
  ref = Ar
FEATURE [App::DocumentObjectGroupPython] G4_lAr  # scripted group (container) (typed FeaturePython)
  Dunit = g/cm3
  Dvalue = 1.396
  Group = -> [Ar]
  conduct = 2
  density = 1
  expand = 3
  formula = G4_lAr
  name = G4_lAr
  specific = 4
FEATURE [App::DocumentObjectGroupPython] Br  label="Br : 1"  # scripted group (container) (typed FeaturePython)
  n = 1
  ref = Br
FEATURE [App::DocumentObjectGroupPython] G4_lBr  # scripted group (container) (typed FeaturePython)
  Dunit = g/cm3
  Dvalue = 3.1028
  Group = -> [Br]
  conduct = 2
  density = 1
  expand = 3
  formula = G4_lBr
  name = G4_lBr
  specific = 4
FEATURE [App::DocumentObjectGroupPython] Kr  label="Kr : 1"  # scripted group (container) (typed FeaturePython)
  n = 1
  ref = Kr
FEATURE [App::DocumentObjectGroupPython] G4_lKr  # scripted group (container) (typed FeaturePython)
  Dunit = g/cm3
  Dvalue = 2.418
  Group = -> [Kr]
  conduct = 2
  density = 1
  expand = 3
  formula = G4_lKr
  name = G4_lKr
  specific = 4
FEATURE [App::DocumentObjectGroupPython] Xe  label="Xe : 1"  # scripted group (container) (typed FeaturePython)
  n = 1
  ref = Xe
FEATURE [App::DocumentObjectGroupPython] G4_lXe  # scripted group (container) (typed FeaturePython)
  Dunit = g/cm3
  Dvalue = 2.953
  Group = -> [Xe]
  conduct = 2
  density = 1
  expand = 3
  formula = G4_lXe
  name = G4_lXe
  specific = 4
FEATURE [App::DocumentObjectGroupPython] O_element107  label="O_element : 061"  # scripted group (container) (typed FeaturePython)
  n = 4
  ref = O_element
FEATURE [App::DocumentObjectGroupPython] Pb_element004  label="Pb_element : 002"  # scripted group (container) (typed FeaturePython)
  n = 1
  ref = Pb_element
FEATURE [App::DocumentObjectGroupPython] W_element005  label="W_element : 005"  # scripted group (container) (typed FeaturePython)
  n = 1
  ref = W_element
FEATURE [App::DocumentObjectGroupPython] G4_PbWO4  # scripted group (container) (typed FeaturePython)
  Dunit = g/cm3
  Dvalue = 8.28
  Group = -> [O_element107,Pb_element004,W_element005]
  conduct = 2
  density = 1
  expand = 3
  formula = G4_PbWO4
  name = G4_PbWO4
  specific = 4
FEATURE [App::DocumentObjectGroupPython] alactic  label="alactic : 1"  # scripted group (container) (typed FeaturePython)
  n = 1
  ref = alactic
FEATURE [App::DocumentObjectGroupPython] G4_Galactic  # scripted group (container) (typed FeaturePython)
  Dunit = g/cm3
  Dvalue = 0
  Group = -> [alactic]
  conduct = 2
  density = 1
  expand = 3
  formula = G4_Galactic
  name = G4_Galactic
  specific = 4
FEATURE [App::DocumentObjectGroupPython] RAPHITE_POROUS  label="RAPHITE_POROUS : 1"  # scripted group (container) (typed FeaturePython)
  n = 1
  ref = RAPHITE_POROUS
FEATURE [App::DocumentObjectGroupPython] G4_GRAPHITE_POROUS  # scripted group (container) (typed FeaturePython)
  Dunit = g/cm3
  Dvalue = 1.7
  Group = -> [RAPHITE_POROUS]
  conduct = 2
  density = 1
  expand = 3
  formula = G4_GRAPHITE_POROUS
  name = G4_GRAPHITE_POROUS
  specific = 4
FEATURE [App::DocumentObjectGroupPython] H_element115  label="H_element : 0.150"  # scripted group (container) (typed FeaturePython)
  n = 0.080538
FEATURE [App::DocumentObjectGroupPython] C_element125  label="C_element : 0.600"  # scripted group (container) (typed FeaturePython)
  n = 0.599848
FEATURE [App::DocumentObjectGroupPython] O_element108  label="O_element : 0.320"  # scripted group (container) (typed FeaturePython)
  n = 0.319614
FEATURE [App::DocumentObjectGroupPython] G4_LUCITE  # scripted group (container) (typed FeaturePython)
  Dunit = g/cm3
  Dvalue = 1.19
  Group = -> [H_element115,C_element125,O_element108]
  conduct = 2
  density = 1
  expand = 3
  formula = G4_LUCITE
  name = G4_LUCITE
  specific = 4
FEATURE [App::DocumentObjectGroupPython] Cu_element002  label="Cu_element : 62"  # scripted group (container) (typed FeaturePython)
  n = 62
  ref = Cu_element
FEATURE [App::DocumentObjectGroupPython] Zn_element002  label="Zn_element : 35"  # scripted group (container) (typed FeaturePython)
  n = 35
  ref = Zn_element
FEATURE [App::DocumentObjectGroupPython] Pb_element005  label="Pb_element : 3"  # scripted group (container) (typed FeaturePython)
  n = 3
  ref = Pb_element
FEATURE [App::DocumentObjectGroupPython] G4_BRASS  # scripted group (container) (typed FeaturePython)
  Dunit = g/cm3
  Dvalue = 8.52
  Group = -> [Cu_element002,Zn_element002,Pb_element005]
  conduct = 2
  density = 1
  expand = 3
  formula = G4_BRASS
  name = G4_BRASS
  specific = 4
FEATURE [App::DocumentObjectGroupPython] Cu_element003  label="Cu_element : 89"  # scripted group (container) (typed FeaturePython)
  n = 89
  ref = Cu_element
FEATURE [App::DocumentObjectGroupPython] Zn_element003  label="Zn_element : 9"  # scripted group (container) (typed FeaturePython)
  n = 9
  ref = Zn_element
FEATURE [App::DocumentObjectGroupPython] Pb_element006  label="Pb_element : 2"  # scripted group (container) (typed FeaturePython)
  n = 2
  ref = Pb_element
FEATURE [App::DocumentObjectGroupPython] G4_BRONZE  # scripted group (container) (typed FeaturePython)
  Dunit = g/cm3
  Dvalue = 8.82
  Group = -> [Cu_element003,Zn_element003,Pb_element006]
  conduct = 2
  density = 1
  expand = 3
  formula = G4_BRONZE
  name = G4_BRONZE
  specific = 4
FEATURE [App::DocumentObjectGroupPython] Fe_element008  label="Fe_element : 74"  # scripted group (container) (typed FeaturePython)
  n = 74
  ref = Fe_element
FEATURE [App::DocumentObjectGroupPython] Cr_element002  label="Cr_element : 18"  # scripted group (container) (typed FeaturePython)
  n = 18
  ref = Cr_element
FEATURE [App::DocumentObjectGroupPython] Ni_element002  label="Ni_element : 8"  # scripted group (container) (typed FeaturePython)
  n = 8
  ref = Ni_element
FEATURE [App::DocumentObjectGroupPython] G4_STAINLESS_STEEL  label="G4_STAINLESS-STEEL"  # scripted group (container) (typed FeaturePython)
  Dunit = g/cm3
  Dvalue = 8
  Group = -> [Fe_element008,Cr_element002,Ni_element002]
  conduct = 2
  density = 1
  expand = 3
  formula = G4_STAINLESS-STEEL
  name = G4_STAINLESS-STEEL
  specific = 4
FEATURE [App::DocumentObjectGroupPython] H_element116  label="H_element : 064"  # scripted group (container) (typed FeaturePython)
  n = 18
  ref = H_element
FEATURE [App::DocumentObjectGroupPython] C_element126  label="C_element : 071"  # scripted group (container) (typed FeaturePython)
  n = 12
  ref = C_element
FEATURE [App::DocumentObjectGroupPython] O_element109  label="O_element : 062"  # scripted group (container) (typed FeaturePython)
  n = 7
  ref = O_element
FEATURE [App::DocumentObjectGroupPython] G4_CR39  # scripted group (container) (typed FeaturePython)
  Dunit = g/cm3
  Dvalue = 1.32
  Group = -> [H_element116,C_element126,O_element109]
  conduct = 2
  density = 1
  expand = 3
  formula = G4_CR39
  name = G4_CR39
  specific = 4
FEATURE [App::DocumentObjectGroupPython] H_element117  label="H_element : 38"  # scripted group (container) (typed FeaturePython)
  n = 38
  ref = H_element
FEATURE [App::DocumentObjectGroupPython] C_element127  label="C_element : 072"  # scripted group (container) (typed FeaturePython)
  n = 18
  ref = C_element
FEATURE [App::DocumentObjectGroupPython] O_element110  label="O_element : 063"  # scripted group (container) (typed FeaturePython)
  n = 1
  ref = O_element
FEATURE [App::DocumentObjectGroupPython] G4_OCTADECANOL  # scripted group (container) (typed FeaturePython)
  Dunit = g/cm3
  Dvalue = 0.812
  Group = -> [H_element117,C_element127,O_element110]
  conduct = 2
  density = 1
  expand = 3
  formula = G4_OCTADECANOL
  name = G4_OCTADECANOL
  specific = 4
FEATURE [App::DocumentObjectGroupPython] HEP  # scripted group (container) (typed FeaturePython)
  Group = -> [G4_lH2,G4_lN2,G4_lO2,G4_lAr,G4_lBr,G4_lKr,G4_lXe,G4_PbWO4,G4_Galactic,G4_GRAPHITE_POROUS,G4_LUCITE,G4_BRASS,G4_BRONZE,G4_STAINLESS_STEEL,G4_CR39,G4_OCTADECANOL]
FEATURE [App::DocumentObjectGroupPython] C_element128  label="C_element : 073"  # scripted group (container) (typed FeaturePython)
  n = 14
  ref = C_element
FEATURE [App::DocumentObjectGroupPython] H_element118  label="H_element : 065"  # scripted group (container) (typed FeaturePython)
  n = 10
  ref = H_element
FEATURE [App::DocumentObjectGroupPython] O_element111  label="O_element : 064"  # scripted group (container) (typed FeaturePython)
  n = 2
  ref = O_element
FEATURE [App::DocumentObjectGroupPython] N_element050  label="N_element : 023"  # scripted group (container) (typed FeaturePython)
  n = 2
  ref = N_element
FEATURE [App::DocumentObjectGroupPython] G4_KEVLAR  # scripted group (container) (typed FeaturePython)
  Dunit = g/cm3
  Dvalue = 1.44
  Group = -> [C_element128,H_element118,O_element111,N_element050]
  conduct = 2
  density = 1
  expand = 3
  formula = G4_KEVLAR
  name = G4_KEVLAR
  specific = 4
FEATURE [App::DocumentObjectGroupPython] C_element129  label="C_element : 074"  # scripted group (container) (typed FeaturePython)
  n = 10
  ref = C_element
FEATURE [App::DocumentObjectGroupPython] H_element119  label="H_element : 066"  # scripted group (container) (typed FeaturePython)
  n = 8
  ref = H_element
FEATURE [App::DocumentObjectGroupPython] O_element112  label="O_element : 065"  # scripted group (container) (typed FeaturePython)
  n = 4
  ref = O_element
FEATURE [App::DocumentObjectGroupPython] G4_DACRON  # scripted group (container) (typed FeaturePython)
  Dunit = g/cm3
  Dvalue = 1.4
  Group = -> [C_element129,H_element119,O_element112]
  conduct = 2
  density = 1
  expand = 3
  formula = G4_DACRON
  name = G4_DACRON
  specific = 4
FEATURE [App::DocumentObjectGroupPython] C_element130  label="C_element : 075"  # scripted group (container) (typed FeaturePython)
  n = 4
  ref = C_element
FEATURE [App::DocumentObjectGroupPython] H_element120  label="H_element : 067"  # scripted group (container) (typed FeaturePython)
  n = 5
  ref = H_element
FEATURE [App::DocumentObjectGroupPython] Cl_element030  label="Cl_element : 016"  # scripted group (container) (typed FeaturePython)
  n = 1
  ref = Cl_element
FEATURE [App::DocumentObjectGroupPython] G4_NEOPRENE  # scripted group (container) (typed FeaturePython)
  Dunit = g/cm3
  Dvalue = 1.23
  Group = -> [C_element130,H_element120,Cl_element030]
  conduct = 2
  density = 1
  expand = 3
  formula = G4_NEOPRENE
  name = G4_NEOPRENE
  specific = 4
FEATURE [App::DocumentObjectGroupPython] Space  # scripted group (container) (typed FeaturePython)
  Group = -> [G4_KEVLAR,G4_DACRON,G4_NEOPRENE]
FEATURE [App::DocumentObjectGroupPython] H_element121  label="H_element : 068"  # scripted group (container) (typed FeaturePython)
  n = 5
  ref = H_element
FEATURE [App::DocumentObjectGroupPython] C_element131  label="C_element : 076"  # scripted group (container) (typed FeaturePython)
  n = 4
  ref = C_element
FEATURE [App::DocumentObjectGroupPython] N_element051  label="N_element : 3"  # scripted group (container) (typed FeaturePython)
  n = 3
  ref = N_element
FEATURE [App::DocumentObjectGroupPython] O_element113  label="O_element : 066"  # scripted group (container) (typed FeaturePython)
  n = 1
  ref = O_element
FEATURE [App::DocumentObjectGroupPython] G4_CYTOSINE  # scripted group (container) (typed FeaturePython)
  Dunit = g/cm3
  Dvalue = 1.55
  Group = -> [H_element121,C_element131,N_element051,O_element113]
  conduct = 2
  density = 1
  expand = 3
  formula = G4_CYTOSINE
  name = G4_CYTOSINE
  specific = 4
FEATURE [App::DocumentObjectGroupPython] H_element122  label="H_element : 069"  # scripted group (container) (typed FeaturePython)
  n = 6
  ref = H_element
FEATURE [App::DocumentObjectGroupPython] C_element132  label="C_element : 077"  # scripted group (container) (typed FeaturePython)
  n = 5
  ref = C_element
FEATURE [App::DocumentObjectGroupPython] N_element052  label="N_element : 024"  # scripted group (container) (typed FeaturePython)
  n = 2
  ref = N_element
FEATURE [App::DocumentObjectGroupPython] O_element114  label="O_element : 067"  # scripted group (container) (typed FeaturePython)
  n = 2
  ref = O_element
FEATURE [App::DocumentObjectGroupPython] G4_THYMINE  # scripted group (container) (typed FeaturePython)
  Dunit = g/cm3
  Dvalue = 1.23
  Group = -> [H_element122,C_element132,N_element052,O_element114]
  conduct = 2
  density = 1
  expand = 3
  formula = G4_THYMINE
  name = G4_THYMINE
  specific = 4
FEATURE [App::DocumentObjectGroupPython] H_element123  label="H_element : 070"  # scripted group (container) (typed FeaturePython)
  n = 4
  ref = H_element
FEATURE [App::DocumentObjectGroupPython] C_element133  label="C_element : 078"  # scripted group (container) (typed FeaturePython)
  n = 4
  ref = C_element
FEATURE [App::DocumentObjectGroupPython] N_element053  label="N_element : 025"  # scripted group (container) (typed FeaturePython)
  n = 2
  ref = N_element
FEATURE [App::DocumentObjectGroupPython] O_element115  label="O_element : 068"  # scripted group (container) (typed FeaturePython)
  n = 2
  ref = O_element
FEATURE [App::DocumentObjectGroupPython] G4_URACIL  # scripted group (container) (typed FeaturePython)
  Dunit = g/cm3
  Dvalue = 1.32
  Group = -> [H_element123,C_element133,N_element053,O_element115]
  conduct = 2
  density = 1
  expand = 3
  formula = G4_URACIL
  name = G4_URACIL
  specific = 4
FEATURE [App::DocumentObjectGroupPython] H_element124  label="H_element : 071"  # scripted group (container) (typed FeaturePython)
  n = 4
  ref = H_element
FEATURE [App::DocumentObjectGroupPython] C_element134  label="C_element : 079"  # scripted group (container) (typed FeaturePython)
  n = 5
  ref = C_element
FEATURE [App::DocumentObjectGroupPython] N_element054  label="N_element : 026"  # scripted group (container) (typed FeaturePython)
  n = 5
  ref = N_element
FEATURE [App::DocumentObjectGroupPython] G4_DNA_ADENINE  # scripted group (container) (typed FeaturePython)
  Dunit = g/cm3
  Dvalue = 1
  Group = -> [H_element124,C_element134,N_element054]
  conduct = 2
  density = 1
  expand = 3
  formula = G4_DNA_ADENINE
  name = G4_DNA_ADENINE
  specific = 4
FEATURE [App::DocumentObjectGroupPython] H_element125  label="H_element : 072"  # scripted group (container) (typed FeaturePython)
  n = 4
  ref = H_element
FEATURE [App::DocumentObjectGroupPython] C_element135  label="C_element : 080"  # scripted group (container) (typed FeaturePython)
  n = 5
  ref = C_element
FEATURE [App::DocumentObjectGroupPython] N_element055  label="N_element : 027"  # scripted group (container) (typed FeaturePython)
  n = 5
  ref = N_element
FEATURE [App::DocumentObjectGroupPython] O_element116  label="O_element : 069"  # scripted group (container) (typed FeaturePython)
  n = 1
  ref = O_element
FEATURE [App::DocumentObjectGroupPython] G4_DNA_GUANINE  # scripted group (container) (typed FeaturePython)
  Dunit = g/cm3
  Dvalue = 1
  Group = -> [H_element125,C_element135,N_element055,O_element116]
  conduct = 2
  density = 1
  expand = 3
  formula = G4_DNA_GUANINE
  name = G4_DNA_GUANINE
  specific = 4
FEATURE [App::DocumentObjectGroupPython] H_element126  label="H_element : 073"  # scripted group (container) (typed FeaturePython)
  n = 4
  ref = H_element
FEATURE [App::DocumentObjectGroupPython] C_element136  label="C_element : 081"  # scripted group (container) (typed FeaturePython)
  n = 4
  ref = C_element
FEATURE [App::DocumentObjectGroupPython] N_element056  label="N_element : 028"  # scripted group (container) (typed FeaturePython)
  n = 3
  ref = N_element
FEATURE [App::DocumentObjectGroupPython] O_element117  label="O_element : 070"  # scripted group (container) (typed FeaturePython)
  n = 1
  ref = O_element
FEATURE [App::DocumentObjectGroupPython] G4_DNA_CYTOSINE  # scripted group (container) (typed FeaturePython)
  Dunit = g/cm3
  Dvalue = 1
  Group = -> [H_element126,C_element136,N_element056,O_element117]
  conduct = 2
  density = 1
  expand = 3
  formula = G4_DNA_CYTOSINE
  name = G4_DNA_CYTOSINE
  specific = 4
FEATURE [App::DocumentObjectGroupPython] H_element127  label="H_element : 074"  # scripted group (container) (typed FeaturePython)
  n = 5
  ref = H_element
FEATURE [App::DocumentObjectGroupPython] C_element137  label="C_element : 082"  # scripted group (container) (typed FeaturePython)
  n = 5
  ref = C_element
FEATURE [App::DocumentObjectGroupPython] N_element057  label="N_element : 029"  # scripted group (container) (typed FeaturePython)
  n = 2
  ref = N_element
FEATURE [App::DocumentObjectGroupPython] O_element118  label="O_element : 071"  # scripted group (container) (typed FeaturePython)
  n = 2
  ref = O_element
FEATURE [App::DocumentObjectGroupPython] G4_DNA_THYMINE  # scripted group (container) (typed FeaturePython)
  Dunit = g/cm3
  Dvalue = 1
  Group = -> [H_element127,C_element137,N_element057,O_element118]
  conduct = 2
  density = 1
  expand = 3
  formula = G4_DNA_THYMINE
  name = G4_DNA_THYMINE
  specific = 4
FEATURE [App::DocumentObjectGroupPython] H_element128  label="H_element : 075"  # scripted group (container) (typed FeaturePython)
  n = 3
  ref = H_element
FEATURE [App::DocumentObjectGroupPython] C_element138  label="C_element : 083"  # scripted group (container) (typed FeaturePython)
  n = 4
  ref = C_element
FEATURE [App::DocumentObjectGroupPython] N_element058  label="N_element : 030"  # scripted group (container) (typed FeaturePython)
  n = 2
  ref = N_element
FEATURE [App::DocumentObjectGroupPython] O_element119  label="O_element : 072"  # scripted group (container) (typed FeaturePython)
  n = 2
  ref = O_element
FEATURE [App::DocumentObjectGroupPython] G4_DNA_URACIL  # scripted group (container) (typed FeaturePython)
  Dunit = g/cm3
  Dvalue = 1
  Group = -> [H_element128,C_element138,N_element058,O_element119]
  conduct = 2
  density = 1
  expand = 3
  formula = G4_DNA_URACIL
  name = G4_DNA_URACIL
  specific = 4
FEATURE [App::DocumentObjectGroupPython] H_element129  label="H_element : 076"  # scripted group (container) (typed FeaturePython)
  n = 10
  ref = H_element
FEATURE [App::DocumentObjectGroupPython] C_element139  label="C_element : 084"  # scripted group (container) (typed FeaturePython)
  n = 10
  ref = C_element
FEATURE [App::DocumentObjectGroupPython] N_element059  label="N_element : 031"  # scripted group (container) (typed FeaturePython)
  n = 5
  ref = N_element
FEATURE [App::DocumentObjectGroupPython] O_element120  label="O_element : 073"  # scripted group (container) (typed FeaturePython)
  n = 4
  ref = O_element
FEATURE [App::DocumentObjectGroupPython] G4_DNA_ADENOSINE  # scripted group (container) (typed FeaturePython)
  Dunit = g/cm3
  Dvalue = 1
  Group = -> [H_element129,C_element139,N_element059,O_element120]
  conduct = 2
  density = 1
  expand = 3
  formula = G4_DNA_ADENOSINE
  name = G4_DNA_ADENOSINE
  specific = 4
FEATURE [App::DocumentObjectGroupPython] H_element130  label="H_element : 077"  # scripted group (container) (typed FeaturePython)
  n = 10
  ref = H_element
FEATURE [App::DocumentObjectGroupPython] C_element140  label="C_element : 085"  # scripted group (container) (typed FeaturePython)
  n = 10
  ref = C_element
FEATURE [App::DocumentObjectGroupPython] N_element060  label="N_element : 032"  # scripted group (container) (typed FeaturePython)
  n = 5
  ref = N_element
FEATURE [App::DocumentObjectGroupPython] O_element121  label="O_element : 074"  # scripted group (container) (typed FeaturePython)
  n = 5
  ref = O_element
FEATURE [App::DocumentObjectGroupPython] G4_DNA_GUANOSINE  # scripted group (container) (typed FeaturePython)
  Dunit = g/cm3
  Dvalue = 1
  Group = -> [H_element130,C_element140,N_element060,O_element121]
  conduct = 2
  density = 1
  expand = 3
  formula = G4_DNA_GUANOSINE
  name = G4_DNA_GUANOSINE
  specific = 4
FEATURE [App::DocumentObjectGroupPython] H_element131  label="H_element : 078"  # scripted group (container) (typed FeaturePython)
  n = 10
  ref = H_element
FEATURE [App::DocumentObjectGroupPython] C_element141  label="C_element : 086"  # scripted group (container) (typed FeaturePython)
  n = 9
  ref = C_element
FEATURE [App::DocumentObjectGroupPython] N_element061  label="N_element : 033"  # scripted group (container) (typed FeaturePython)
  n = 3
  ref = N_element
FEATURE [App::DocumentObjectGroupPython] O_element122  label="O_element : 075"  # scripted group (container) (typed FeaturePython)
  n = 5
  ref = O_element
FEATURE [App::DocumentObjectGroupPython] G4_DNA_CYTIDINE  # scripted group (container) (typed FeaturePython)
  Dunit = g/cm3
  Dvalue = 1
  Group = -> [H_element131,C_element141,N_element061,O_element122]
  conduct = 2
  density = 1
  expand = 3
  formula = G4_DNA_CYTIDINE
  name = G4_DNA_CYTIDINE
  specific = 4
FEATURE [App::DocumentObjectGroupPython] H_element132  label="H_element : 079"  # scripted group (container) (typed FeaturePython)
  n = 9
  ref = H_element
FEATURE [App::DocumentObjectGroupPython] C_element142  label="C_element : 087"  # scripted group (container) (typed FeaturePython)
  n = 9
  ref = C_element
FEATURE [App::DocumentObjectGroupPython] N_element062  label="N_element : 034"  # scripted group (container) (typed FeaturePython)
  n = 2
  ref = N_element
FEATURE [App::DocumentObjectGroupPython] O_element123  label="O_element : 076"  # scripted group (container) (typed FeaturePython)
  n = 6
  ref = O_element
FEATURE [App::DocumentObjectGroupPython] G4_DNA_URIDINE  # scripted group (container) (typed FeaturePython)
  Dunit = g/cm3
  Dvalue = 1
  Group = -> [H_element132,C_element142,N_element062,O_element123]
  conduct = 2
  density = 1
  expand = 3
  formula = G4_DNA_URIDINE
  name = G4_DNA_URIDINE
  specific = 4
FEATURE [App::DocumentObjectGroupPython] H_element133  label="H_element : 080"  # scripted group (container) (typed FeaturePython)
  n = 11
  ref = H_element
FEATURE [App::DocumentObjectGroupPython] C_element143  label="C_element : 088"  # scripted group (container) (typed FeaturePython)
  n = 10
  ref = C_element
FEATURE [App::DocumentObjectGroupPython] N_element063  label="N_element : 035"  # scripted group (container) (typed FeaturePython)
  n = 2
  ref = N_element
FEATURE [App::DocumentObjectGroupPython] O_element124  label="O_element : 077"  # scripted group (container) (typed FeaturePython)
  n = 6
  ref = O_element
FEATURE [App::DocumentObjectGroupPython] G4_DNA_METHYLURIDINE  # scripted group (container) (typed FeaturePython)
  Dunit = g/cm3
  Dvalue = 1
  Group = -> [H_element133,C_element143,N_element063,O_element124]
  conduct = 2
  density = 1
  expand = 3
  formula = G4_DNA_METHYLURIDINE
  name = G4_DNA_METHYLURIDINE
  specific = 4
FEATURE [App::DocumentObjectGroupPython] P_element014  label="P_element : 003"  # scripted group (container) (typed FeaturePython)
  n = 1
  ref = P_element
FEATURE [App::DocumentObjectGroupPython] O_element125  label="O_element : 078"  # scripted group (container) (typed FeaturePython)
  n = 3
  ref = O_element
FEATURE [App::DocumentObjectGroupPython] G4_DNA_MONOPHOSPHATE  # scripted group (container) (typed FeaturePython)
  Dunit = g/cm3
  Dvalue = 1
  Group = -> [P_element014,O_element125]
  conduct = 2
  density = 1
  expand = 3
  formula = G4_DNA_MONOPHOSPHATE
  name = G4_DNA_MONOPHOSPHATE
  specific = 4
FEATURE [App::DocumentObjectGroupPython] H_element134  label="H_element : 081"  # scripted group (container) (typed FeaturePython)
  n = 10
  ref = H_element
FEATURE [App::DocumentObjectGroupPython] C_element144  label="C_element : 089"  # scripted group (container) (typed FeaturePython)
  n = 10
  ref = C_element
FEATURE [App::DocumentObjectGroupPython] N_element064  label="N_element : 036"  # scripted group (container) (typed FeaturePython)
  n = 5
  ref = N_element
FEATURE [App::DocumentObjectGroupPython] O_element126  label="O_element : 079"  # scripted group (container) (typed FeaturePython)
  n = 7
  ref = O_element
FEATURE [App::DocumentObjectGroupPython] P_element015  label="P_element : 004"  # scripted group (container) (typed FeaturePython)
  n = 1
  ref = P_element
FEATURE [App::DocumentObjectGroupPython] G4_DNA_A  # scripted group (container) (typed FeaturePython)
  Dunit = g/cm3
  Dvalue = 1
  Group = -> [H_element134,C_element144,N_element064,O_element126,P_element015]
  conduct = 2
  density = 1
  expand = 3
  formula = G4_DNA_A
  name = G4_DNA_A
  specific = 4
FEATURE [App::DocumentObjectGroupPython] H_element135  label="H_element : 082"  # scripted group (container) (typed FeaturePython)
  n = 10
  ref = H_element
FEATURE [App::DocumentObjectGroupPython] C_element145  label="C_element : 090"  # scripted group (container) (typed FeaturePython)
  n = 10
  ref = C_element
FEATURE [App::DocumentObjectGroupPython] N_element065  label="N_element : 037"  # scripted group (container) (typed FeaturePython)
  n = 5
  ref = N_element
FEATURE [App::DocumentObjectGroupPython] O_element127  label="O_element : 8"  # scripted group (container) (typed FeaturePython)
  n = 8
  ref = O_element
FEATURE [App::DocumentObjectGroupPython] P_element016  label="P_element : 005"  # scripted group (container) (typed FeaturePython)
  n = 1
  ref = P_element
FEATURE [App::DocumentObjectGroupPython] G4_DNA_G  # scripted group (container) (typed FeaturePython)
  Dunit = g/cm3
  Dvalue = 1
  Group = -> [H_element135,C_element145,N_element065,O_element127,P_element016]
  conduct = 2
  density = 1
  expand = 3
  formula = G4_DNA_G
  name = G4_DNA_G
  specific = 4
FEATURE [App::DocumentObjectGroupPython] H_element136  label="H_element : 083"  # scripted group (container) (typed FeaturePython)
  n = 10
  ref = H_element
FEATURE [App::DocumentObjectGroupPython] C_element146  label="C_element : 091"  # scripted group (container) (typed FeaturePython)
  n = 9
  ref = C_element
FEATURE [App::DocumentObjectGroupPython] N_element066  label="N_element : 038"  # scripted group (container) (typed FeaturePython)
  n = 3
  ref = N_element
FEATURE [App::DocumentObjectGroupPython] O_element128  label="O_element : 080"  # scripted group (container) (typed FeaturePython)
  n = 8
  ref = O_element
FEATURE [App::DocumentObjectGroupPython] P_element017  label="P_element : 006"  # scripted group (container) (typed FeaturePython)
  n = 1
  ref = P_element
FEATURE [App::DocumentObjectGroupPython] G4_DNA_C  # scripted group (container) (typed FeaturePython)
  Dunit = g/cm3
  Dvalue = 1
  Group = -> [H_element136,C_element146,N_element066,O_element128,P_element017]
  conduct = 2
  density = 1
  expand = 3
  formula = G4_DNA_C
  name = G4_DNA_C
  specific = 4
FEATURE [App::DocumentObjectGroupPython] H_element137  label="H_element : 084"  # scripted group (container) (typed FeaturePython)
  n = 9
  ref = H_element
FEATURE [App::DocumentObjectGroupPython] C_element147  label="C_element : 092"  # scripted group (container) (typed FeaturePython)
  n = 9
  ref = C_element
FEATURE [App::DocumentObjectGroupPython] N_element067  label="N_element : 039"  # scripted group (container) (typed FeaturePython)
  n = 2
  ref = N_element
FEATURE [App::DocumentObjectGroupPython] O_element129  label="O_element : 9"  # scripted group (container) (typed FeaturePython)
  n = 9
  ref = O_element
FEATURE [App::DocumentObjectGroupPython] P_element018  label="P_element : 007"  # scripted group (container) (typed FeaturePython)
  n = 1
  ref = P_element
FEATURE [App::DocumentObjectGroupPython] G4_DNA_U  # scripted group (container) (typed FeaturePython)
  Dunit = g/cm3
  Dvalue = 1
  Group = -> [H_element137,C_element147,N_element067,O_element129,P_element018]
  conduct = 2
  density = 1
  expand = 3
  formula = G4_DNA_U
  name = G4_DNA_U
  specific = 4
FEATURE [App::DocumentObjectGroupPython] H_element138  label="H_element : 085"  # scripted group (container) (typed FeaturePython)
  n = 11
  ref = H_element
FEATURE [App::DocumentObjectGroupPython] C_element148  label="C_element : 093"  # scripted group (container) (typed FeaturePython)
  n = 10
  ref = C_element
FEATURE [App::DocumentObjectGroupPython] N_element068  label="N_element : 040"  # scripted group (container) (typed FeaturePython)
  n = 2
  ref = N_element
FEATURE [App::DocumentObjectGroupPython] O_element130  label="O_element : 081"  # scripted group (container) (typed FeaturePython)
  n = 9
  ref = O_element
FEATURE [App::DocumentObjectGroupPython] P_element019  label="P_element : 008"  # scripted group (container) (typed FeaturePython)
  n = 1
  ref = P_element
FEATURE [App::DocumentObjectGroupPython] G4_DNA_MU  # scripted group (container) (typed FeaturePython)
  Dunit = g/cm3
  Dvalue = 1
  Group = -> [H_element138,C_element148,N_element068,O_element130,P_element019]
  conduct = 2
  density = 1
  expand = 3
  formula = G4_DNA_MU
  name = G4_DNA_MU
  specific = 4
FEATURE [App::DocumentObjectGroupPython] BioChemical  # scripted group (container) (typed FeaturePython)
  Group = -> [G4_CYTOSINE,G4_THYMINE,G4_URACIL,G4_DNA_ADENINE,G4_DNA_GUANINE,G4_DNA_CYTOSINE,G4_DNA_THYMINE,G4_DNA_URACIL,G4_DNA_ADENOSINE,G4_DNA_GUANOSINE,G4_DNA_CYTIDINE,G4_DNA_URIDINE,G4_DNA_METHYLURIDINE,G4_DNA_MONOPHOSPHATE,G4_DNA_A,G4_DNA_G,G4_DNA_C,G4_DNA_U,G4_DNA_MU]
FEATURE [App::DocumentObjectGroupPython] G4Materials  # scripted group (container) (typed FeaturePython)
  Group = -> [NIST,Element,HEP,Space,BioChemical]
  version = 1
FEATURE [App::DocumentObjectGroupPython] Geant4  # scripted group (container) (typed FeaturePython)
  Group = -> [G4Isotopes,G4Elements,G4Materials]
FEATURE [App::DocumentObjectGroupPython] Materials  # scripted group (container) (typed FeaturePython)
  Group = -> [Geant4]
FEATURE [Part::FeaturePython] GDMLBox_WorldBox  # WARN: FeaturePython — macro-defined, semantics opaque (R4)
  lunit = 2
  material = 7
  x = 400
  y = 400
  z = 400
FEATURE [Part::FeaturePython] GDMLBox_Box  # WARN: FeaturePython — macro-defined, semantics opaque (R4)
  lunit = 2
  material = 0
  x = 10
  y = 10
  z = 10
FEATURE [Part::FeaturePython] GDMLTube_Tube  # WARN: FeaturePython — macro-defined, semantics opaque (R4)
  aunit = 1
  deltaphi = 360
  lunit = 2
  material = 0
  rmax = 3
  rmin = 0
  startphi = 0
  z = 20
FEATURE [Part::Cut] Cut
  Base = -> GDMLBox_Box
  Placement = pos=(15,0,0) rot=(0,0,1;0rad)
  Tool = -> GDMLTube_Tube
  material = 5
FEATURE [Part::FeaturePython] Array  # Draft array (typed FeaturePython)
  Angle = 360
  ArrayType = 1
  Axis = (0,0,1)
  Base = -> Cut
  Center = (0,0,0)
  Fuse = false
  IntervalAxis = (0,0,0)
  IntervalX = (50,0,0)
  IntervalY = (0,50,0)
  IntervalZ = (0,0,50)
  NumberCircles = 3
  NumberPolar = 5
  NumberX = 2
  NumberY = 2
  NumberZ = 1
  RadialDistance = 50
  Symmetry = 1
  TangentialDistance = 25
FEATURE [Part::FeaturePython] Array001  # Draft array (typed FeaturePython)
  Angle = 360
  ArrayType = 0
  Axis = (0,0,1)
  Base = -> Array
  Center = (0,0,0)
  Fuse = false
  IntervalAxis = (0,0,0)
  IntervalX = (100,0,0)
  IntervalY = (0,100,0)
  IntervalZ = (0,0,100)
  NumberCircles = 3
  NumberPolar = 5
  NumberX = 2
  NumberY = 2
  NumberZ = 1
  RadialDistance = 50
  Symmetry = 1
  TangentialDistance = 25
  material = 193
FEATURE [App::Part] Bool_Cut  label="Arrays_of_solids"
  Group = -> [GDMLBox_Box,GDMLTube_Tube,Cut,Array,Array001]
  Origin = -> Origin003
FEATURE [App::Part] worldVOL
  Group = -> [GDMLBox_WorldBox,Bool_Cut]
  Origin = -> Origin
